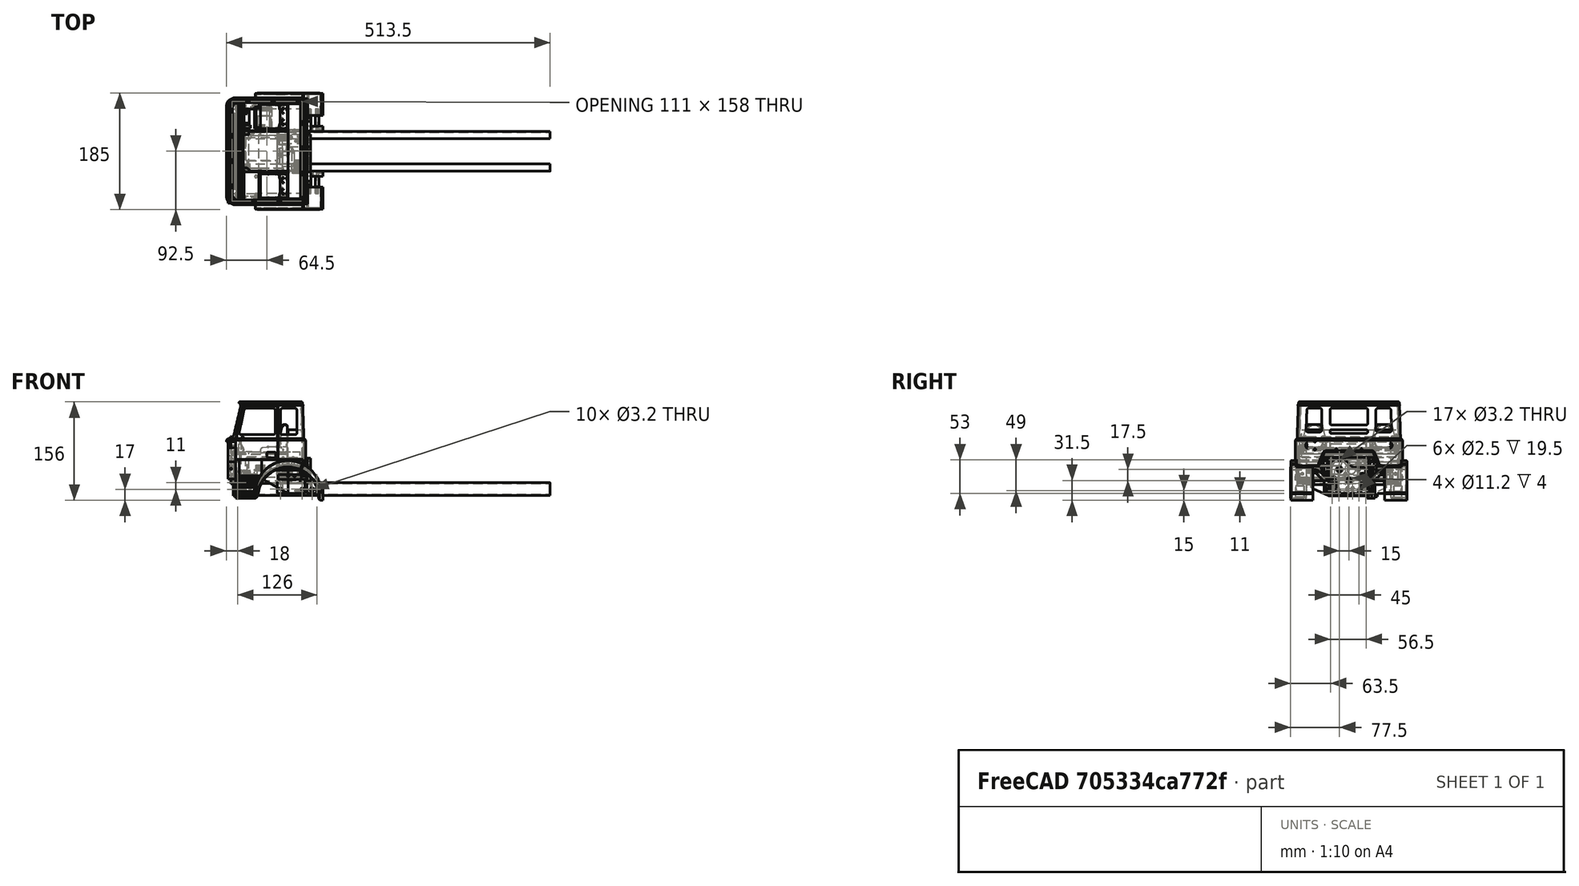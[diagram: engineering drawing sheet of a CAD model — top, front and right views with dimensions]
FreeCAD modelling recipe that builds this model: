
FCSTD DOCUMENT  (FreeCAD 0.16R6668 (Git))
Label: cab-internals
License: All rights reserved
LicenseURL: http://en.wikipedia.org/wiki/All_rights_reserved
objects: Part::Box×270, Part::Cut×252, Part::Cylinder×238, Part::MultiFuse×182, Part::Fillet×140, Part::Chamfer×61, Part::Mirroring×33, Part::Feature×16, Part::Loft×6, Part::Extrusion×2
note: 1200 computed .brp shape members not serialized (recipe doc carries the construction recipe); baked Part::Feature solids carry a one-line shape summary decoded from their .brp

FEATURE [Part::Feature] Cut179  label="cab_tilt_lower002"
  Placement = pos=(15.5,45,-15) rot=(0,0,1;0rad)
  shape: bbox 4 x 120 x 28 mm, 33 faces (baked)
FEATURE [Part::Feature] Cut180  label="cab_tilt_upper002"
  Placement = pos=(15.5,45,-15) rot=(0,0,1;0rad)
  shape: bbox 5.33 x 120 x 34.16 mm, 49 faces (baked)
FEATURE [Part::Cylinder] Cylinder188
  Angle = 360
  Height = 33
  Placement = pos=(98,175,-23) rot=(1,0,0;1.5708rad)
  Radius = 50
FEATURE [Part::Cylinder] Cylinder189
  Angle = 360
  Height = 35
  Placement = pos=(98,177,-23) rot=(1,0,0;1.5708rad)
  Radius = 52
FEATURE [Part::Cylinder] Cylinder190
  Angle = 360
  Height = 33
  Placement = pos=(98,177,-30) rot=(1,0,0;1.5708rad)
  Radius = 48
FEATURE [Part::MultiFuse] Fusion135
  Shapes = -> [Cylinder188,Cylinder190]
FEATURE [Part::Cut] Cut300
  Base = -> Cylinder189
  Tool = -> Fusion135
FEATURE [Part::Box] Box251  label="Cube477"
  Height = 10
  Length = 6.5
  Placement = pos=(145.5,142,-33) rot=(0,0,1;0rad)
  Width = 35
FEATURE [Part::Box] Box252  label="Cube478"
  Height = 10
  Length = 4.5
  Placement = pos=(143.5,140,-33) rot=(0,0,1;0rad)
  Width = 35
FEATURE [Part::Cut] Cut301
  Base = -> Box251
  Tool = -> Box252
FEATURE [Part::MultiFuse] Fusion136
  Shapes = -> [Cut300,Cut301]
FEATURE [Part::Chamfer] Chamfer044
  Base = -> Fusion136
  Edges = 1 edges r=1.99: [Edge8]
FEATURE [Part::Chamfer] Chamfer045
  Base = -> Chamfer044
  Edges = 1 edges r=2.49: [Edge30]
FEATURE [Part::Box] Box253  label="Cube479"
  Height = 11
  Length = 7.5
  Placement = pos=(117.3,133.5,15) rot=(0,1,0;0.471239rad)
  Width = 35
FEATURE [Part::Cylinder] Cylinder192
  Angle = 360
  Height = 23
  Placement = pos=(98,175,-23) rot=(0.829023,-0.395424,0.395424;1.75721rad)
  Radius = 50
FEATURE [Part::Cut] Cut302
  Base = -> Chamfer045
  Tool = -> Box253
FEATURE [Part::Cylinder] Cylinder193
  Angle = 360
  Height = 33
  Placement = pos=(98,175,-23) rot=(1,0,0;1.5708rad)
  Radius = 48
FEATURE [Part::Cut] Cut303
  Base = -> Cylinder192
  Tool = -> Cylinder193
FEATURE [Part::MultiFuse] Fusion137
  Shapes = -> [Cut302,Cut303]
FEATURE [Part::Chamfer] Chamfer046
  Base = -> Fusion137
  Edges = 1 edges r=1.99: [Edge50]
  Placement = pos=(1,0,-1) rot=(0,0,1;0rad)
FEATURE [Part::Fillet] Fillet132
  Base = -> Chamfer046
  Edges = 1 edges r=1: [Edge53]
FEATURE [Part::Cylinder] Cylinder194
  Angle = 360
  Height = 10
  Placement = pos=(144,152,0) rot=(1,0,0;1.5708rad)
  Radius = 3
FEATURE [Part::Cylinder] Cylinder195
  Angle = 360
  Height = 10
  Placement = pos=(144,152,0) rot=(1,0,0;1.5708rad)
  Radius = 1.5
FEATURE [Part::Cut] Cut304
  Base = -> Cylinder194
  Placement = pos=(-13,0,12) rot=(0,0,1;0rad)
  Tool = -> Cylinder195
FEATURE [Part::Cylinder] Cylinder196
  Angle = 360
  Height = 10
  Placement = pos=(144,152,0) rot=(1,0,0;1.5708rad)
  Radius = 3
FEATURE [Part::Cylinder] Cylinder197
  Angle = 360
  Height = 10
  Placement = pos=(144,152,0) rot=(1,0,0;1.5708rad)
  Radius = 1.5
FEATURE [Part::Cut] Cut305
  Base = -> Cylinder196
  Placement = pos=(0,0,-6) rot=(0,0,1;0rad)
  Tool = -> Cylinder197
FEATURE [Part::MultiFuse] Fusion138  label="wing-right-rear_"
  Shapes = -> [Fillet132,Cut305,Cut304]
FEATURE [Part::Cylinder] Cylinder198
  Angle = 360
  Height = 35
  Placement = pos=(98,177,-23) rot=(1,0,0;1.5708rad)
  Radius = 52
FEATURE [Part::Cylinder] Cylinder199
  Angle = 360
  Height = 33
  Placement = pos=(98,175,-23) rot=(1,0,0;1.5708rad)
  Radius = 50
FEATURE [Part::Cylinder] Cylinder200
  Angle = 360
  Height = 33
  Placement = pos=(98,177,-30) rot=(1,0,0;1.5708rad)
  Radius = 48
FEATURE [Part::MultiFuse] Fusion142
  Shapes = -> [Cylinder199,Cylinder200]
FEATURE [Part::Cut] Cut307
  Base = -> Cylinder198
  Tool = -> Fusion142
FEATURE [Part::Box] Box254  label="Cube480"
  Height = 10
  Length = 6.5
  Placement = pos=(145.5,142,-33) rot=(0,0,1;0rad)
  Width = 35
FEATURE [Part::Box] Box255  label="Cube481"
  Height = 10
  Length = 4.5
  Placement = pos=(143.5,140,-33) rot=(0,0,1;0rad)
  Width = 35
FEATURE [Part::Cut] Cut308
  Base = -> Box254
  Tool = -> Box255
FEATURE [Part::MultiFuse] Fusion141
  Shapes = -> [Cut307,Cut308]
FEATURE [Part::Chamfer] Chamfer049
  Base = -> Fusion141
  Edges = 1 edges r=1.99: [Edge8]
FEATURE [Part::Chamfer] Chamfer048
  Base = -> Chamfer049
  Edges = 1 edges r=2.49: [Edge30]
FEATURE [Part::Box] Box256  label="Cube482"
  Height = 11
  Length = 7.5
  Placement = pos=(117.3,133.5,15) rot=(0,1,0;0.471239rad)
  Width = 35
FEATURE [Part::Cut] Cut306
  Base = -> Chamfer048
  Tool = -> Box256
FEATURE [Part::Cylinder] Cylinder201
  Angle = 360
  Height = 23
  Placement = pos=(98,175,-23) rot=(0.829023,-0.395424,0.395424;1.75721rad)
  Radius = 50
FEATURE [Part::Cylinder] Cylinder202
  Angle = 360
  Height = 33
  Placement = pos=(98,175,-23) rot=(1,0,0;1.5708rad)
  Radius = 48
FEATURE [Part::Cut] Cut309
  Base = -> Cylinder201
  Tool = -> Cylinder202
FEATURE [Part::MultiFuse] Fusion140
  Shapes = -> [Cut306,Cut309]
FEATURE [Part::Chamfer] Chamfer047
  Base = -> Fusion140
  Edges = 1 edges r=1.99: [Edge50]
  Placement = pos=(1,0,-1) rot=(0,0,1;0rad)
FEATURE [Part::Fillet] Fillet133
  Base = -> Chamfer047
  Edges = 1 edges r=1: [Edge53]
FEATURE [Part::Cylinder] Cylinder203
  Angle = 360
  Height = 10
  Placement = pos=(144,152,0) rot=(1,0,0;1.5708rad)
  Radius = 3
FEATURE [Part::Cylinder] Cylinder204
  Angle = 360
  Height = 10
  Placement = pos=(144,152,0) rot=(1,0,0;1.5708rad)
  Radius = 1.5
FEATURE [Part::Cut] Cut310
  Base = -> Cylinder203
  Placement = pos=(0,0,-6) rot=(0,0,1;0rad)
  Tool = -> Cylinder204
FEATURE [Part::Cylinder] Cylinder205
  Angle = 360
  Height = 10
  Placement = pos=(144,152,0) rot=(1,0,0;1.5708rad)
  Radius = 3
FEATURE [Part::Cylinder] Cylinder206
  Angle = 360
  Height = 10
  Placement = pos=(144,152,0) rot=(1,0,0;1.5708rad)
  Radius = 1.5
FEATURE [Part::Cut] Cut311
  Base = -> Cylinder205
  Placement = pos=(-13,0,12) rot=(0,0,1;0rad)
  Tool = -> Cylinder206
FEATURE [Part::MultiFuse] Fusion139  label="right-rear-wing001"
  Shapes = -> [Fillet133,Cut310,Cut311]
FEATURE [Part::Mirroring] Part__Mirroring018  label="wing-left-rear_"
  Base = (0,0,0)
  Normal = (0,1,0)
  Placement = pos=(0,170,0) rot=(0,0,1;0rad)
  Source = -> Fusion139
FEATURE [Part::Box] Box536  label="Cube761"
  Height = 64
  Length = 126
  Width = 170
FEATURE [Part::Fillet] Fillet413
  Base = -> Box536
  Edges = 2 edges r=15: [Edge1,Edge3]
FEATURE [Part::Fillet] Fillet412
  Base = -> Fillet413
  Edges = 2 edges r=10: [Edge17,Edge18]
FEATURE [Part::Box] Box537  label="Cube762"
  Height = 64
  Length = 120
  Placement = pos=(4,4,0) rot=(0,0,1;0rad)
  Width = 164
FEATURE [Part::Fillet] Fillet415
  Base = -> Box537
  Edges = 2 edges r=12: [Edge1,Edge3]
FEATURE [Part::Fillet] Fillet414
  Base = -> Fillet415
  Edges = 2 edges r=6: [Edge17,Edge18]
  Placement = pos=(-1,-1,0) rot=(0,0,1;0rad)
FEATURE [Part::Cut] Cut468  label="Cut763"
  Base = -> Fillet412
  Tool = -> Fillet414
FEATURE [Part::Cylinder] Cylinder302
  Angle = 360
  Height = 174
  Placement = pos=(98,174,-23) rot=(1,0,0;1.5708rad)
  Radius = 52
FEATURE [Part::Cut] Cut467  label="Cut762"
  Base = -> Cut468
  Tool = -> Cylinder302
FEATURE [Part::Box] Box538  label="Cube763"
  Height = 25
  Length = 131
  Placement = pos=(11,0,6) rot=(0,0,1;0rad)
  Width = 170
FEATURE [Part::Box] Box539  label="Cube764"
  Height = 25
  Length = 148
  Placement = pos=(2,2,6) rot=(0,0,1;0rad)
  Width = 166
FEATURE [Part::Box] Box540  label="Cube765"
  Height = 31
  Length = 62
  Placement = pos=(83,1,2) rot=(0,0,1;0rad)
  Width = 1
FEATURE [Part::Box] Box541  label="Cube766"
  Height = 31
  Length = 63.5
  Placement = pos=(83,-1,2) rot=(0,0,1;0.017453rad)
  Width = 2
FEATURE [Part::Cut] Cut470  label="Cut765"
  Base = -> Box540
  Tool = -> Box541
FEATURE [Part::Cylinder] Cylinder303
  Angle = 360
  Height = 10
  Placement = pos=(98,10,-23) rot=(1,0,0;1.5708rad)
  Radius = 52
FEATURE [Part::Cut] Cut469  label="Cut764"
  Base = -> Cut470
  Tool = -> Cylinder303
FEATURE [Part::Cylinder] Cylinder304
  Angle = 360
  Height = 10
  Placement = pos=(98,10,-23) rot=(1,0,0;1.5708rad)
  Radius = 52
FEATURE [Part::Box] Box542  label="Cube767"
  Height = 25
  Length = 63.5
  Placement = pos=(20,1,8) rot=(0,0,-1;0.027925rad)
  Width = 1
FEATURE [Part::Box] Box543  label="Cube768"
  Height = 25
  Length = 62.5
  Placement = pos=(20.5,1,8) rot=(0,0,1;0rad)
  Width = 1
FEATURE [Part::Cut] Cut472  label="Cut767"
  Base = -> Box543
  Tool = -> Box542
FEATURE [Part::Cut] Cut471  label="Cut766"
  Base = -> Cut472
  Tool = -> Cylinder304
FEATURE [Part::MultiFuse] Fusion305
  Shapes = -> [Cut469,Cut471]
FEATURE [Part::Box] Box544  label="Cube769"
  Height = 25
  Length = 63.5
  Placement = pos=(20,1,8) rot=(0,0,-1;0.027925rad)
  Width = 1
FEATURE [Part::Box] Box545  label="Cube770"
  Height = 25
  Length = 62.5
  Placement = pos=(20.5,1,8) rot=(0,0,1;0rad)
  Width = 1
FEATURE [Part::Cut] Cut475  label="Cut770"
  Base = -> Box545
  Tool = -> Box544
FEATURE [Part::Box] Box546  label="Cube771"
  Height = 31
  Length = 63.5
  Placement = pos=(83,-1,2) rot=(0,0,1;0.017453rad)
  Width = 2
FEATURE [Part::Box] Box547  label="Cube772"
  Height = 31
  Length = 62
  Placement = pos=(83,1,2) rot=(0,0,1;0rad)
  Width = 1
FEATURE [Part::Cut] Cut473  label="Cut768"
  Base = -> Box547
  Tool = -> Box546
FEATURE [Part::Cylinder] Cylinder305
  Angle = 360
  Height = 10
  Placement = pos=(98,10,-23) rot=(1,0,0;1.5708rad)
  Radius = 52
FEATURE [Part::Cut] Cut476  label="Cut771"
  Base = -> Cut473
  Tool = -> Cylinder305
FEATURE [Part::Cylinder] Cylinder306
  Angle = 360
  Height = 10
  Placement = pos=(98,10,-23) rot=(1,0,0;1.5708rad)
  Radius = 52
FEATURE [Part::Cut] Cut474  label="Cut769"
  Base = -> Cut475
  Tool = -> Cylinder306
FEATURE [Part::MultiFuse] Fusion306
  Shapes = -> [Cut476,Cut474]
FEATURE [Part::Mirroring] Part__Mirroring056  label="Fusion008 (Mirror #2)001"
  Base = (0,0,0)
  Normal = (0,1,0)
  Placement = pos=(0,170,0) rot=(0,0,1;0rad)
  Source = -> Fusion306
FEATURE [Part::MultiFuse] Fusion307
  Shapes = -> [Part__Mirroring056,Fusion305]
FEATURE [Part::Cut] Cut477  label="Cut772"
  Base = -> Box538
  Placement = pos=(0,0,2) rot=(0,0,1;0rad)
  Tool = -> Box539
FEATURE [Part::Cut] Cut478  label="Cut773"
  Base = -> Cut477
  Placement = pos=(0,0,-3) rot=(0,0,1;0rad)
  Tool = -> Fusion307
FEATURE [Part::Cut] Cut479  label="Cut774"
  Base = -> Cut467
  Tool = -> Cut478
FEATURE [Part::Box] Box548  label="Cube773"
  Height = 64
  Length = 21
  Width = 164
FEATURE [Part::Fillet] Fillet416
  Base = -> Box548
  Edges = 2 edges r=12: [Edge1,Edge3]
  Placement = pos=(3,3,0) rot=(0,0,1;0rad)
FEATURE [Part::Box] Box549  label="Cube774"
  Height = 59
  Length = 16
  Placement = pos=(15,0,0) rot=(0,0,1;0rad)
  Width = 170
FEATURE [Part::Box] Box550  label="Cube775"
  Height = 59
  Length = 21
  Placement = pos=(-13,3,0) rot=(0,0,1;0rad)
  Width = 164
FEATURE [Part::Box] Box551  label="Cube776"
  Height = 59
  Length = 21
  Placement = pos=(-13,0,0) rot=(0,0,1;0rad)
  Width = 170
FEATURE [Part::Fillet] Fillet417
  Base = -> Box551
  Edges = 2 edges r=15: [Edge1,Edge3]
FEATURE [Part::Fillet] Fillet418
  Base = -> Box550
  Edges = 2 edges r=12: [Edge1,Edge3]
  Placement = pos=(3,0,0) rot=(0,0,1;0rad)
FEATURE [Part::Cut] Cut480  label="Cut775"
  Base = -> Fillet417
  Placement = pos=(13,0,0) rot=(0,0,1;0rad)
  Tool = -> Fillet418
FEATURE [Part::Cut] Cut481  label="Cut776"
  Base = -> Cut480
  Tool = -> Box549
FEATURE [Part::Feature] Face030
  Placement = pos=(0,0,-10) rot=(0,0,1;0rad)
  shape: bbox 128.7 x 180.4 x 2e-07 mm, 1 faces, 0 solids (baked)
FEATURE [Part::Feature] Face031
  Placement = pos=(0,0,50) rot=(0,0,1;0rad)
  shape: bbox 110 x 176 x 2e-07 mm, 1 faces, 0 solids (baked)
FEATURE [Part::Loft] Loft015
  Closed = false
  Ruled = false
  Sections = -> [Face031,Face030]
  Solid = true
FEATURE [Part::Feature] Face032
  Placement = pos=(0,0,50) rot=(0,0,1;0rad)
  shape: bbox 103.4 x 169.4 x 2e-07 mm, 1 faces, 0 solids (baked)
FEATURE [Part::Feature] Face033
  Placement = pos=(0,0,-10) rot=(0,0,1;0rad)
  shape: bbox 122.1 x 173.8 x 2e-07 mm, 1 faces, 0 solids (baked)
FEATURE [Part::Loft] Loft016
  Closed = false
  Ruled = false
  Sections = -> [Face032,Face033]
  Solid = true
FEATURE [Part::Cut] Cut482  label="Cut777"
  Base = -> Loft015
  Tool = -> Loft016
FEATURE [Part::Box] Box552  label="Cube777"
  Height = 55
  Length = 10
  Placement = pos=(0,7,68) rot=(0,1,0;0.226893rad)
  Width = 156
FEATURE [Part::Chamfer] Chamfer066
  Base = -> Cut479
  Edges = 4 edges r=2.5: [Edge1,Edge4,Edge5,Edge8]
FEATURE [Part::Chamfer] Chamfer067
  Base = -> Chamfer066
  Edges = 4 edges r=0.9: [Edge52,Edge80,Edge102,Edge110]
FEATURE [Part::Fillet] Fillet419
  Base = -> Box552
  Edges = 4 edges r=5: [Edge9,Edge10,Edge11,Edge12]
  Placement = pos=(6,0,-1) rot=(0,0,1;0rad)
FEATURE [Part::Box] Box553  label="Cube778"
  Height = 42
  Length = 26
  Placement = pos=(89,4.3,70) rot=(-1,0,0;0.038397rad)
  Width = 5
FEATURE [Part::Fillet] Fillet420
  Base = -> Box553
  Edges = 4 edges r=3: [Edge2,Edge4,Edge6,Edge8]
  Placement = pos=(-3,-2,0) rot=(0,0,1;0rad)
FEATURE [Part::Box] Box554  label="Cube779"
  Height = 42
  Length = 58
  Placement = pos=(19.5,2,70) rot=(-1,0,0;0.038397rad)
  Width = 5
FEATURE [Part::Box] Box555  label="Cube780"
  Height = 48
  Length = 11
  Placement = pos=(8.5,1,70) rot=(-0.179679,0.983544,0.018885;0.212918rad)
  Width = 7
FEATURE [Part::Cut] Cut483  label="Cut778"
  Base = -> Box554
  Tool = -> Box555
FEATURE [Part::Fillet] Fillet421
  Base = -> Cut483
  Edges = 4 edges r=3: [Edge2,Edge4,Edge8,Edge12]
FEATURE [Part::MultiFuse] Fusion308  label="left-windows-holes001"
  Shapes = -> [Fillet420,Fillet421]
FEATURE [Part::Box] Box556  label="Cube781"
  Height = 42
  Length = 26
  Placement = pos=(89,4.3,70) rot=(-1,0,0;0.038397rad)
  Width = 5
FEATURE [Part::Fillet] Fillet422
  Base = -> Box556
  Edges = 4 edges r=3: [Edge2,Edge4,Edge6,Edge8]
  Placement = pos=(-3,-2,0) rot=(0,0,1;0rad)
FEATURE [Part::Box] Box557  label="Cube782"
  Height = 42
  Length = 58
  Placement = pos=(19.5,2,70) rot=(-1,0,0;0.038397rad)
  Width = 5
FEATURE [Part::Box] Box558  label="Cube783"
  Height = 48
  Length = 11
  Placement = pos=(8.5,1,70) rot=(-0.179679,0.983544,0.018885;0.212918rad)
  Width = 7
FEATURE [Part::Cut] Cut484  label="Cut779"
  Base = -> Box557
  Tool = -> Box558
FEATURE [Part::Fillet] Fillet423
  Base = -> Cut484
  Edges = 4 edges r=3: [Edge2,Edge4,Edge8,Edge12]
FEATURE [Part::MultiFuse] Fusion309
  Shapes = -> [Fillet422,Fillet423]
FEATURE [Part::Mirroring] Part__Mirroring057  label="right-windows-holes001"
  Base = (0,0,0)
  Normal = (0,1,0)
  Placement = pos=(0,170,0) rot=(0,0,1;0rad)
  Source = -> Fusion309
FEATURE [Part::Box] Box559  label="Cube784"
  Height = 25
  Length = 10
  Placement = pos=(150,40,0) rot=(0,0,1;0rad)
  Width = 100
FEATURE [Part::Box] Box560  label="Cube785"
  Height = 40
  Length = 10
  Placement = pos=(150,19,0) rot=(-1,0,0;0.383972rad)
  Width = 20
FEATURE [Part::Box] Box561  label="Cube786"
  Height = 40
  Length = 10
  Placement = pos=(150,19,0) rot=(-1,0,0;0.383972rad)
  Width = 20
FEATURE [Part::Mirroring] Part__Mirroring058  label="Cube088 (Mirror #13)001"
  Base = (0,0,0)
  Normal = (0,1,0)
  Placement = pos=(0,180,0) rot=(0,0,1;0rad)
  Source = -> Box561
FEATURE [Part::MultiFuse] Fusion310
  Shapes = -> [Box560,Part__Mirroring058]
FEATURE [Part::Cut] Cut485  label="Cut780"
  Base = -> Box559
  Placement = pos=(-30,-5,20) rot=(0,0,1;0rad)
  Tool = -> Fusion310
FEATURE [Part::Fillet] Fillet424
  Base = -> Cut485
  Edges = 2 edges r=6: [Edge5,Edge6]
FEATURE [Part::Box] Box562  label="Cube787"
  Height = 27
  Length = 7
  Placement = pos=(116,55,85) rot=(0,-1,0;0.034907rad)
  Width = 60
FEATURE [Part::Box] Box563  label="Cube788"
  Height = 38
  Length = 5
  Placement = pos=(175,0,0) rot=(0,0,1;0rad)
  Width = 25
FEATURE [Part::Box] Box564  label="Cube789"
  Height = 40
  Length = 5
  Placement = pos=(175,-24,-1) rot=(-1,0,0;0.038397rad)
  Width = 24
FEATURE [Part::Cut] Cut486  label="Cut781"
  Base = -> Box563
  Placement = pos=(0,1,1) rot=(0,0,1;0rad)
  Tool = -> Box564
FEATURE [Part::Cylinder] Cylinder307
  Angle = 360
  Height = 134
  Radius = 3.7
FEATURE [Part::Fillet] Fillet425
  Base = -> Cylinder307
  Edges = 2 edges r=2: [Edge1,Edge3]
  Placement = pos=(128,152,53) rot=(1,0,0;1.5708rad)
FEATURE [Part::Box] Box565  label="Cube790"
  Height = 38
  Length = 5
  Placement = pos=(175,0,0) rot=(0,0,1;0rad)
  Width = 25
FEATURE [Part::Box] Box566  label="Cube791"
  Height = 40
  Length = 5
  Placement = pos=(175,-24,-1) rot=(-1,0,0;0.038397rad)
  Width = 24
FEATURE [Part::Cut] Cut487  label="Cut782"
  Base = -> Box565
  Placement = pos=(-57,17,74) rot=(0,0,1;0rad)
  Tool = -> Box566
FEATURE [Part::Mirroring] Part__Mirroring059  label="Cut783"
  Base = (0,0,0)
  Normal = (0,1,0)
  Placement = pos=(-57,154,73) rot=(0,0,1;0rad)
  Source = -> Cut486
FEATURE [Part::Fillet] Fillet426
  Base = -> Cut487
  Edges = 4 edges r=3: [Edge1,Edge3,Edge5,Edge10]
  Placement = pos=(3,0,-4) rot=(0,-1,0;0.034907rad)
FEATURE [Part::Fillet] Fillet427
  Base = -> Part__Mirroring059
  Edges = 4 edges r=3: [Edge1,Edge3,Edge5,Edge10]
  Placement = pos=(3,0,-4) rot=(0,-1,0;0.034907rad)
FEATURE [Part::Cylinder] Cylinder308
  Angle = 360
  Height = 60
  Radius = 3.7
FEATURE [Part::Fillet] Fillet428
  Base = -> Cylinder308
  Edges = 2 edges r=2: [Edge1,Edge3]
  Placement = pos=(125,115,75) rot=(1,0,0;1.5708rad)
FEATURE [Part::Box] Box567  label="Cube792"
  Height = 9
  Length = 14
  Width = 2
FEATURE [Part::Fillet] Fillet429
  Base = -> Box567
  Edges = 4 edges r=2: [Edge2,Edge4,Edge6,Edge8]
  Placement = pos=(68.5,0,46.5) rot=(0,0,1;0rad)
FEATURE [Part::Box] Box568  label="Cube793"
  Height = 9
  Length = 14
  Width = 2
FEATURE [Part::Fillet] Fillet430
  Base = -> Box568
  Edges = 4 edges r=2: [Edge2,Edge4,Edge6,Edge8]
  Placement = pos=(68.5,168,46.5) rot=(0,0,1;0rad)
FEATURE [Part::MultiFuse] Fusion311
  Placement = pos=(-4,0,-13) rot=(0,0,1;0rad)
  Shapes = -> [Fillet430,Fillet429]
FEATURE [Part::MultiFuse] Fusion312
  Shapes = -> [Fillet427,Box562,Part__Mirroring057,Fusion308,Fillet426]
FEATURE [Part::Box] Box569  label="Cube794"
  Height = 116
  Length = 66.5
  Placement = pos=(14.5,0,-0.5) rot=(0,0,1;0rad)
  Width = 5
FEATURE [Part::Box] Box570  label="Cube795"
  Height = 117
  Length = 67.5
  Placement = pos=(14,0,-1) rot=(0,0,1;0rad)
  Width = 5
FEATURE [Part::Box] Box571  label="Cube796"
  Height = 116
  Length = 67
  Placement = pos=(-53.2,0,65) rot=(0,1,0;0.218166rad)
  Width = 5
FEATURE [Part::Cut] Cut489  label="Cut785"
  Base = -> Box569
  Placement = pos=(0,-2,0) rot=(0,0,1;0rad)
  Tool = -> Box571
FEATURE [Part::Box] Box572  label="Cube797"
  Height = 116
  Length = 67
  Placement = pos=(-53.7,0,65) rot=(0,1,0;0.218166rad)
  Width = 5
FEATURE [Part::Cut] Cut488  label="Cut784"
  Base = -> Box570
  Placement = pos=(0,-2,0) rot=(0,0,1;0rad)
  Tool = -> Box572
FEATURE [Part::Cut] Cut490  label="Cut786"
  Base = -> Cut482
  Tool = -> Fusion312
FEATURE [Part::Cut] Cut491  label="doors-cut-002"
  Base = -> Cut488
  Placement = pos=(0.5,3,0.5) rot=(0,0,1;0rad)
  Tool = -> Cut489
FEATURE [Part::Cut] Cut492  label="Cut787"
  Base = -> Cut490
  Tool = -> Fillet419
FEATURE [Part::Box] Box573  label="Cube798"
  Height = 116
  Length = 67
  Placement = pos=(-53.2,0,65) rot=(0,1,0;0.218166rad)
  Width = 10
FEATURE [Part::Box] Box574  label="Cube799"
  Height = 116
  Length = 67
  Placement = pos=(-53.7,0,65) rot=(0,1,0;0.218166rad)
  Width = 10
FEATURE [Part::Box] Box575  label="Cube800"
  Height = 117
  Length = 67.5
  Placement = pos=(14,0,-1) rot=(0,0,1;0rad)
  Width = 10
FEATURE [Part::Cut] Cut494  label="Cut788"
  Base = -> Box575
  Placement = pos=(0,-2,0) rot=(0,0,1;0rad)
  Tool = -> Box574
FEATURE [Part::Box] Box576  label="Cube801"
  Height = 116
  Length = 66.5
  Placement = pos=(14.5,0,-0.5) rot=(0,0,1;0rad)
  Width = 10
FEATURE [Part::Cut] Cut495  label="Cut789"
  Base = -> Box576
  Placement = pos=(0,-2,0) rot=(0,0,1;0rad)
  Tool = -> Box573
FEATURE [Part::Cut] Cut493  label="doors-cut-003"
  Base = -> Cut494
  Placement = pos=(1.5,-3,0.5) rot=(0,0,1;0rad)
  Tool = -> Cut495
FEATURE [Part::Fillet] Fillet431
  Base = -> Cut492
  Edges = 4 edges r=3: [Edge209,Edge210,Edge211,Edge212]
FEATURE [Part::Cut] Cut496  label="Cut790"
  Base = -> Fillet431
  Tool = -> Fillet428
FEATURE [Part::Box] Box577  label="Cube802"
  Height = 64
  Length = 21
  Width = 164
FEATURE [Part::Fillet] Fillet432
  Base = -> Box577
  Edges = 2 edges r=18: [Edge1,Edge3]
  Placement = pos=(7,3,0) rot=(0,0,1;0rad)
FEATURE [Part::Cut] Cut497  label="Cut791"
  Base = -> Fillet416
  Tool = -> Fillet432
FEATURE [Part::MultiFuse] Fusion313
  Shapes = -> [Chamfer067,Cut497]
FEATURE [Part::Cut] Cut498  label="Cut792"
  Base = -> Fusion313
  Tool = -> Cut481
FEATURE [Part::Cut] Cut499  label="Cut793"
  Base = -> Cut498
  Tool = -> Fillet425
FEATURE [Part::Cut] Cut500  label="Cut794"
  Base = -> Cut499
  Tool = -> Fillet424
FEATURE [Part::Cut] Cut501  label="Cut795"
  Base = -> Cut500
  Tool = -> Fusion311
FEATURE [Part::Fillet] Fillet433
  Base = -> Cut501
  Edges = 2 edges r=3: [Edge74,Edge149]
FEATURE [Part::Box] Box578  label="Cube803"
  Height = 2
  Length = 117
  Placement = pos=(6,3,54) rot=(0,0,1;0rad)
  Width = 164
FEATURE [Part::Fillet] Fillet434
  Base = -> Box578
  Edges = 2 edges r=15: [Edge1,Edge3]
FEATURE [Part::Fillet] Fillet435
  Base = -> Fillet434
  Edges = 2 edges r=6: [Edge17,Edge18]
FEATURE [Part::Box] Box579  label="Cube804"
  Height = 2
  Length = 111
  Placement = pos=(6,3,54) rot=(0,0,1;0rad)
  Width = 158
FEATURE [Part::Fillet] Fillet437
  Base = -> Box579
  Edges = 2 edges r=12: [Edge1,Edge3]
FEATURE [Part::Fillet] Fillet436
  Base = -> Fillet437
  Edges = 2 edges r=3: [Edge17,Edge18]
  Placement = pos=(3,3,0) rot=(0,0,1;0rad)
FEATURE [Part::Cut] Cut502  label="Cut796"
  Base = -> Fillet435
  Placement = pos=(0,0,8) rot=(0,0,1;0rad)
  Tool = -> Fillet436
FEATURE [Part::Box] Box580  label="Cube805"
  Height = 1
  Length = 96
  Placement = pos=(26,4,116.5) rot=(0,0,1;0rad)
  Width = 162
FEATURE [Part::Box] Box581  label="Cube806"
  Height = 1
  Length = 94
  Placement = pos=(26,6,116.5) rot=(0,0,1;0rad)
  Width = 158
FEATURE [Part::Fillet] Fillet438
  Base = -> Box581
  Edges = 2 edges r=4: [Edge5,Edge7]
FEATURE [Part::Fillet] Fillet439
  Base = -> Box580
  Edges = 2 edges r=6: [Edge5,Edge7]
FEATURE [Part::Fillet] Fillet440
  Base = -> Fillet439
  Edges = 2 edges r=2: [Edge17,Edge18]
FEATURE [Part::Cut] Cut503  label="Cut797"
  Base = -> Fillet440
  Tool = -> Fillet438
FEATURE [Part::Box] Box582  label="Cube807"
  Height = 6.5
  Length = 110
  Placement = pos=(19,4,121.5) rot=(0,0,1;0rad)
  Width = 162
FEATURE [Part::Box] Box583  label="Cube808"
  Height = 5.1
  Length = 100
  Placement = pos=(19.5,5.5,122.5) rot=(0,0,1;0rad)
  Width = 159
FEATURE [Part::Fillet] Fillet441
  Base = -> Box583
  Edges = 2 edges r=10: [Edge1,Edge3]
FEATURE [Part::Fillet] Fillet442
  Base = -> Fillet441
  Edges = 2 edges r=4.5: [Edge17,Edge18]
FEATURE [Part::Fillet] Fillet443
  Base = -> Fillet442
  Edges = 4 edges r=5: [Edge1,Edge4,Edge5,Edge8]
  Placement = pos=(0.7,0,-2) rot=(0,0,1;0rad)
FEATURE [Part::Box] Box584  label="Cube809"
  Height = 5.1
  Length = 95
  Placement = pos=(23,7.5,122.5) rot=(0,0,1;0rad)
  Width = 155
FEATURE [Part::Fillet] Fillet444
  Base = -> Box584
  Edges = 2 edges r=3: [Edge5,Edge7]
FEATURE [Part::Fillet] Fillet445
  Base = -> Fillet444
  Edges = 2 edges r=8: [Edge17,Edge18]
FEATURE [Part::Fillet] Fillet446
  Base = -> Fillet445
  Edges = 1 edges r=4: [Edge4]
  Placement = pos=(0,0,-4) rot=(0,0,1;0rad)
FEATURE [Part::Cut] Cut504  label="Cut798"
  Base = -> Fillet443
  Tool = -> Fillet446
FEATURE [Part::Cylinder] Cylinder309
  Angle = 360
  Height = 7
  Placement = pos=(2,34,15) rot=(0,1,0;1.5708rad)
  Radius = 1.2
FEATURE [Part::Cylinder] Cylinder310
  Angle = 360
  Height = 4
  Placement = pos=(2,34,15) rot=(0,1,0;1.5708rad)
  Radius = 2.7
FEATURE [Part::MultiFuse] Fusion314
  Shapes = -> [Cylinder309,Cylinder310]
FEATURE [Part::Cylinder] Cylinder311
  Angle = 360
  Height = 4
  Placement = pos=(2,34,15) rot=(0,1,0;1.5708rad)
  Radius = 2.7
FEATURE [Part::Cylinder] Cylinder312
  Angle = 360
  Height = 7
  Placement = pos=(2,34,15) rot=(0,1,0;1.5708rad)
  Radius = 1.2
FEATURE [Part::MultiFuse] Fusion315
  Placement = pos=(0,102,0) rot=(0,0,1;0rad)
  Shapes = -> [Cylinder312,Cylinder311]
FEATURE [Part::MultiFuse] Fusion316
  Shapes = -> [Fusion314,Fusion315]
FEATURE [Part::Box] Box585  label="Cube810"
  Height = 34
  Length = 5
  Placement = pos=(7,38,2) rot=(0,0,1;0rad)
  Width = 94
FEATURE [Part::Chamfer] Chamfer068
  Base = -> Box585
  Edges = 1 edges r=4.99: [Edge6]
FEATURE [Part::Cylinder] Cylinder313
  Angle = 360
  Height = 10
  Placement = pos=(12,57.5,21) rot=(0,1,0;1.5708rad)
  Radius = 1.25
FEATURE [Part::Cylinder] Cylinder314
  Angle = 360
  Height = 10
  Placement = pos=(12,112.5,21) rot=(0,1,0;1.5708rad)
  Radius = 1.25
FEATURE [Part::Cylinder] Cylinder315
  Angle = 360
  Height = 10
  Placement = pos=(12,85,16) rot=(0,1,0;1.5708rad)
  Radius = 1.25
FEATURE [Part::MultiFuse] Fusion317
  Placement = pos=(-7,0,0) rot=(0,0,1;0rad)
  Shapes = -> [Cylinder313,Cylinder315,Cylinder314]
FEATURE [Part::Cylinder] Cylinder316
  Angle = 360
  Height = 10
  Placement = pos=(118,31,59.5) rot=(0,1,0;1.5708rad)
  Radius = 1.3
FEATURE [Part::Cylinder] Cylinder317
  Angle = 360
  Height = 10
  Placement = pos=(118,31,46.5) rot=(0,1,0;1.5708rad)
  Radius = 1.3
FEATURE [Part::MultiFuse] Fusion318
  Shapes = -> [Cylinder316,Cylinder317]
FEATURE [Part::Box] Box586  label="Cube811"
  Height = 6
  Length = 2
  Placement = pos=(89,3,29) rot=(0,0,1;0rad)
  Width = 2
FEATURE [Part::Box] Box587  label="Cube812"
  Height = 6
  Length = 2
  Placement = pos=(105,3,29) rot=(0,0,1;0rad)
  Width = 2
FEATURE [Part::MultiFuse] Fusion319
  Shapes = -> [Box586,Box587]
FEATURE [Part::Chamfer] Chamfer069
  Base = -> Fusion319
  Edges = 2 edges r=1.99: [Edge8,Edge20]
FEATURE [Part::Box] Box588  label="Cube813"
  Height = 6
  Length = 2
  Placement = pos=(89,3,29) rot=(0,0,1;0rad)
  Width = 2
FEATURE [Part::Box] Box589  label="Cube814"
  Height = 6
  Length = 2
  Placement = pos=(105,3,29) rot=(0,0,1;0rad)
  Width = 2
FEATURE [Part::MultiFuse] Fusion320
  Shapes = -> [Box588,Box589]
FEATURE [Part::Chamfer] Chamfer070
  Base = -> Fusion320
  Edges = 2 edges r=1.99: [Edge8,Edge20]
FEATURE [Part::Mirroring] Part__Mirroring060  label="Chamfer052 (Mirror #23)001"
  Base = (0,0,0)
  Normal = (0,1,0)
  Placement = pos=(0,170,0) rot=(0,0,1;0rad)
  Source = -> Chamfer070
FEATURE [Part::Cylinder] Cylinder318
  Angle = 360
  Height = 10
  Placement = pos=(30,11,114) rot=(1,0,0;1.5708rad)
  Radius = 1
FEATURE [Part::Cylinder] Cylinder319
  Angle = 360
  Height = 10
  Placement = pos=(26,11,66) rot=(1,0,0;1.5708rad)
  Radius = 1
FEATURE [Part::MultiFuse] Fusion321
  Shapes = -> [Cylinder318,Cylinder319]
FEATURE [Part::Cylinder] Cylinder320
  Angle = 360
  Height = 10
  Placement = pos=(26,11,66) rot=(1,0,0;1.5708rad)
  Radius = 1
FEATURE [Part::Cylinder] Cylinder321
  Angle = 360
  Height = 10
  Placement = pos=(30,11,114) rot=(1,0,0;1.5708rad)
  Radius = 1
FEATURE [Part::MultiFuse] Fusion322
  Shapes = -> [Cylinder321,Cylinder320]
FEATURE [Part::Mirroring] Part__Mirroring061  label="Fusion203 (Mirror #26)001"
  Base = (0,0,0)
  Normal = (0,1,0)
  Placement = pos=(0,170,0) rot=(0,0,1;0rad)
  Source = -> Fusion322
FEATURE [Part::MultiFuse] Fusion323
  Shapes = -> [Fusion321,Part__Mirroring061]
FEATURE [Part::Cylinder] Cylinder322
  Angle = 360
  Height = 10
  Placement = pos=(119,65,45) rot=(0,1,0;1.5708rad)
  Radius = 1
FEATURE [Part::Cylinder] Cylinder323
  Angle = 360
  Height = 10
  Placement = pos=(119,105,45) rot=(0,1,0;1.5708rad)
  Radius = 1
FEATURE [Part::MultiFuse] Fusion324
  Placement = pos=(0,0,2) rot=(0,0,1;0rad)
  Shapes = -> [Cylinder322,Cylinder323]
FEATURE [Part::Box] Box590  label="Cube815"
  Height = 5.1
  Length = 105
  Placement = pos=(19.5,5.5,122) rot=(0,0,1;0rad)
  Width = 159
FEATURE [Part::Box] Box591  label="Cube816"
  Height = 5.1
  Length = 95
  Placement = pos=(23,7.5,122.5) rot=(0,0,1;0rad)
  Width = 155
FEATURE [Part::Fillet] Fillet448
  Base = -> Box591
  Edges = 2 edges r=3: [Edge5,Edge7]
FEATURE [Part::Fillet] Fillet447
  Base = -> Fillet448
  Edges = 2 edges r=8: [Edge17,Edge18]
  Placement = pos=(0,0,-5) rot=(0,0,1;0rad)
FEATURE [Part::Cylinder] Cylinder324
  Angle = 360
  Height = 170
  Placement = pos=(26,170,120) rot=(1,0,0;1.5708rad)
  Radius = 1
FEATURE [Part::Feature] Face034
  Placement = pos=(0,0,-10) rot=(0,0,1;0rad)
  shape: bbox 128.7 x 180.4 x 2e-07 mm, 1 faces, 0 solids (baked)
FEATURE [Part::Feature] Face035
  Placement = pos=(0,0,50) rot=(0,0,1;0rad)
  shape: bbox 110 x 176 x 2e-07 mm, 1 faces, 0 solids (baked)
FEATURE [Part::Loft] Loft017
  Closed = false
  Ruled = false
  Sections = -> [Face035,Face034]
  Solid = true
FEATURE [Part::Box] Box592  label="Cube817"
  Height = 65
  Length = 67.5
  Placement = pos=(14.5,1,-1) rot=(0,0,1;0rad)
  Width = 5
FEATURE [Part::Cut] Cut505  label="Cut799"
  Base = -> Cut491
  Tool = -> Box592
FEATURE [Part::Cut] Cut506  label="Cut800"
  Base = -> Cut505
  Placement = pos=(0,0.75,0) rot=(0,0,1;0rad)
  Tool = -> Loft017
FEATURE [Part::Box] Box593  label="Cube818"
  Height = 116
  Length = 66.5
  Placement = pos=(14.5,0,-0.5) rot=(0,0,1;0rad)
  Width = 5
FEATURE [Part::Box] Box594  label="Cube819"
  Height = 117
  Length = 67.5
  Placement = pos=(14,0,-1) rot=(0,0,1;0rad)
  Width = 5
FEATURE [Part::Box] Box595  label="Cube820"
  Height = 116
  Length = 67
  Placement = pos=(-53.2,0,65) rot=(0,1,0;0.218166rad)
  Width = 5
FEATURE [Part::Cut] Cut508  label="Cut802"
  Base = -> Box593
  Placement = pos=(0,-2,0) rot=(0,0,1;0rad)
  Tool = -> Box595
FEATURE [Part::Box] Box596  label="Cube821"
  Height = 116
  Length = 67
  Placement = pos=(-53.7,0,65) rot=(0,1,0;0.218166rad)
  Width = 5
FEATURE [Part::Cut] Cut507  label="Cut801"
  Base = -> Box594
  Placement = pos=(0,-2,0) rot=(0,0,1;0rad)
  Tool = -> Box596
FEATURE [Part::Cut] Cut509  label="doors-cut-004"
  Base = -> Cut507
  Placement = pos=(0.5,3,0.5) rot=(0,0,1;0rad)
  Tool = -> Cut508
FEATURE [Part::Feature] Face036
  Placement = pos=(0,0,-10) rot=(0,0,1;0rad)
  shape: bbox 128.7 x 180.4 x 2e-07 mm, 1 faces, 0 solids (baked)
FEATURE [Part::Feature] Face037
  Placement = pos=(0,0,50) rot=(0,0,1;0rad)
  shape: bbox 110 x 176 x 2e-07 mm, 1 faces, 0 solids (baked)
FEATURE [Part::Loft] Loft018
  Closed = false
  Ruled = false
  Sections = -> [Face037,Face036]
  Solid = true
FEATURE [Part::Box] Box597  label="Cube822"
  Height = 65
  Length = 67.5
  Placement = pos=(14.5,1,-1) rot=(0,0,1;0rad)
  Width = 5
FEATURE [Part::Cut] Cut510  label="Cut803"
  Base = -> Cut509
  Tool = -> Box597
FEATURE [Part::Cut] Cut511  label="Cut804"
  Base = -> Cut510
  Placement = pos=(0,0.75,0) rot=(0,0,1;0rad)
  Tool = -> Loft018
FEATURE [Part::Mirroring] Part__Mirroring062  label="Cut472 (Mirror #14)"
  Base = (0,0,0)
  Normal = (0,1,0)
  Placement = pos=(0,170,0) rot=(0,0,1;0rad)
  Source = -> Cut511
FEATURE [Part::MultiFuse] Fusion325
  Shapes = -> [Cut506,Part__Mirroring062]
FEATURE [Part::Fillet] Fillet449
  Base = -> Fusion325
  Edges = 4 edges r=1: [Edge19,Edge23,Edge46,Edge50]
FEATURE [Part::Fillet] Fillet450
  Base = -> Fillet449
  Edges = 4 edges r=1.5: [Edge21,Edge27,Edge54,Edge60]
FEATURE [Part::Cut] Cut512  label="Cut805"
  Base = -> Cut496
  Tool = -> Fillet450
FEATURE [Part::MultiFuse] Fusion256
  Shapes = -> [Cut503,Cut512]
FEATURE [Part::Cut] Cut513  label="Cut806"
  Base = -> Fusion256
  Tool = -> Box582
FEATURE [Part::Cut] Cut514  label="Cut807"
  Base = -> Cut513
  Tool = -> Fusion323
FEATURE [Part::Fillet] Fillet341
  Base = -> Cut514
  Edges = 4 edges r=1.49: [Edge134,Edge138,Edge141,Edge142]
FEATURE [Part::MultiFuse] Fusion326
  Shapes = -> [Cut504,Fillet341]
FEATURE [Part::Cut] Cut515  label="Cut808"
  Base = -> Fusion326
  Tool = -> Box590
FEATURE [Part::Cut] Cut516  label="Cut809"
  Base = -> Cut515
  Tool = -> Fillet447
FEATURE [Part::Cut] Cut517  label="Cut810"
  Base = -> Cut516
  Tool = -> Cylinder324
FEATURE [Part::Fillet] Fillet342  label="cab-upper-part-02"
  Base = -> Cut517
  Edges = 6 edges r=0.5: [Edge347,Edge361,Edge367,Edge386,Edge396,Edge398]
  Placement = pos=(0,0,8) rot=(0,0,1;0rad)
FEATURE [Part::MultiFuse] Fusion327
  Shapes = -> [Cut502,Fillet433]
FEATURE [Part::MultiFuse] Fusion328
  Shapes = -> [Cut502,Fillet433]
FEATURE [Part::Cut] Cut518  label="Cut811"
  Base = -> Cut493
  Placement = pos=(-1,0,0) rot=(0,0,1;0rad)
  Tool = -> Fusion327
FEATURE [Part::Box] Box598  label="Cube823"
  Height = 53
  Length = 67.5
  Placement = pos=(14.5,-5,64) rot=(0,0,1;0rad)
  Width = 10
FEATURE [Part::Cut] Cut519  label="Cut812"
  Base = -> Cut518
  Placement = pos=(0,0.75,0) rot=(0,0,1;0rad)
  Tool = -> Box598
FEATURE [Part::Box] Box599  label="Cube824"
  Height = 64
  Length = 126
  Width = 170
FEATURE [Part::Fillet] Fillet344
  Base = -> Box599
  Edges = 2 edges r=15: [Edge1,Edge3]
FEATURE [Part::Fillet] Fillet343
  Base = -> Fillet344
  Edges = 2 edges r=10: [Edge17,Edge18]
FEATURE [Part::Box] Box600  label="Cube825"
  Height = 64
  Length = 120
  Placement = pos=(4,4,0) rot=(0,0,1;0rad)
  Width = 164
FEATURE [Part::Fillet] Fillet346
  Base = -> Box600
  Edges = 2 edges r=12: [Edge1,Edge3]
FEATURE [Part::Fillet] Fillet345
  Base = -> Fillet346
  Edges = 2 edges r=6: [Edge17,Edge18]
  Placement = pos=(-1,-1,0) rot=(0,0,1;0rad)
FEATURE [Part::Cut] Cut521  label="Cut814"
  Base = -> Fillet343
  Tool = -> Fillet345
FEATURE [Part::Cylinder] Cylinder325
  Angle = 360
  Height = 174
  Placement = pos=(98,174,-23) rot=(1,0,0;1.5708rad)
  Radius = 52
FEATURE [Part::Cut] Cut520  label="Cut813"
  Base = -> Cut521
  Tool = -> Cylinder325
FEATURE [Part::Box] Box601  label="Cube826"
  Height = 25
  Length = 131
  Placement = pos=(11,0,6) rot=(0,0,1;0rad)
  Width = 170
FEATURE [Part::Box] Box602  label="Cube827"
  Height = 25
  Length = 148
  Placement = pos=(2,2,6) rot=(0,0,1;0rad)
  Width = 166
FEATURE [Part::Box] Box603  label="Cube828"
  Height = 31
  Length = 62
  Placement = pos=(83,1,2) rot=(0,0,1;0rad)
  Width = 1
FEATURE [Part::Box] Box604  label="Cube829"
  Height = 31
  Length = 63.5
  Placement = pos=(83,-1,2) rot=(0,0,1;0.017453rad)
  Width = 2
FEATURE [Part::Cut] Cut523  label="Cut816"
  Base = -> Box603
  Tool = -> Box604
FEATURE [Part::Cylinder] Cylinder326
  Angle = 360
  Height = 10
  Placement = pos=(98,10,-23) rot=(1,0,0;1.5708rad)
  Radius = 52
FEATURE [Part::Cut] Cut522  label="Cut815"
  Base = -> Cut523
  Tool = -> Cylinder326
FEATURE [Part::Cylinder] Cylinder327
  Angle = 360
  Height = 10
  Placement = pos=(98,10,-23) rot=(1,0,0;1.5708rad)
  Radius = 52
FEATURE [Part::Box] Box605  label="Cube830"
  Height = 25
  Length = 63.5
  Placement = pos=(20,1,8) rot=(0,0,-1;0.027925rad)
  Width = 1
FEATURE [Part::Box] Box606  label="Cube831"
  Height = 25
  Length = 62.5
  Placement = pos=(20.5,1,8) rot=(0,0,1;0rad)
  Width = 1
FEATURE [Part::Cut] Cut525  label="Cut818"
  Base = -> Box606
  Tool = -> Box605
FEATURE [Part::Cut] Cut524  label="Cut817"
  Base = -> Cut525
  Tool = -> Cylinder327
FEATURE [Part::MultiFuse] Fusion260
  Shapes = -> [Cut522,Cut524]
FEATURE [Part::Box] Box607  label="Cube832"
  Height = 25
  Length = 63.5
  Placement = pos=(20,1,8) rot=(0,0,-1;0.027925rad)
  Width = 1
FEATURE [Part::Box] Box608  label="Cube833"
  Height = 25
  Length = 62.5
  Placement = pos=(20.5,1,8) rot=(0,0,1;0rad)
  Width = 1
FEATURE [Part::Cut] Cut528  label="Cut821"
  Base = -> Box608
  Tool = -> Box607
FEATURE [Part::Box] Box609  label="Cube834"
  Height = 31
  Length = 63.5
  Placement = pos=(83,-1,2) rot=(0,0,1;0.017453rad)
  Width = 2
FEATURE [Part::Box] Box610  label="Cube835"
  Height = 31
  Length = 62
  Placement = pos=(83,1,2) rot=(0,0,1;0rad)
  Width = 1
FEATURE [Part::Cut] Cut526  label="Cut819"
  Base = -> Box610
  Tool = -> Box609
FEATURE [Part::Cylinder] Cylinder328
  Angle = 360
  Height = 10
  Placement = pos=(98,10,-23) rot=(1,0,0;1.5708rad)
  Radius = 52
FEATURE [Part::Cut] Cut529  label="Cut822"
  Base = -> Cut526
  Tool = -> Cylinder328
FEATURE [Part::Cylinder] Cylinder329
  Angle = 360
  Height = 10
  Placement = pos=(98,10,-23) rot=(1,0,0;1.5708rad)
  Radius = 52
FEATURE [Part::Cut] Cut527  label="Cut820"
  Base = -> Cut528
  Tool = -> Cylinder329
FEATURE [Part::MultiFuse] Fusion329
  Shapes = -> [Cut529,Cut527]
FEATURE [Part::Mirroring] Part__Mirroring063  label="Fusion008 (Mirror #2)002"
  Base = (0,0,0)
  Normal = (0,1,0)
  Placement = pos=(0,170,0) rot=(0,0,1;0rad)
  Source = -> Fusion329
FEATURE [Part::MultiFuse] Fusion262
  Shapes = -> [Part__Mirroring063,Fusion260]
FEATURE [Part::Cut] Cut530  label="Cut823"
  Base = -> Box601
  Placement = pos=(0,0,2) rot=(0,0,1;0rad)
  Tool = -> Box602
FEATURE [Part::Cut] Cut531  label="Cut824"
  Base = -> Cut530
  Placement = pos=(0,0,-3) rot=(0,0,1;0rad)
  Tool = -> Fusion262
FEATURE [Part::Cut] Cut532  label="Cut825"
  Base = -> Cut520
  Tool = -> Cut531
FEATURE [Part::Box] Box611  label="Cube836"
  Height = 64
  Length = 21
  Width = 164
FEATURE [Part::Fillet] Fillet347
  Base = -> Box611
  Edges = 2 edges r=12: [Edge1,Edge3]
  Placement = pos=(3,3,0) rot=(0,0,1;0rad)
FEATURE [Part::Box] Box612  label="Cube837"
  Height = 59
  Length = 16
  Placement = pos=(15,0,0) rot=(0,0,1;0rad)
  Width = 170
FEATURE [Part::Box] Box613  label="Cube838"
  Height = 59
  Length = 21
  Placement = pos=(-13,3,0) rot=(0,0,1;0rad)
  Width = 164
FEATURE [Part::Box] Box614  label="Cube839"
  Height = 59
  Length = 21
  Placement = pos=(-13,0,0) rot=(0,0,1;0rad)
  Width = 170
FEATURE [Part::Fillet] Fillet348
  Base = -> Box614
  Edges = 2 edges r=15: [Edge1,Edge3]
FEATURE [Part::Fillet] Fillet349
  Base = -> Box613
  Edges = 2 edges r=12: [Edge1,Edge3]
  Placement = pos=(3,0,0) rot=(0,0,1;0rad)
FEATURE [Part::Cut] Cut533  label="Cut826"
  Base = -> Fillet348
  Placement = pos=(13,0,0) rot=(0,0,1;0rad)
  Tool = -> Fillet349
FEATURE [Part::Cut] Cut534  label="Cut827"
  Base = -> Cut533
  Tool = -> Box612
FEATURE [Part::Chamfer] Chamfer071
  Base = -> Cut532
  Edges = 4 edges r=2.5: [Edge1,Edge4,Edge5,Edge8]
FEATURE [Part::Chamfer] Chamfer072
  Base = -> Chamfer071
  Edges = 4 edges r=0.9: [Edge52,Edge80,Edge102,Edge110]
FEATURE [Part::Box] Box615  label="Cube840"
  Height = 25
  Length = 10
  Placement = pos=(150,40,0) rot=(0,0,1;0rad)
  Width = 100
FEATURE [Part::Box] Box616  label="Cube841"
  Height = 40
  Length = 10
  Placement = pos=(150,19,0) rot=(-1,0,0;0.383972rad)
  Width = 20
FEATURE [Part::Box] Box617  label="Cube842"
  Height = 40
  Length = 10
  Placement = pos=(150,19,0) rot=(-1,0,0;0.383972rad)
  Width = 20
FEATURE [Part::Mirroring] Part__Mirroring064  label="Cube088 (Mirror #13)002"
  Base = (0,0,0)
  Normal = (0,1,0)
  Placement = pos=(0,180,0) rot=(0,0,1;0rad)
  Source = -> Box617
FEATURE [Part::MultiFuse] Fusion330
  Shapes = -> [Box616,Part__Mirroring064]
FEATURE [Part::Cut] Cut535  label="Cut828"
  Base = -> Box615
  Placement = pos=(-30,-5,20) rot=(0,0,1;0rad)
  Tool = -> Fusion330
FEATURE [Part::Fillet] Fillet350
  Base = -> Cut535
  Edges = 2 edges r=6: [Edge5,Edge6]
FEATURE [Part::Cylinder] Cylinder330
  Angle = 360
  Height = 134
  Radius = 3.7
FEATURE [Part::Fillet] Fillet351
  Base = -> Cylinder330
  Edges = 2 edges r=2: [Edge1,Edge3]
  Placement = pos=(128,152,53) rot=(1,0,0;1.5708rad)
FEATURE [Part::Box] Box618  label="Cube843"
  Height = 9
  Length = 14
  Width = 2
FEATURE [Part::Fillet] Fillet352
  Base = -> Box618
  Edges = 4 edges r=2: [Edge2,Edge4,Edge6,Edge8]
  Placement = pos=(68.5,0,46.5) rot=(0,0,1;0rad)
FEATURE [Part::Box] Box619  label="Cube844"
  Height = 9
  Length = 14
  Width = 2
FEATURE [Part::Fillet] Fillet353
  Base = -> Box619
  Edges = 4 edges r=2: [Edge2,Edge4,Edge6,Edge8]
  Placement = pos=(68.5,168,46.5) rot=(0,0,1;0rad)
FEATURE [Part::MultiFuse] Fusion331
  Placement = pos=(-4,0,-13) rot=(0,0,1;0rad)
  Shapes = -> [Fillet353,Fillet352]
FEATURE [Part::Box] Box620  label="Cube845"
  Height = 116
  Length = 67
  Placement = pos=(-53.2,0,65) rot=(0,1,0;0.218166rad)
  Width = 10
FEATURE [Part::Box] Box621  label="Cube846"
  Height = 116
  Length = 67
  Placement = pos=(-53.7,0,65) rot=(0,1,0;0.218166rad)
  Width = 10
FEATURE [Part::Box] Box622  label="Cube847"
  Height = 117
  Length = 67.5
  Placement = pos=(14,0,-1) rot=(0,0,1;0rad)
  Width = 10
FEATURE [Part::Cut] Cut537  label="Cut829"
  Base = -> Box622
  Placement = pos=(0,-2,0) rot=(0,0,1;0rad)
  Tool = -> Box621
FEATURE [Part::Box] Box623  label="Cube848"
  Height = 116
  Length = 66.5
  Placement = pos=(14.5,0,-0.5) rot=(0,0,1;0rad)
  Width = 10
FEATURE [Part::Cut] Cut538  label="Cut830"
  Base = -> Box623
  Placement = pos=(0,-2,0) rot=(0,0,1;0rad)
  Tool = -> Box620
FEATURE [Part::Cut] Cut536  label="doors-cut-005"
  Base = -> Cut537
  Placement = pos=(1.5,-3,0.5) rot=(0,0,1;0rad)
  Tool = -> Cut538
FEATURE [Part::Box] Box624  label="Cube849"
  Height = 64
  Length = 21
  Width = 164
FEATURE [Part::Fillet] Fillet354
  Base = -> Box624
  Edges = 2 edges r=18: [Edge1,Edge3]
  Placement = pos=(7,3,0) rot=(0,0,1;0rad)
FEATURE [Part::Cut] Cut539  label="Cut831"
  Base = -> Fillet347
  Tool = -> Fillet354
FEATURE [Part::MultiFuse] Fusion265
  Shapes = -> [Chamfer072,Cut539]
FEATURE [Part::Cut] Cut540  label="Cut832"
  Base = -> Fusion265
  Tool = -> Cut534
FEATURE [Part::Cut] Cut541  label="Cut833"
  Base = -> Cut540
  Tool = -> Fillet351
FEATURE [Part::Cut] Cut542  label="Cut834"
  Base = -> Cut541
  Tool = -> Fillet350
FEATURE [Part::Cut] Cut543  label="Cut835"
  Base = -> Cut542
  Tool = -> Fusion331
FEATURE [Part::Fillet] Fillet355
  Base = -> Cut543
  Edges = 2 edges r=3: [Edge74,Edge149]
FEATURE [Part::Box] Box456  label="Cube681"
  Height = 2
  Length = 117
  Placement = pos=(6,3,54) rot=(0,0,1;0rad)
  Width = 164
FEATURE [Part::Fillet] Fillet451
  Base = -> Box456
  Edges = 2 edges r=15: [Edge1,Edge3]
FEATURE [Part::Fillet] Fillet452
  Base = -> Fillet451
  Edges = 2 edges r=6: [Edge17,Edge18]
FEATURE [Part::Box] Box457  label="Cube682"
  Height = 2
  Length = 111
  Placement = pos=(6,3,54) rot=(0,0,1;0rad)
  Width = 158
FEATURE [Part::Fillet] Fillet359
  Base = -> Box457
  Edges = 2 edges r=12: [Edge1,Edge3]
FEATURE [Part::Fillet] Fillet358
  Base = -> Fillet359
  Edges = 2 edges r=3: [Edge17,Edge18]
  Placement = pos=(3,3,0) rot=(0,0,1;0rad)
FEATURE [Part::Cut] Cut544  label="Cut836"
  Base = -> Fillet452
  Placement = pos=(0,0,8) rot=(0,0,1;0rad)
  Tool = -> Fillet358
FEATURE [Part::MultiFuse] Fusion332
  Shapes = -> [Cut544,Fillet355]
FEATURE [Part::Cut] Cut545  label="Cut837"
  Base = -> Cut536
  Placement = pos=(-1,0,0) rot=(0,0,1;0rad)
  Tool = -> Fusion332
FEATURE [Part::Box] Box625  label="Cube850"
  Height = 53
  Length = 67.5
  Placement = pos=(14.5,-5,64) rot=(0,0,1;0rad)
  Width = 10
FEATURE [Part::Cut] Cut546  label="Cut838"
  Base = -> Cut545
  Placement = pos=(0,0.75,0) rot=(0,0,1;0rad)
  Tool = -> Box625
FEATURE [Part::Mirroring] Part__Mirroring065  label="Cut674 (Mirror #17)"
  Base = (0,0,0)
  Normal = (0,1,0)
  Placement = pos=(0,170,0) rot=(0,0,1;0rad)
  Source = -> Cut546
FEATURE [Part::MultiFuse] Fusion333
  Shapes = -> [Part__Mirroring065,Cut519]
FEATURE [Part::Cut] Cut547  label="Cut839"
  Base = -> Fusion328
  Tool = -> Fusion316
FEATURE [Part::MultiFuse] Fusion268
  Shapes = -> [Cut547,Chamfer068]
FEATURE [Part::Cut] Cut548  label="Cut840"
  Base = -> Fusion268
  Tool = -> Fusion317
FEATURE [Part::Cut] Cut549  label="Cut841"
  Base = -> Cut548
  Tool = -> Fusion318
FEATURE [Part::MultiFuse] Fusion269
  Shapes = -> [Cut549,Part__Mirroring060,Chamfer069]
FEATURE [Part::Cut] Cut550  label="Cut842"
  Base = -> Fusion269
  Tool = -> Fusion324
FEATURE [Part::Cut] Cut551  label="Cut843"
  Base = -> Cut550
  Tool = -> Fusion333
FEATURE [Part::Chamfer] Chamfer073
  Base = -> Cut551
  Edges = 1 edges r=0.9: [Edge349]
FEATURE [Part::Fillet] Fillet360
  Base = -> Chamfer073
  Edges = 2 edges r=4: [Edge145,Edge282]
FEATURE [Part::Fillet] Fillet361
  Base = -> Fillet360
  Edges = 10 edges r=0.5: [Edge150,Edge164,Edge165,Edge279,Edge281,Edge289,Edge291,Edge301,Edge361,Edge362]
FEATURE [Part::Fillet] Fillet362
  Base = -> Fillet361
  Edges = 2 edges r=0.49: [Edge141,Edge160]
FEATURE [Part::Cylinder] Cylinder331
  Angle = 360
  Height = 11.5
  Placement = pos=(12,10.7,16) rot=(0.881271,-0.370227,-0.293757;1.67552rad)
  Radius = 1.2
FEATURE [Part::Cylinder] Cylinder332
  Angle = 360
  Height = 11.5
  Placement = pos=(12,10.7,51) rot=(0.881271,-0.370227,-0.293757;1.67552rad)
  Radius = 1.2
FEATURE [Part::MultiFuse] Fusion334
  Shapes = -> [Cylinder331,Cylinder332]
FEATURE [Part::Cylinder] Cylinder333
  Angle = 360
  Height = 11.5
  Placement = pos=(12,10.7,16) rot=(0.881271,-0.370227,-0.293757;1.67552rad)
  Radius = 1.2
FEATURE [Part::Cylinder] Cylinder334
  Angle = 360
  Height = 11.5
  Placement = pos=(12,10.7,51) rot=(0.881271,-0.370227,-0.293757;1.67552rad)
  Radius = 1.2
FEATURE [Part::MultiFuse] Fusion274
  Shapes = -> [Cylinder333,Cylinder334]
FEATURE [Part::Mirroring] Part__Mirroring066  label="Fusion274 (Mirror #18)"
  Base = (0,0,0)
  Normal = (0,1,0)
  Placement = pos=(0,170,0) rot=(0,0,1;0rad)
  Source = -> Fusion274
FEATURE [Part::MultiFuse] Fusion275
  Shapes = -> [Fusion334,Part__Mirroring066]
FEATURE [Part::Cut] Cut552  label="cab-lower-part-06"
  Base = -> Fillet362
  Placement = pos=(0,0,8) rot=(0,0,1;0rad)
  Tool = -> Fusion275
FEATURE [Part::Box] Box628  label="Cube853"
  Height = 5.8
  Length = 13.6
  Placement = pos=(91.2,163,27) rot=(0,0,1;0rad)
  Width = 4
FEATURE [Part::Box] Box634  label="Cube859"
  Height = 7
  Length = 10
  Placement = pos=(46,152,-30) rot=(0,0,1;0rad)
  Width = 25
FEATURE [Part::Cylinder] Cylinder367
  Angle = 360
  Height = 25
  Placement = pos=(98,177,-23) rot=(0.799251,-0.424969,0.424969;1.79303rad)
  Radius = 52
FEATURE [Part::Cylinder] Cylinder368
  Angle = 360
  Height = 28
  Placement = pos=(98,175,-23) rot=(0.799251,-0.424969,0.424969;1.79303rad)
  Radius = 50
FEATURE [Part::Cylinder] Cylinder369
  Angle = 360
  Height = 30
  Placement = pos=(98,177,-30) rot=(0.799251,-0.424969,0.424969;1.79303rad)
  Radius = 48
FEATURE [Part::MultiFuse] Fusion349
  Shapes = -> [Box634,Cylinder367]
FEATURE [Part::Box] Box635  label="Cube860"
  Height = 7
  Length = 10
  Placement = pos=(48,147,-30) rot=(0,0,1;0rad)
  Width = 28
FEATURE [Part::Cut] Cut569  label="Cut861"
  Base = -> Fusion349
  Tool = -> Cylinder368
FEATURE [Part::Cut] Cut570  label="Cut862"
  Base = -> Cut569
  Tool = -> Cylinder369
FEATURE [Part::Cut] Cut571  label="Cut863"
  Base = -> Cut570
  Tool = -> Box635
FEATURE [Part::Box] Box636  label="Cube861"
  Height = 7
  Length = 45
  Placement = pos=(76,175,14) rot=(0,0,1;0rad)
  Width = 2
FEATURE [Part::MultiFuse] Fusion350
  Shapes = -> [Cut571,Box636]
FEATURE [Part::Box] Box637  label="Cube862"
  Height = 14
  Length = 10
  Placement = pos=(116,168,12) rot=(0,1,0;0.401426rad)
  Width = 9
FEATURE [Part::Cut] Cut572  label="Cut864"
  Base = -> Fusion350
  Tool = -> Box637
FEATURE [Part::Box] Box638  label="Cube863"
  Height = 10
  Length = 10
  Placement = pos=(46,152,-31) rot=(0,1,0;0.785398rad)
  Width = 25
FEATURE [Part::Box] Box259  label="Cube485"
  Height = 5.8
  Length = 13.6
  Placement = pos=(91.2,163,27) rot=(0,0,1;0rad)
  Width = 4
FEATURE [Part::Box] Box265  label="Cube491"
  Height = 7
  Length = 10
  Placement = pos=(46,152,-30) rot=(0,0,1;0rad)
  Width = 25
FEATURE [Part::Cylinder] Cylinder257
  Angle = 360
  Height = 25
  Placement = pos=(98,177,-23) rot=(0.799251,-0.424969,0.424969;1.79303rad)
  Radius = 52
FEATURE [Part::Cylinder] Cylinder258
  Angle = 360
  Height = 28
  Placement = pos=(98,175,-23) rot=(0.799251,-0.424969,0.424969;1.79303rad)
  Radius = 50
FEATURE [Part::Cylinder] Cylinder259
  Angle = 360
  Height = 30
  Placement = pos=(98,177,-30) rot=(0.799251,-0.424969,0.424969;1.79303rad)
  Radius = 48
FEATURE [Part::MultiFuse] Fusion215
  Shapes = -> [Box265,Cylinder257]
FEATURE [Part::Box] Box266  label="Cube492"
  Height = 7
  Length = 10
  Placement = pos=(48,147,-30) rot=(0,0,1;0rad)
  Width = 28
FEATURE [Part::Cut] Cut595  label="Cut886"
  Base = -> Fusion215
  Tool = -> Cylinder258
FEATURE [Part::Cut] Cut596  label="Cut887"
  Base = -> Cut595
  Tool = -> Cylinder259
FEATURE [Part::Cut] Cut597  label="Cut888"
  Base = -> Cut596
  Tool = -> Box266
FEATURE [Part::Box] Box267  label="Cube493"
  Height = 7
  Length = 45
  Placement = pos=(76,175,14) rot=(0,0,1;0rad)
  Width = 2
FEATURE [Part::MultiFuse] Fusion216
  Shapes = -> [Cut597,Box267]
FEATURE [Part::Box] Box268  label="Cube494"
  Height = 14
  Length = 10
  Placement = pos=(116,168,12) rot=(0,1,0;0.401426rad)
  Width = 9
FEATURE [Part::Cut] Cut313
  Base = -> Fusion216
  Tool = -> Box268
FEATURE [Part::Box] Box269  label="Cube495"
  Height = 10
  Length = 10
  Placement = pos=(46,152,-31) rot=(0,1,0;0.785398rad)
  Width = 25
FEATURE [Part::MultiFuse] Fusion357
  Shapes = -> [Box628,Cut572]
FEATURE [Part::Cut] Cut601  label="Cut909"
  Base = -> Fusion357
  Tool = -> Box638
FEATURE [Part::Fillet] Fillet468  label="wing-right_"
  Base = -> Cut601
  Edges = 1 edges r=1: [Edge14]
FEATURE [Part::MultiFuse] Fusion358
  Shapes = -> [Box259,Cut313]
FEATURE [Part::Cut] Cut602  label="Cut910"
  Base = -> Fusion358
  Tool = -> Box269
FEATURE [Part::Fillet] Fillet469
  Base = -> Cut602
  Edges = 1 edges r=1: [Edge14]
FEATURE [Part::Mirroring] Part__Mirroring082  label="wing-left_"
  Base = (0,0,0)
  Normal = (0,1,0)
  Placement = pos=(0,170,0) rot=(0,0,1;0rad)
  Source = -> Fillet469
FEATURE [Part::Box] Box663  label="Cube888"
  Height = 14
  Length = 10
  Placement = pos=(116,169,12) rot=(0,1,0;0.401426rad)
  Width = 9
FEATURE [Part::Box] Box664  label="Cube889"
  Height = 12
  Length = 11
  Placement = pos=(46,153,-31) rot=(0,1,0;0.785398rad)
  Width = 25
FEATURE [Part::Cylinder] Cylinder377
  Angle = 124
  Height = 1
  Placement = pos=(98,177,-30) rot=(0,0.707107,0.707107;3.14159rad)
  Radius = 49
FEATURE [Part::Cylinder] Cylinder378
  Angle = 360
  Height = 1
  Placement = pos=(98,177,-30) rot=(-1,0,0;1.5708rad)
  Radius = 48
FEATURE [Part::MultiFuse] Fusion359
  Shapes = -> [Box664,Box663]
FEATURE [Part::Cut] Cut603  label="Cut911"
  Base = -> Cylinder377
  Tool = -> Cylinder378
FEATURE [Part::Cut] Cut604  label="Cut912"
  Base = -> Cut603
  Tool = -> Fusion359
FEATURE [Part::Fillet] Fillet470
  Base = -> Cut604
  Edges = 2 edges r=0.499: [Edge1,Edge6]
  Placement = pos=(0,-0.5,0) rot=(0,0,1;0rad)
FEATURE [Part::Box] Box665  label="Cube890"
  Height = 14
  Length = 10
  Placement = pos=(116,169,12) rot=(0,1,0;0.401426rad)
  Width = 9
FEATURE [Part::Box] Box666  label="Cube891"
  Height = 12
  Length = 11
  Placement = pos=(46,153,-31) rot=(0,1,0;0.785398rad)
  Width = 25
FEATURE [Part::Cylinder] Cylinder379
  Angle = 124
  Height = 1
  Placement = pos=(98,177,-30) rot=(0,0.707107,0.707107;3.14159rad)
  Radius = 49
FEATURE [Part::Cylinder] Cylinder380
  Angle = 360
  Height = 1
  Placement = pos=(98,177,-30) rot=(-1,0,0;1.5708rad)
  Radius = 48
FEATURE [Part::MultiFuse] Fusion360
  Shapes = -> [Box666,Box665]
FEATURE [Part::Cut] Cut605  label="Cut915"
  Base = -> Cylinder379
  Tool = -> Cylinder380
FEATURE [Part::Cut] Cut606  label="Cut916"
  Base = -> Cut605
  Tool = -> Fusion360
FEATURE [Part::Fillet] Fillet471
  Base = -> Cut606
  Edges = 2 edges r=0.499: [Edge1,Edge6]
  Placement = pos=(0,-0.5,0) rot=(0,0,1;0rad)
FEATURE [Part::Mirroring] Part__Mirroring083  label="Fillet471 (Mirror #65)"
  Base = (0,0,0)
  Normal = (0,1,0)
  Placement = pos=(0,170,0) rot=(0,0,1;0rad)
  Source = -> Fillet471
FEATURE [Part::MultiFuse] Fusion361  label="wing-right"
  Placement = pos=(0,0,8) rot=(0,0,1;0rad)
  Shapes = -> [Fillet468,Fillet470]
FEATURE [Part::MultiFuse] Fusion362  label="wing-left"
  Placement = pos=(0,0,8) rot=(0,0,1;0rad)
  Shapes = -> [Part__Mirroring082,Part__Mirroring083]
FEATURE [Part::Cylinder] Cylinder381
  Angle = 66.75
  Height = 1
  Placement = pos=(99,178,-31) rot=(1,0,0;1.5708rad)
  Radius = 48
FEATURE [Part::Cylinder] Cylinder382
  Angle = 66.75
  Height = 1
  Placement = pos=(99,178,-31) rot=(1,0,0;1.5708rad)
  Radius = 49
FEATURE [Part::Cut] Cut607  label="Cut917"
  Base = -> Cylinder382
  Tool = -> Cylinder381
FEATURE [Part::Fillet] Fillet472
  Base = -> Cut607
  Edges = 2 edges r=0.499: [Edge3,Edge11]
  Placement = pos=(0,-0.5,0) rot=(0,0,1;0rad)
FEATURE [Part::Cylinder] Cylinder383
  Angle = 66.75
  Height = 1
  Placement = pos=(99,178,-31) rot=(1,0,0;1.5708rad)
  Radius = 48
FEATURE [Part::Cylinder] Cylinder384
  Angle = 66.75
  Height = 1
  Placement = pos=(99,178,-31) rot=(1,0,0;1.5708rad)
  Radius = 49
FEATURE [Part::Cut] Cut608  label="Cut918"
  Base = -> Cylinder384
  Tool = -> Cylinder383
FEATURE [Part::Fillet] Fillet473
  Base = -> Cut608
  Edges = 2 edges r=0.499: [Edge3,Edge11]
  Placement = pos=(0,-0.5,0) rot=(0,0,1;0rad)
FEATURE [Part::Mirroring] Part__Mirroring084  label="Fillet473 (Mirror #66)"
  Base = (0,0,0)
  Normal = (0,1,0)
  Placement = pos=(0,170,0) rot=(0,0,1;0rad)
  Source = -> Fillet473
FEATURE [Part::MultiFuse] Fusion363  label="wing-right-rear"
  Placement = pos=(0,0,8) rot=(0,0,1;0rad)
  Shapes = -> [Fusion138,Fillet472]
FEATURE [Part::MultiFuse] Fusion364  label="wing-left-rear"
  Placement = pos=(0,0,8) rot=(0,0,1;0rad)
  Shapes = -> [Part__Mirroring018,Part__Mirroring084]
FEATURE [Part::Box] Box416  label="Cube641"
  Height = 20
  Length = 490
  Placement = pos=(0,0,-92) rot=(0,0,1;0rad)
  Width = 11.5
FEATURE [Part::Box] Box417  label="Cube642"
  Height = 17
  Length = 490
  Placement = pos=(0,1.5,-90.5) rot=(0,0,1;0rad)
  Width = 10
FEATURE [Part::Cut] Cut429  label="Cut919"
  Base = -> Box416
  Tool = -> Box417
FEATURE [Part::Fillet] Fillet268
  Base = -> Cut429
  Edges = 2 edges r=3: [Edge11,Edge23]
  Placement = pos=(0,-1.5,0) rot=(0,0,1;0rad)
FEATURE [Part::Box] Box418  label="Cube643"
  Height = 20
  Length = 490
  Placement = pos=(0,0,-92) rot=(0,0,1;0rad)
  Width = 11.5
FEATURE [Part::Box] Box419  label="Cube644"
  Height = 17
  Length = 490
  Placement = pos=(0,1.5,-90.5) rot=(0,0,1;0rad)
  Width = 10
FEATURE [Part::Cut] Cut430  label="Cut920"
  Base = -> Box418
  Tool = -> Box419
FEATURE [Part::Fillet] Fillet269
  Base = -> Cut430
  Edges = 2 edges r=3: [Edge11,Edge23]
FEATURE [Part::Mirroring] Part__Mirroring036  label="Fillet269 (Mirror #29)"
  Base = (0,0,0)
  Normal = (0,1,0)
  Placement = pos=(0,61.5,0) rot=(0,0,1;0rad)
  Source = -> Fillet269
FEATURE [Part::MultiFuse] Fusion231  label="frame-00"
  Placement = pos=(23.5,55,74) rot=(0,0,1;0rad)
  Shapes = -> [Part__Mirroring036,Fillet268]
FEATURE [Part::Cylinder] Cylinder1033  label="Cylinder1484"
  Angle = 360
  Height = 39.5
  Placement = pos=(0,0,23) rot=(0,1,0;1.5708rad)
  Radius = 13
FEATURE [Part::Cylinder] Cylinder1034  label="Cylinder1485"
  Angle = 360
  Height = 39.5
  Placement = pos=(0,0,0) rot=(0,1,0;1.5708rad)
  Radius = 19.5
FEATURE [Part::Cylinder] Cylinder798  label="main-motor"
  Angle = 360
  Height = 50
  Placement = pos=(31,89,23) rot=(0,1,0;1.5708rad)
  Radius = 18
FEATURE [Part::MultiFuse] Fusion248002002  label="gearbox002"
  Placement = pos=(89,84.9373,3.51066) rot=(1,0,0;0.706858rad)
  Shapes = -> [Cylinder1033,Cylinder1034]
FEATURE [Part::Box] Box659  label="Cube892"
  Height = 41
  Length = 47.5
  Placement = pos=(81,65,-17) rot=(0,0,1;0rad)
  Width = 40
FEATURE [Part::Cylinder] Cylinder801  label="main-motor001"
  Angle = 360
  Height = 18
  Placement = pos=(81,89,21) rot=(0,1,0;1.5708rad)
  Radius = 18
FEATURE [Part::Cylinder] Cylinder802  label="Cylinder1486"
  Angle = 360
  Height = 47.5
  Placement = pos=(81,70,21) rot=(0,1,0;1.5708rad)
  Radius = 17.5
FEATURE [Part::Box] Box660  label="Cube851"
  Height = 22
  Length = 47.5
  Placement = pos=(81,105,2) rot=(0,0,1;0rad)
  Width = 7
FEATURE [Part::MultiFuse] Fusion591
  Shapes = -> [Box660,Cylinder802,Box659,Cylinder801]
FEATURE [Part::Cylinder] Cylinder805  label="Cylinder1487"
  Angle = 360
  Height = 10
  Placement = pos=(89,70,21) rot=(0,1,0;1.5708rad)
  Radius = 16.5
FEATURE [Part::MultiFuse] Fusion592
  Shapes = -> [Fusion248002002,Cylinder805]
FEATURE [Part::Cut] Cut014193  label="Cut014390"
  Base = -> Fusion591
  Tool = -> Fusion592
FEATURE [Part::Chamfer] Chamfer125
  Base = -> Cut014193
  Edges = 1 edges r=3.49: [Edge39]
FEATURE [Part::Fillet] Fillet007002
  Base = -> Chamfer125
  Edges = 1 edges r=3: [Edge25]
FEATURE [Part::Fillet] Fillet007003
  Base = -> Fillet007002
  Edges = 2 edges r=6: [Edge13,Edge18]
FEATURE [Part::Box] Box500  label="Cube702"
  Height = 20
  Length = 60
  Placement = pos=(81,53.25,-18) rot=(0,0,1;0rad)
  Width = 63.5
FEATURE [Part::Feature] Face052
  shape: bbox 2.621e-05 x 37.61 x 40.07 mm, 1 faces, 0 solids (baked)
FEATURE [Part::Extrusion] Extrude013
  Base = -> Face052
  Dir = (60,0,0)
  Placement = pos=(-30.4,1.43133,-5.60163) rot=(1,0,0;0.069813rad)
  Solid = false
FEATURE [Part::Cylinder] Cylinder806  label="Cylinder1488"
  Angle = 360
  Height = 60
  Placement = pos=(81,106.419,11.8645) rot=(0.034878,0.998783,0.034878;1.57201rad)
  Radius = 3.1
FEATURE [Part::Cut] Cut014049
  Base = -> Fillet007003
  Tool = -> Extrude013
FEATURE [Part::Cut] Cut014050
  Base = -> Cut014049
  Tool = -> Cylinder806
FEATURE [Part::Cylinder] Cylinder807  label="Cylinder000"
  Angle = 360
  Height = 50
  Placement = pos=(45,89,21) rot=(0,1,0;1.5708rad)
  Radius = 7
FEATURE [Part::Cut] Cut014051
  Base = -> Cut014050
  Tool = -> Cylinder807
FEATURE [Part::Chamfer] Chamfer126
  Base = -> Cut014051
  Edges = 1 edges r=5.2: [Edge52]
FEATURE [Part::Cylinder] Cylinder808  label="Cylinder1489"
  Angle = 360
  Height = 50
  Placement = pos=(56,89,33.5) rot=(0,1,0;1.5708rad)
  Radius = 1.6
FEATURE [Part::Cylinder] Cylinder809  label="Cylinder958"
  Angle = 360
  Height = 50
  Placement = pos=(56,89,8.5) rot=(0,1,0;1.5708rad)
  Radius = 1.6
FEATURE [Part::MultiFuse] Fusion593
  Placement = pos=(0,14.7618,74.3919) rot=(-1,0,0;0.855211rad)
  Shapes = -> [Cylinder808,Cylinder809]
FEATURE [Part::Cylinder] Cylinder810  label="Cylinder959"
  Angle = 360
  Height = 15
  Placement = pos=(56,89,33.5) rot=(0,1,0;1.5708rad)
  Radius = 3.1
FEATURE [Part::Cylinder] Cylinder811  label="Cylinder960"
  Angle = 360
  Height = 15
  Placement = pos=(56,89,8.5) rot=(0,1,0;1.5708rad)
  Radius = 3.1
FEATURE [Part::MultiFuse] Fusion594
  Placement = pos=(28,14.7618,74.3919) rot=(-1,0,0;0.855211rad)
  Shapes = -> [Cylinder810,Cylinder811]
FEATURE [Part::MultiFuse] Fusion595
  Shapes = -> [Fusion593,Fusion594]
FEATURE [Part::Cut] Cut014052
  Base = -> Chamfer126
  Tool = -> Fusion595
FEATURE [Part::Cylinder] Cylinder812  label="Cylinder1490"
  Angle = 360
  Height = 60
  Placement = pos=(81,85,3.5) rot=(0,1,0;1.5708rad)
  Radius = 5.6
FEATURE [Part::Cylinder] Cylinder813  label="Cylinder1491"
  Angle = 360
  Height = 60
  Placement = pos=(81,70,21) rot=(0,1,0;1.5708rad)
  Radius = 5.6
FEATURE [Part::MultiFuse] Fusion248002003  label="Fusion248002197"
  Placement = pos=(4,0,0) rot=(0,0,1;0rad)
  Shapes = -> [Cylinder812,Cylinder813]
FEATURE [Part::Cylinder] Cylinder814  label="Cylinder1492"
  Angle = 360
  Height = 60
  Placement = pos=(81,85,3.5) rot=(0,1,0;1.5708rad)
  Radius = 4
FEATURE [Part::Cylinder] Cylinder815  label="Cylinder1493"
  Angle = 360
  Height = 60
  Placement = pos=(81,70,21) rot=(0,1,0;1.5708rad)
  Radius = 4
FEATURE [Part::MultiFuse] Fusion248002004
  Shapes = -> [Cylinder814,Cylinder815]
FEATURE [Part::MultiFuse] Fusion248002005
  Shapes = -> [Fusion248002003,Fusion248002004]
FEATURE [Part::Cut] Cut014053
  Base = -> Cut014052
  Tool = -> Fusion248002005
FEATURE [Part::Cylinder] Cylinder816  label="Cylinder1494"
  Angle = 360
  Height = 20
  Placement = pos=(81,69,-13) rot=(0,1,0;1.5708rad)
  Radius = 1.25
FEATURE [Part::Cylinder] Cylinder817  label="Cylinder1495"
  Angle = 360
  Height = 20
  Placement = pos=(81,101,-13) rot=(0,1,0;1.5708rad)
  Radius = 1.25
FEATURE [Part::Cylinder] Cylinder818  label="Cylinder1496"
  Angle = 360
  Height = 20
  Placement = pos=(81,101,21) rot=(0,1,0;1.5708rad)
  Radius = 1.25
FEATURE [Part::Cylinder] Cylinder819  label="Cylinder1497"
  Angle = 360
  Height = 20
  Placement = pos=(81,70,36) rot=(0,1,0;1.5708rad)
  Radius = 1.25
FEATURE [Part::Cylinder] Cylinder820  label="Cylinder1498"
  Angle = 360
  Height = 20
  Placement = pos=(81,56,26) rot=(0,1,0;1.5708rad)
  Radius = 1.25
FEATURE [Part::Cylinder] Cylinder821  label="Cylinder1499"
  Angle = 360
  Height = 20
  Placement = pos=(81,62,8) rot=(0,1,0;1.5708rad)
  Radius = 1.25
FEATURE [Part::MultiFuse] Fusion248002006
  Placement = pos=(28,0,0) rot=(0,0,1;0rad)
  Shapes = -> [Cylinder816,Cylinder820,Cylinder821,Cylinder817,Cylinder818,Cylinder819]
FEATURE [Part::Cut] Cut014054
  Base = -> Cut014053
  Placement = pos=(0,0,2) rot=(0,0,1;0rad)
  Tool = -> Fusion248002006
FEATURE [Part::Box] Box501  label="Cube703"
  Height = 22
  Length = 44
  Placement = pos=(81,51,-15) rot=(0,0,1;0rad)
  Width = 14
FEATURE [Part::Fillet] Fillet007004
  Base = -> Box500
  Edges = 2 edges r=3: [Edge10,Edge12]
FEATURE [Part::Box] Box502  label="Cube704"
  Height = 22
  Length = 44
  Placement = pos=(81,105,-15) rot=(0,0,1;0rad)
  Width = 14
FEATURE [Part::Cylinder] Cylinder822  label="Cylinder961"
  Angle = 360
  Height = 5
  Placement = pos=(120,125,-8) rot=(1,0,0;1.5708rad)
  Radius = 1.6
FEATURE [Part::Cylinder] Cylinder823  label="Cylinder962"
  Angle = 360
  Height = 5
  Placement = pos=(86,125,-8) rot=(1,0,0;1.5708rad)
  Radius = 1.6
FEATURE [Part::MultiFuse] Fusion248002007
  Placement = pos=(0,-5,0) rot=(0,0,1;0rad)
  Shapes = -> [Cylinder823,Cylinder822]
FEATURE [Part::Cylinder] Cylinder824  label="Cylinder963"
  Angle = 360
  Height = 5
  Placement = pos=(120,125,-8) rot=(1,0,0;1.5708rad)
  Radius = 1.6
FEATURE [Part::Cylinder] Cylinder825  label="Cylinder964"
  Angle = 360
  Height = 5
  Placement = pos=(86,125,-8) rot=(1,0,0;1.5708rad)
  Radius = 1.6
FEATURE [Part::MultiFuse] Fusion248002008
  Placement = pos=(0,-70,0) rot=(0,0,1;0rad)
  Shapes = -> [Cylinder825,Cylinder824]
FEATURE [Part::MultiFuse] Fusion248002009
  Shapes = -> [Fusion248002007,Fusion248002008]
FEATURE [Part::Feature] Face044
  shape: bbox 2e-07 x 80.32 x 83.91 mm, 1 faces, 0 solids (baked)
FEATURE [Part::Extrusion] Extrude014
  Base = -> Face044
  Dir = (5,0,0)
  Solid = false
FEATURE [Part::Cylinder] Cylinder826
  Angle = 360
  Height = 60
  Placement = pos=(81,85,3.5) rot=(0,1,0;1.5708rad)
  Radius = 4
FEATURE [Part::Cylinder] Cylinder827
  Angle = 360
  Height = 60
  Placement = pos=(81,70,21) rot=(0,1,0;1.5708rad)
  Radius = 4
FEATURE [Part::MultiFuse] Fusion248002010
  Shapes = -> [Cylinder826,Cylinder827]
FEATURE [Part::Cylinder] Cylinder828
  Angle = 360
  Height = 60
  Placement = pos=(81,85,3.5) rot=(0,1,0;1.5708rad)
  Radius = 5.6
FEATURE [Part::Cylinder] Cylinder829
  Angle = 360
  Height = 60
  Placement = pos=(81,70,21) rot=(0,1,0;1.5708rad)
  Radius = 5.6
FEATURE [Part::MultiFuse] Fusion248002011
  Placement = pos=(-8.5,0,0) rot=(0,0,1;0rad)
  Shapes = -> [Cylinder828,Cylinder829]
FEATURE [Part::MultiFuse] Fusion608
  Shapes = -> [Fusion248002011,Fusion248002010]
FEATURE [Part::Cut] Cut014057
  Base = -> Extrude014
  Tool = -> Fusion608
FEATURE [Part::Cylinder] Cylinder830
  Angle = 360
  Height = 60
  Placement = pos=(81,106.419,11.8645) rot=(0.034878,0.998783,0.034878;1.57201rad)
  Radius = 3.1
FEATURE [Part::Cut] Cut014058
  Base = -> Cut014057
  Tool = -> Cylinder830
FEATURE [Part::Cylinder] Cylinder831
  Angle = 360
  Height = 20
  Placement = pos=(81,69,-13) rot=(0,1,0;1.5708rad)
  Radius = 1.6
FEATURE [Part::Cylinder] Cylinder832  label="Cylinder1500"
  Angle = 360
  Height = 20
  Placement = pos=(81,101,-13) rot=(0,1,0;1.5708rad)
  Radius = 1.6
FEATURE [Part::Cylinder] Cylinder833  label="Cylinder1501"
  Angle = 360
  Height = 20
  Placement = pos=(81,101,21) rot=(0,1,0;1.5708rad)
  Radius = 1.6
FEATURE [Part::Cylinder] Cylinder834  label="Cylinder1502"
  Angle = 360
  Height = 20
  Placement = pos=(81,70,36) rot=(0,1,0;1.5708rad)
  Radius = 1.6
FEATURE [Part::Cylinder] Cylinder835  label="Cylinder1503"
  Angle = 360
  Height = 20
  Placement = pos=(81,56,26) rot=(0,1,0;1.5708rad)
  Radius = 1.6
FEATURE [Part::Cylinder] Cylinder836  label="Cylinder1504"
  Angle = 360
  Height = 20
  Placement = pos=(81,62,8) rot=(0,1,0;1.5708rad)
  Radius = 1.6
FEATURE [Part::MultiFuse] Fusion609
  Placement = pos=(40,0,2) rot=(0,0,1;0rad)
  Shapes = -> [Cylinder831,Cylinder835,Cylinder836,Cylinder832,Cylinder833,Cylinder834]
FEATURE [Part::Box] Box504  label="Cube706"
  Height = 10
  Length = 30
  Placement = pos=(81,111,5) rot=(0,0,1;0rad)
  Width = 5.5
FEATURE [Part::Chamfer] Chamfer127
  Base = -> Box502
  Edges = 1 edges r=2: [Edge10]
FEATURE [Part::MultiFuse] Fusion611
  Shapes = -> [Box501,Chamfer127]
FEATURE [Part::Cut] Cut014194  label="Cut014391"
  Base = -> Fusion611
  Tool = -> Fillet007004
FEATURE [Part::MultiFuse] Fusion612
  Shapes = -> [Cut014054,Cut014194]
FEATURE [Part::Fillet] Fillet007005
  Base = -> Fusion612
  Edges = 1 edges r=4: [Edge94]
FEATURE [Part::Fillet] Fillet007006
  Base = -> Fillet007005
  Edges = 2 edges r=4: [Edge124,Edge131]
FEATURE [Part::Chamfer] Chamfer111
  Base = -> Fillet007006
  Edges = 1 edges r=3: [Edge58]
FEATURE [Part::Fillet] Fillet007007
  Base = -> Chamfer111
  Edges = 1 edges r=2: [Edge92]
FEATURE [Part::Fillet] Fillet007008
  Base = -> Cut014058
  Edges = 1 edges r=2: [Edge1]
FEATURE [Part::Fillet] Fillet007009
  Base = -> Fillet007008
  Edges = 1 edges r=3: [Edge41]
  Placement = pos=(0,0,2) rot=(0,0,1;0rad)
FEATURE [Part::Fillet] Fillet007010
  Base = -> Fillet007007
  Edges = 1 edges r=2.99: [Edge67]
FEATURE [Part::Cylinder] Cylinder837  label="Cylinder965"
  Angle = 360
  Height = 10
  Placement = pos=(96,125,-8) rot=(1,0,0;1.5708rad)
  Radius = 1.25
FEATURE [Part::Cylinder] Cylinder838  label="Cylinder966"
  Angle = 360
  Height = 10
  Placement = pos=(86,125,-8) rot=(1,0,0;1.5708rad)
  Radius = 1.25
FEATURE [Part::MultiFuse] Fusion613
  Placement = pos=(12,-3.5,20) rot=(0,0,1;0rad)
  Shapes = -> [Cylinder838,Cylinder837]
FEATURE [Part::Cylinder] Cylinder839  label="Cylinder967"
  Angle = 360
  Height = 8
  Placement = pos=(96,124,-8) rot=(1,0,0;1.5708rad)
  Radius = 1.25
FEATURE [Part::Cylinder] Cylinder840  label="Cylinder968"
  Angle = 360
  Height = 8
  Placement = pos=(86,120.5,-8) rot=(1,0,0;1.5708rad)
  Radius = 1.25
FEATURE [Part::Box] Box505  label="Cube707"
  Height = 10
  Length = 30
  Placement = pos=(95,53.5,5) rot=(0,0,1;0rad)
  Width = 7
FEATURE [Part::Chamfer] Chamfer112
  Base = -> Box505
  Edges = 1 edges r=6: [Edge12]
  Placement = pos=(-14,0,0) rot=(0,0,1;0rad)
FEATURE [Part::Fillet] Fillet007011
  Base = -> Box504
  Edges = 1 edges r=1: [Edge12]
FEATURE [Part::Fillet] Fillet007012
  Base = -> Chamfer112
  Edges = 1 edges r=0.99: [Edge7]
FEATURE [Part::MultiFuse] Fusion616
  Shapes = -> [Fillet007010,Fillet007012,Fillet007011]
FEATURE [Part::MultiFuse] Fusion614
  Placement = pos=(12,-64,20) rot=(0,0,1;0rad)
  Shapes = -> [Cylinder840,Cylinder839]
FEATURE [Part::MultiFuse] Fusion617
  Shapes = -> [Fusion613,Fusion614]
FEATURE [Part::MultiFuse] Fusion618
  Shapes = -> [Fusion248002009,Fusion617]
FEATURE [Part::Fillet] Fillet007013
  Base = -> Fusion616
  Edges = 2 edges r=6: [Edge81,Edge92]
FEATURE [Part::Box] Box506  label="Cube708"
  Height = 2
  Length = 39.5
  Placement = pos=(89,104,2) rot=(1,0,0;1.0821rad)
  Width = 10
FEATURE [Part::Box] Box507  label="Cube709"
  Height = 2
  Length = 39.5
  Placement = pos=(89,96,19) rot=(-1,0,0;0.314159rad)
  Width = 10
FEATURE [Part::MultiFuse] Fusion619
  Shapes = -> [Box507,Box506]
FEATURE [Part::Cut] Cut014062
  Base = -> Fillet007013
  Tool = -> Fusion619
FEATURE [Part::Cylinder] Cylinder841  label="Cylinder1505"
  Angle = 360
  Height = 19
  Placement = pos=(89,70,23) rot=(0,1,0;1.5708rad)
  Radius = 16.5
FEATURE [Part::Chamfer] Chamfer113
  Base = -> Cylinder841
  Edges = 1 edges r=4: [Edge1]
FEATURE [Part::Box] Box508  label="Cube710"
  Height = 32
  Length = 19
  Placement = pos=(89,70,7) rot=(0,0,1;0rad)
  Width = 32
FEATURE [Part::Chamfer] Chamfer114
  Base = -> Box508
  Edges = 2 edges r=4: [Edge6,Edge8]
  Placement = pos=(0,5.43898,58.5088) rot=(-1,0,0;0.820305rad)
FEATURE [Part::Chamfer] Chamfer115
  Base = -> Cut014062
  Edges = 1 edges r=5: [Edge65]
FEATURE [Part::MultiFuse] Fusion620
  Shapes = -> [Chamfer113,Chamfer114]
FEATURE [Part::Cut] Cut014063
  Base = -> Chamfer115
  Tool = -> Fusion620
FEATURE [Part::Cut] Cut014064  label="gearbox-front"
  Base = -> Cut014063
  Tool = -> Fusion618
FEATURE [Part::Chamfer] Chamfer116
  Base = -> Fillet007009
  Edges = 1 edges r=5: [Edge35]
FEATURE [Part::Cut] Cut014065  label="gearbox-rear"
  Base = -> Chamfer116
  Tool = -> Fusion609
FEATURE [Part::Cylinder] Cylinder1156  label="Cylinder1115"
  Angle = 360
  Height = 10
  Placement = pos=(3,60,10) rot=(1,0,0;1.5708rad)
  Radius = 1.2
FEATURE [Part::Cylinder] Cylinder1157  label="Cylinder1116"
  Angle = 360
  Height = 10
  Placement = pos=(3,10,10) rot=(1,0,0;1.5708rad)
  Radius = 1.2
FEATURE [Part::Box] Box736  label="Cube751"
  Height = 17
  Length = 16
  Placement = pos=(-2,0,1.5) rot=(0,0,1;0rad)
  Width = 60
FEATURE [Part::Box] Box737  label="Cube752"
  Height = 25.5
  Length = 10
  Placement = pos=(-12,0,-5) rot=(0,0,1;0rad)
  Width = 63
FEATURE [Part::Cylinder] Cylinder1158  label="Cylinder1117"
  Angle = 360
  Height = 11
  Placement = pos=(-2,66.5,4) rot=(0,1,0;1.5708rad)
  Radius = 1.25
FEATURE [Part::Cylinder] Cylinder955  label="Cylinder1118"
  Angle = 360
  Height = 11
  Placement = pos=(-2,13.5,4) rot=(0,1,0;1.5708rad)
  Radius = 1.25
FEATURE [Part::Cylinder] Cylinder956  label="Cylinder1119"
  Angle = 360
  Height = 15
  Placement = pos=(-2,57,20) rot=(0,1,0;1.5708rad)
  Radius = 1.25
FEATURE [Part::Cylinder] Cylinder957  label="Cylinder1120"
  Angle = 360
  Height = 15
  Placement = pos=(-2,23,20) rot=(0,1,0;1.5708rad)
  Radius = 1.25
FEATURE [Part::MultiFuse] Fusion248002101  label="Fusion248002271"
  Placement = pos=(-10,-10,1) rot=(0,0,1;0rad)
  Shapes = -> [Cylinder1158,Cylinder957,Cylinder955,Cylinder956]
FEATURE [Part::Fillet] Fillet007014
  Base = -> Box737
  Edges = 4 edges r=3: [Edge9,Edge10,Edge11,Edge12]
  Placement = pos=(25.5,53.5,-16.5) rot=(0,0,1;0rad)
FEATURE [Part::Fillet] Fillet007015
  Base = -> Box736
  Edges = 4 edges r=3: [Edge9,Edge10,Edge11,Edge12]
  Placement = pos=(25.5,55,-21) rot=(0,0,1;0rad)
FEATURE [Part::MultiFuse] Fusion600
  Placement = pos=(0,0,2) rot=(0,0,1;0rad)
  Shapes = -> [Cylinder1156,Cylinder1157]
FEATURE [Part::MultiFuse] Fusion248002102  label="Fusion248002272"
  Placement = pos=(25.5,55,-23) rot=(0,0,1;0rad)
  Shapes = -> [Fusion248002101,Fusion600]
FEATURE [Part::Box] Box738  label="Cube753"
  Height = 26
  Length = 41
  Placement = pos=(19.5,64.5,-21.5) rot=(0,0,1;0rad)
  Width = 41
FEATURE [Part::Cylinder] Cylinder1159  label="Cylinder1121"
  Angle = 360
  Height = 11
  Placement = pos=(37,64.5,-11) rot=(1,0,0;1.5708rad)
  Radius = 6
FEATURE [Part::Cylinder] Cylinder1160  label="Cylinder1122"
  Angle = 360
  Height = 10
  Placement = pos=(13.5,83,-11) rot=(0,1,0;1.5708rad)
  Radius = 1.6
FEATURE [Part::Cylinder] Cylinder1161  label="Cylinder1123"
  Angle = 360
  Height = 10
  Placement = pos=(13.5,91,-11) rot=(0,1,0;1.5708rad)
  Radius = 1.6
FEATURE [Part::Cylinder] Cylinder1162  label="Cylinder1124"
  Angle = 360
  Height = 2.5
  Placement = pos=(13.5,91,-11) rot=(0,1,0;1.5708rad)
  Radius = 3.1
FEATURE [Part::Cylinder] Cylinder1163  label="Cylinder1125"
  Angle = 360
  Height = 2.5
  Placement = pos=(13.5,83,-11) rot=(0,1,0;1.5708rad)
  Radius = 3.1
FEATURE [Part::Cylinder] Cylinder1164  label="Cylinder1126"
  Angle = 360
  Height = 5
  Placement = pos=(37,64.5,-11) rot=(1,0,0;1.5708rad)
  Radius = 7
FEATURE [Part::MultiFuse] Fusion248002103  label="Fusion248002273"
  Shapes = -> [Cylinder1162,Cylinder1160,Cylinder1161,Cylinder1163]
FEATURE [Part::Box] Box739  label="Cube754"
  Height = 17
  Length = 10
  Placement = pos=(37,55,-19.5) rot=(0,0,1;0rad)
  Width = 10
FEATURE [Part::MultiFuse] Fusion248002104  label="Fusion248002274"
  Shapes = -> [Box739,Box738,Cylinder1159,Cylinder1164]
FEATURE [Part::MultiFuse] Fusion248002105  label="Fusion248002275"
  Shapes = -> [Fillet007015,Fillet007014]
FEATURE [Part::Cut] Cut698  label="Cut014444"
  Base = -> Fusion248002105
  Tool = -> Fusion248002102
FEATURE [Part::Cut] Cut699  label="Cut014445"
  Base = -> Cut698
  Tool = -> Fusion248002104
FEATURE [Part::Cut] Cut700  label="cross-member-front"
  Base = -> Cut699
  Placement = pos=(0,0,3) rot=(0,0,1;0rad)
  Tool = -> Fusion248002103
FEATURE [Part::Box] Box740  label="Cube902"
  Height = 20
  Length = 25
  Placement = pos=(128,45.5,-18) rot=(0,0,1;0rad)
  Width = 8
FEATURE [Part::Cylinder] Cylinder1165  label="Cylinder1600"
  Angle = 360
  Height = 24.5
  Placement = pos=(144,53.5,2) rot=(1,0,0;1.5708rad)
  Radius = 3
FEATURE [Part::Cylinder] Cylinder1166  label="Cylinder1601"
  Angle = 360
  Height = 18
  Placement = pos=(131,51,-5) rot=(1,0,0;0.785398rad)
  Radius = 3
FEATURE [Part::Feature] Face059
  shape: bbox 7.785 x 2e-07 x 7.712 mm, 1 faces, 0 solids (baked)
FEATURE [Part::Feature] Face060
  shape: bbox 7.318 x 4.987 x 4.987 mm, 1 faces, 0 solids (baked)
FEATURE [Part::Loft] Loft023
  Closed = false
  Ruled = true
  Sections = -> [Face059,Face060]
  Solid = true
FEATURE [Part::Cylinder] Cylinder1167  label="Cylinder1602"
  Angle = 360
  Height = 3
  Placement = pos=(131,31,12) rot=(1,0,0;1.5708rad)
  Radius = 3
FEATURE [Part::MultiFuse] Fusion248002106  label="Fusion248002276"
  Placement = pos=(0,1,8) rot=(0,0,1;0rad)
  Shapes = -> [Loft023,Cylinder1167]
FEATURE [Part::Cylinder] Cylinder1168  label="Cylinder1603"
  Angle = 360
  Height = 5
  Placement = pos=(131,33,12) rot=(1,0,0;1.5708rad)
  Radius = 1.6
FEATURE [Part::Cylinder] Cylinder1169  label="Cylinder1604"
  Angle = 360
  Height = 25
  Placement = pos=(144,53,-6) rot=(1,0,0;1.5708rad)
  Radius = 1.6
FEATURE [Part::MultiFuse] Fusion248002107  label="Fusion248002277"
  Placement = pos=(0,1,8) rot=(0,0,1;0rad)
  Shapes = -> [Cylinder1168,Cylinder1169]
FEATURE [Part::Cylinder] Cylinder1170  label="Cylinder1605"
  Angle = 360
  Height = 15
  Placement = pos=(132,61.5,-16) rot=(1,0,0;1.5708rad)
  Radius = 1.6
FEATURE [Part::Cylinder] Cylinder1171  label="Cylinder1606"
  Angle = 360
  Height = 2.5
  Placement = pos=(132,49,-16) rot=(1,0,0;1.5708rad)
  Radius = 3
FEATURE [Part::MultiFuse] Fusion248002108  label="Fusion248002278"
  Placement = pos=(4,-1.5,7) rot=(0,0,1;0rad)
  Shapes = -> [Cylinder1170,Cylinder1171]
FEATURE [Part::Box] Box741  label="Cube903"
  Height = 9.5
  Length = 10
  Placement = pos=(143,45.5,-18) rot=(0,0,1;0rad)
  Width = 5
FEATURE [Part::Fillet] Fillet007050
  Base = -> Box741
  Edges = 1 edges r=4: [Edge2]
FEATURE [Part::Cylinder] Cylinder1172  label="Cylinder1607"
  Angle = 360
  Height = 3.5
  Placement = pos=(148.5,53.5,-13.5) rot=(1,0,0;1.5708rad)
  Radius = 3
FEATURE [Part::Cylinder] Cylinder1173  label="Cylinder1608"
  Angle = 360
  Height = 1.75
  Placement = pos=(498.5,51.75,-13.5) rot=(1,0,0;1.5708rad)
  Radius = 2.1
FEATURE [Part::Cylinder] Cylinder1174  label="Cylinder1609"
  Angle = 360
  Height = 3.5
  Placement = pos=(498.5,53.5,-13.5) rot=(1,0,0;1.5708rad)
  Radius = 1.5
FEATURE [Part::MultiFuse] Fusion248002109  label="Fusion248002279"
  Placement = pos=(-350,0,0) rot=(0,0,1;0rad)
  Shapes = -> [Cylinder1173,Cylinder1174]
FEATURE [Part::Cut] Cut014269  label="Cut014446"
  Base = -> Box740
  Tool = -> Fillet007050
FEATURE [Part::MultiFuse] Fusion248002110  label="Fusion248002280"
  Shapes = -> [Cut014269,Cylinder1172]
FEATURE [Part::Cut] Cut014270  label="Cut014447"
  Base = -> Fusion248002110
  Placement = pos=(0,0,3) rot=(0,0,1;0rad)
  Tool = -> Fusion248002109
FEATURE [Part::Cylinder] Cylinder1175  label="Cylinder1610"
  Angle = 360
  Height = 23
  Placement = pos=(131,52,-6) rot=(1,0,0;0.785398rad)
  Radius = 3
FEATURE [Part::Cylinder] Cylinder1176  label="Cylinder1611"
  Angle = 360
  Height = 18
  Placement = pos=(131,52,-6) rot=(1,0,0;0.785398rad)
  Radius = 3
FEATURE [Part::Cut] Cut014271  label="Cut014448"
  Base = -> Cylinder1175
  Tool = -> Cylinder1176
FEATURE [Part::MultiFuse] Fusion248002111  label="Fusion248002281"
  Placement = pos=(0,0,8) rot=(0,0,1;0rad)
  Shapes = -> [Cylinder1166,Cut014271]
FEATURE [Part::MultiFuse] Fusion248002112  label="Fusion248002282"
  Shapes = -> [Fusion248002111,Fusion248002106]
FEATURE [Part::MultiFuse] Fusion248002113  label="Fusion248002283"
  Shapes = -> [Cut014270,Fusion248002112,Cylinder1165]
FEATURE [Part::Cut] Cut014272  label="Cut014449"
  Base = -> Fusion248002113
  Tool = -> Fusion248002107
FEATURE [Part::Cut] Cut014273  label="Cut014450"
  Base = -> Cut014272
  Tool = -> Fusion248002108
FEATURE [Part::Chamfer] Chamfer165
  Base = -> Cut014273
  Edges = 1 edges r=7: [Edge12]
FEATURE [Part::Fillet] Fillet007067  label="wing-support-left"
  Base = -> Chamfer165
  Edges = 1 edges r=3: [Edge15]
FEATURE [Part::Box] Box764  label="Cube926"
  Height = 20
  Length = 25
  Placement = pos=(128,45.5,-18) rot=(0,0,1;0rad)
  Width = 8
FEATURE [Part::Cylinder] Cylinder1224  label="Cylinder1636"
  Angle = 360
  Height = 24.5
  Placement = pos=(144,53.5,2) rot=(1,0,0;1.5708rad)
  Radius = 3
FEATURE [Part::Cylinder] Cylinder1225  label="Cylinder1637"
  Angle = 360
  Height = 18
  Placement = pos=(131,51,-5) rot=(1,0,0;0.785398rad)
  Radius = 3
FEATURE [Part::Feature] Face069
  shape: bbox 7.785 x 2e-07 x 7.712 mm, 1 faces, 0 solids (baked)
FEATURE [Part::Feature] Face070
  shape: bbox 7.318 x 4.987 x 4.987 mm, 1 faces, 0 solids (baked)
FEATURE [Part::Loft] Loft028
  Closed = false
  Ruled = true
  Sections = -> [Face069,Face070]
  Solid = true
FEATURE [Part::Cylinder] Cylinder1226  label="Cylinder1638"
  Angle = 360
  Height = 3
  Placement = pos=(131,31,12) rot=(1,0,0;1.5708rad)
  Radius = 3
FEATURE [Part::MultiFuse] Fusion248002151  label="Fusion248002300"
  Placement = pos=(0,1,8) rot=(0,0,1;0rad)
  Shapes = -> [Loft028,Cylinder1226]
FEATURE [Part::Cylinder] Cylinder1227  label="Cylinder1639"
  Angle = 360
  Height = 5
  Placement = pos=(131,33,12) rot=(1,0,0;1.5708rad)
  Radius = 1.6
FEATURE [Part::Cylinder] Cylinder1228  label="Cylinder1640"
  Angle = 360
  Height = 25
  Placement = pos=(144,53,-6) rot=(1,0,0;1.5708rad)
  Radius = 1.6
FEATURE [Part::MultiFuse] Fusion248002152  label="Fusion248002301"
  Placement = pos=(0,1,8) rot=(0,0,1;0rad)
  Shapes = -> [Cylinder1227,Cylinder1228]
FEATURE [Part::Cylinder] Cylinder1229  label="Cylinder1641"
  Angle = 360
  Height = 15
  Placement = pos=(132,61.5,-16) rot=(1,0,0;1.5708rad)
  Radius = 1.6
FEATURE [Part::Cylinder] Cylinder1230  label="Cylinder1642"
  Angle = 360
  Height = 2.5
  Placement = pos=(132,49,-16) rot=(1,0,0;1.5708rad)
  Radius = 3
FEATURE [Part::MultiFuse] Fusion248002153  label="Fusion248002302"
  Placement = pos=(4,-1.5,7) rot=(0,0,1;0rad)
  Shapes = -> [Cylinder1229,Cylinder1230]
FEATURE [Part::Box] Box765  label="Cube927"
  Height = 9.5
  Length = 10
  Placement = pos=(143,45.5,-18) rot=(0,0,1;0rad)
  Width = 5
FEATURE [Part::Fillet] Fillet007068
  Base = -> Box765
  Edges = 1 edges r=4: [Edge2]
FEATURE [Part::Cylinder] Cylinder1231  label="Cylinder1643"
  Angle = 360
  Height = 3.5
  Placement = pos=(148.5,53.5,-13.5) rot=(1,0,0;1.5708rad)
  Radius = 3
FEATURE [Part::Cylinder] Cylinder1232  label="Cylinder1644"
  Angle = 360
  Height = 1.75
  Placement = pos=(498.5,51.75,-13.5) rot=(1,0,0;1.5708rad)
  Radius = 2.1
FEATURE [Part::Cylinder] Cylinder1233  label="Cylinder1645"
  Angle = 360
  Height = 3.5
  Placement = pos=(498.5,53.5,-13.5) rot=(1,0,0;1.5708rad)
  Radius = 1.5
FEATURE [Part::MultiFuse] Fusion248002154  label="Fusion248002303"
  Placement = pos=(-350,0,0) rot=(0,0,1;0rad)
  Shapes = -> [Cylinder1232,Cylinder1233]
FEATURE [Part::Cut] Cut014302  label="Cut014465"
  Base = -> Box764
  Tool = -> Fillet007068
FEATURE [Part::MultiFuse] Fusion248002155  label="Fusion248002304"
  Shapes = -> [Cut014302,Cylinder1231]
FEATURE [Part::Cut] Cut014303  label="Cut014466"
  Base = -> Fusion248002155
  Placement = pos=(0,0,3) rot=(0,0,1;0rad)
  Tool = -> Fusion248002154
FEATURE [Part::Cylinder] Cylinder1234  label="Cylinder1646"
  Angle = 360
  Height = 23
  Placement = pos=(131,52,-6) rot=(1,0,0;0.785398rad)
  Radius = 3
FEATURE [Part::Cylinder] Cylinder1235  label="Cylinder1647"
  Angle = 360
  Height = 18
  Placement = pos=(131,52,-6) rot=(1,0,0;0.785398rad)
  Radius = 3
FEATURE [Part::Cut] Cut014304  label="Cut014467"
  Base = -> Cylinder1234
  Tool = -> Cylinder1235
FEATURE [Part::MultiFuse] Fusion248002156  label="Fusion248002305"
  Placement = pos=(0,0,8) rot=(0,0,1;0rad)
  Shapes = -> [Cylinder1225,Cut014304]
FEATURE [Part::MultiFuse] Fusion248002157  label="Fusion248002306"
  Shapes = -> [Fusion248002156,Fusion248002151]
FEATURE [Part::MultiFuse] Fusion248002158  label="Fusion248002307"
  Shapes = -> [Cut014303,Fusion248002157,Cylinder1224]
FEATURE [Part::Cut] Cut014305  label="Cut014468"
  Base = -> Fusion248002158
  Tool = -> Fusion248002152
FEATURE [Part::Cut] Cut014306  label="Cut014469"
  Base = -> Cut014305
  Tool = -> Fusion248002153
FEATURE [Part::Chamfer] Chamfer166
  Base = -> Cut014306
  Edges = 1 edges r=7: [Edge12]
FEATURE [Part::Fillet] Fillet007069  label="wing-support-left-lifted001"
  Base = -> Chamfer166
  Edges = 1 edges r=3: [Edge15]
FEATURE [Part::Mirroring] Part__Mirroring114  label="wing-support-right"
  Base = (0,0,0)
  Normal = (0,1,0)
  Placement = pos=(0,170,0) rot=(0,0,1;0rad)
  Source = -> Fillet007069
FEATURE [Part::Box] Box629  label="Cube854"
  Height = 23
  Length = 37
  Placement = pos=(15,152,-23) rot=(0,0,1;0rad)
  Width = 18
FEATURE [Part::Cylinder] Cylinder364
  Angle = 360
  Height = 22
  Placement = pos=(98,174,-23) rot=(1,0,0;1.5708rad)
  Radius = 52
FEATURE [Part::Box] Box630  label="Cube855"
  Height = 9
  Length = 31
  Placement = pos=(17,156,-29) rot=(0,0,1;0rad)
  Width = 14
FEATURE [Part::Cylinder] Cylinder365
  Angle = 360
  Height = 22
  Placement = pos=(98,174,-23) rot=(1,0,0;1.5708rad)
  Radius = 54
FEATURE [Part::Box] Box631  label="Cube856"
  Height = 7.5
  Length = 4
  Placement = pos=(44,152,-31) rot=(0,0,1;0rad)
  Width = 22
FEATURE [Part::Box] Box632  label="Cube857"
  Height = 18
  Length = 31
  Placement = pos=(17,158,-20) rot=(0,0,1;0rad)
  Width = 12
FEATURE [Part::Cylinder] Cylinder366
  Angle = 360
  Height = 22
  Placement = pos=(98,174,-23) rot=(1,0,0;1.5708rad)
  Radius = 54
FEATURE [Part::Cut] Cut568  label="Cut860"
  Base = -> Box632
  Tool = -> Cylinder366
FEATURE [Part::Box] Box633  label="Cube858"
  Height = 21
  Length = 38
  Placement = pos=(15,167,-23) rot=(0,0,1;0rad)
  Width = 3
FEATURE [Part::Cut] Cut575  label="Cut867"
  Base = -> Box629
  Tool = -> Cylinder364
FEATURE [Part::Cut] Cut576  label="Cut868"
  Base = -> Cut575
  Tool = -> Cut568
FEATURE [Part::Box] Box642  label="Cube867"
  Height = 20
  Length = 33
  Placement = pos=(15,156,-31) rot=(0,0,1;0rad)
  Width = 14
FEATURE [Part::Cylinder] Cylinder370
  Angle = 360
  Height = 22
  Placement = pos=(98,174,-23) rot=(1,0,0;1.5708rad)
  Radius = 52
FEATURE [Part::Box] Box643  label="Cube868"
  Height = 9
  Length = 5
  Placement = pos=(46,152,-32) rot=(0,0,1;0rad)
  Width = 22
FEATURE [Part::MultiFuse] Fusion353
  Shapes = -> [Cylinder370,Box643]
FEATURE [Part::Cut] Cut577  label="Cut869"
  Base = -> Box642
  Tool = -> Fusion353
FEATURE [Part::MultiFuse] Fusion354
  Shapes = -> [Cylinder365,Box631]
FEATURE [Part::Cut] Cut578  label="Cut870"
  Base = -> Box630
  Tool = -> Fusion354
FEATURE [Part::Cut] Cut579  label="Cut871"
  Base = -> Cut577
  Tool = -> Cut578
FEATURE [Part::Box] Box644  label="Cube869"
  Height = 2
  Length = 33
  Placement = pos=(15,156,-31) rot=(0,0,1;0rad)
  Width = 14
FEATURE [Part::Box] Box645  label="Cube870"
  Height = 20
  Length = 33
  Placement = pos=(15,169,-29) rot=(0,0,1;0rad)
  Width = 3
FEATURE [Part::Cut] Cut580  label="Cut872"
  Base = -> Box645
  Tool = -> Box644
FEATURE [Part::Cut] Cut581  label="Cut873"
  Base = -> Cut579
  Tool = -> Cut580
FEATURE [Part::Box] Box646  label="Cube871"
  Height = 12
  Length = 28
  Placement = pos=(17,165,-24) rot=(-1,0,0;0.279253rad)
  Width = 3
FEATURE [Part::Cylinder] Cylinder371
  Angle = 360
  Height = 22
  Placement = pos=(98,174,-23) rot=(1,0,0;1.5708rad)
  Radius = 54
FEATURE [Part::Box] Box647  label="Cube872"
  Height = 9
  Length = 5
  Placement = pos=(44,152,-32) rot=(0,0,1;0rad)
  Width = 22
FEATURE [Part::MultiFuse] Fusion355
  Shapes = -> [Cylinder371,Box647]
FEATURE [Part::Cut] Cut582  label="Cut874"
  Base = -> Box646
  Placement = pos=(0,1,0) rot=(0,0,1;0rad)
  Tool = -> Fusion355
FEATURE [Part::Cut] Cut583  label="Cut875"
  Base = -> Cut581
  Tool = -> Cut582
FEATURE [Part::Fillet] Fillet467  label="wing-right-step"
  Base = -> Cut583
  Edges = 2 edges r=1: [Edge4,Edge32]
  Placement = pos=(0,0,8) rot=(0,0,1;0rad)
FEATURE [Part::Cylinder] Cylinder372
  Angle = 360
  Height = 10
  Placement = pos=(18,15,-5) rot=(0,0,1;0rad)
  Radius = 0.9
FEATURE [Part::Cylinder] Cylinder373
  Angle = 360
  Height = 10
  Placement = pos=(49,15,-5) rot=(0,0,1;0rad)
  Radius = 0.9
FEATURE [Part::MultiFuse] Fusion356
  Shapes = -> [Cylinder372,Cylinder373]
FEATURE [Part::Mirroring] Part__Mirroring076  label="Fusion211 (Mirror #27)001"
  Base = (0,0,0)
  Normal = (0,1,0)
  Placement = pos=(0,170,0) rot=(0,0,1;0rad)
  Source = -> Fusion356
FEATURE [Part::Cut] Cut584  label="Cut876"
  Base = -> Cut576
  Tool = -> Box633
FEATURE [Part::Box] Box648  label="Cube873"
  Height = 9
  Length = 31
  Placement = pos=(17,156,-29) rot=(0,0,1;0rad)
  Width = 14
FEATURE [Part::Cylinder] Cylinder251
  Angle = 360
  Height = 22
  Placement = pos=(98,174,-23) rot=(1,0,0;1.5708rad)
  Radius = 54
FEATURE [Part::Box] Box649  label="Cube874"
  Height = 7.5
  Length = 4
  Placement = pos=(44,152,-31) rot=(0,0,1;0rad)
  Width = 22
FEATURE [Part::Box] Box650  label="Cube875"
  Height = 20
  Length = 33
  Placement = pos=(15,156,-31) rot=(0,0,1;0rad)
  Width = 14
FEATURE [Part::Cylinder] Cylinder252
  Angle = 360
  Height = 22
  Placement = pos=(98,174,-23) rot=(1,0,0;1.5708rad)
  Radius = 52
FEATURE [Part::Box] Box651  label="Cube876"
  Height = 9
  Length = 5
  Placement = pos=(46,152,-32) rot=(0,0,1;0rad)
  Width = 22
FEATURE [Part::MultiFuse] Fusion212
  Shapes = -> [Cylinder252,Box651]
FEATURE [Part::Cut] Cut585  label="Cut877"
  Base = -> Box650
  Tool = -> Fusion212
FEATURE [Part::MultiFuse] Fusion213
  Shapes = -> [Cylinder251,Box649]
FEATURE [Part::Cut] Cut586  label="Cut878"
  Base = -> Box648
  Tool = -> Fusion213
FEATURE [Part::Cut] Cut587  label="Cut879"
  Base = -> Cut585
  Tool = -> Cut586
FEATURE [Part::Box] Box652  label="Cube877"
  Height = 2
  Length = 33
  Placement = pos=(15,156,-31) rot=(0,0,1;0rad)
  Width = 14
FEATURE [Part::Box] Box653  label="Cube878"
  Height = 20
  Length = 33
  Placement = pos=(15,169,-29) rot=(0,0,1;0rad)
  Width = 3
FEATURE [Part::Cut] Cut588  label="Cut880"
  Base = -> Box653
  Tool = -> Box652
FEATURE [Part::Cut] Cut589  label="Cut881"
  Base = -> Cut587
  Tool = -> Cut588
FEATURE [Part::Box] Box654  label="Cube879"
  Height = 12
  Length = 28
  Placement = pos=(17,165,-24) rot=(-1,0,0;0.279253rad)
  Width = 3
FEATURE [Part::Cylinder] Cylinder253
  Angle = 360
  Height = 22
  Placement = pos=(98,174,-23) rot=(1,0,0;1.5708rad)
  Radius = 54
FEATURE [Part::Box] Box258  label="Cube484"
  Height = 9
  Length = 5
  Placement = pos=(44,152,-32) rot=(0,0,1;0rad)
  Width = 22
FEATURE [Part::MultiFuse] Fusion214
  Shapes = -> [Cylinder253,Box258]
FEATURE [Part::Cut] Cut590  label="Cut882"
  Base = -> Box654
  Placement = pos=(0,1,0) rot=(0,0,1;0rad)
  Tool = -> Fusion214
FEATURE [Part::Cut] Cut591  label="Cut883"
  Base = -> Cut589
  Tool = -> Cut590
FEATURE [Part::Fillet] Fillet136
  Base = -> Cut591
  Edges = 2 edges r=1: [Edge4,Edge32]
FEATURE [Part::Cut] Cut592  label="Cut884"
  Base = -> Cut584
  Tool = -> Fillet136
FEATURE [Part::Cut] Cut593  label="wing-right-chassis"
  Base = -> Cut592
  Placement = pos=(0,0,8) rot=(0,0,1;0rad)
  Tool = -> Part__Mirroring076
FEATURE [Part::Box] Box260  label="Cube486"
  Height = 23
  Length = 37
  Placement = pos=(15,152,-23) rot=(0,0,1;0rad)
  Width = 18
FEATURE [Part::Cylinder] Cylinder254
  Angle = 360
  Height = 22
  Placement = pos=(98,174,-23) rot=(1,0,0;1.5708rad)
  Radius = 52
FEATURE [Part::Box] Box261  label="Cube487"
  Height = 9
  Length = 31
  Placement = pos=(17,156,-29) rot=(0,0,1;0rad)
  Width = 14
FEATURE [Part::Cylinder] Cylinder255
  Angle = 360
  Height = 22
  Placement = pos=(98,174,-23) rot=(1,0,0;1.5708rad)
  Radius = 54
FEATURE [Part::Box] Box262  label="Cube488"
  Height = 7.5
  Length = 4
  Placement = pos=(44,152,-31) rot=(0,0,1;0rad)
  Width = 22
FEATURE [Part::Box] Box263  label="Cube489"
  Height = 18
  Length = 31
  Placement = pos=(17,158,-20) rot=(0,0,1;0rad)
  Width = 12
FEATURE [Part::Cylinder] Cylinder256
  Angle = 360
  Height = 22
  Placement = pos=(98,174,-23) rot=(1,0,0;1.5708rad)
  Radius = 54
FEATURE [Part::Cut] Cut594  label="Cut885"
  Base = -> Box263
  Tool = -> Cylinder256
FEATURE [Part::Box] Box264  label="Cube490"
  Height = 21
  Length = 38
  Placement = pos=(15,167,-23) rot=(0,0,1;0rad)
  Width = 3
FEATURE [Part::Cut] Cut316  label="Cut891"
  Base = -> Box260
  Tool = -> Cylinder254
FEATURE [Part::Cut] Cut317  label="Cut892"
  Base = -> Cut316
  Tool = -> Cut594
FEATURE [Part::Box] Box273  label="Cube499"
  Height = 20
  Length = 33
  Placement = pos=(15,156,-31) rot=(0,0,1;0rad)
  Width = 14
FEATURE [Part::Cylinder] Cylinder260
  Angle = 360
  Height = 22
  Placement = pos=(98,174,-23) rot=(1,0,0;1.5708rad)
  Radius = 52
FEATURE [Part::Box] Box274  label="Cube500"
  Height = 9
  Length = 5
  Placement = pos=(46,152,-32) rot=(0,0,1;0rad)
  Width = 22
FEATURE [Part::MultiFuse] Fusion219
  Shapes = -> [Cylinder260,Box274]
FEATURE [Part::Cut] Cut318  label="Cut893"
  Base = -> Box273
  Tool = -> Fusion219
FEATURE [Part::MultiFuse] Fusion220
  Shapes = -> [Cylinder255,Box262]
FEATURE [Part::Cut] Cut319  label="Cut894"
  Base = -> Box261
  Tool = -> Fusion220
FEATURE [Part::Cut] Cut320  label="Cut895"
  Base = -> Cut318
  Tool = -> Cut319
FEATURE [Part::Box] Box275  label="Cube501"
  Height = 2
  Length = 33
  Placement = pos=(15,156,-31) rot=(0,0,1;0rad)
  Width = 14
FEATURE [Part::Box] Box276  label="Cube502"
  Height = 20
  Length = 33
  Placement = pos=(15,169,-29) rot=(0,0,1;0rad)
  Width = 3
FEATURE [Part::Cut] Cut321  label="Cut896"
  Base = -> Box276
  Tool = -> Box275
FEATURE [Part::Cut] Cut322  label="Cut897"
  Base = -> Cut320
  Tool = -> Cut321
FEATURE [Part::Box] Box277  label="Cube503"
  Height = 12
  Length = 28
  Placement = pos=(17,165,-24) rot=(-1,0,0;0.279253rad)
  Width = 3
FEATURE [Part::Cylinder] Cylinder261
  Angle = 360
  Height = 22
  Placement = pos=(98,174,-23) rot=(1,0,0;1.5708rad)
  Radius = 54
FEATURE [Part::Box] Box655  label="Cube880"
  Height = 9
  Length = 5
  Placement = pos=(44,152,-32) rot=(0,0,1;0rad)
  Width = 22
FEATURE [Part::MultiFuse] Fusion221
  Shapes = -> [Cylinder261,Box655]
FEATURE [Part::Cut] Cut598  label="Cut898"
  Base = -> Box277
  Placement = pos=(0,1,0) rot=(0,0,1;0rad)
  Tool = -> Fusion221
FEATURE [Part::Cut] Cut599  label="Cut899"
  Base = -> Cut322
  Tool = -> Cut598
FEATURE [Part::Fillet] Fillet140
  Base = -> Cut599
  Edges = 2 edges r=1: [Edge4,Edge32]
FEATURE [Part::Cylinder] Cylinder262
  Angle = 360
  Height = 10
  Placement = pos=(18,15,-5) rot=(0,0,1;0rad)
  Radius = 0.9
FEATURE [Part::Cylinder] Cylinder263
  Angle = 360
  Height = 10
  Placement = pos=(49,15,-5) rot=(0,0,1;0rad)
  Radius = 0.9
FEATURE [Part::MultiFuse] Fusion222
  Shapes = -> [Cylinder262,Cylinder263]
FEATURE [Part::Mirroring] Part__Mirroring078  label="Fusion211 (Mirror #27)002"
  Base = (0,0,0)
  Normal = (0,1,0)
  Placement = pos=(0,170,0) rot=(0,0,1;0rad)
  Source = -> Fusion222
FEATURE [Part::Cut] Cut325  label="Cut900"
  Base = -> Cut317
  Tool = -> Box264
FEATURE [Part::Box] Box656  label="Cube881"
  Height = 9
  Length = 31
  Placement = pos=(17,156,-29) rot=(0,0,1;0rad)
  Width = 14
FEATURE [Part::Cylinder] Cylinder264
  Angle = 360
  Height = 22
  Placement = pos=(98,174,-23) rot=(1,0,0;1.5708rad)
  Radius = 54
FEATURE [Part::Box] Box657  label="Cube882"
  Height = 7.5
  Length = 4
  Placement = pos=(44,152,-31) rot=(0,0,1;0rad)
  Width = 22
FEATURE [Part::Box] Box658  label="Cube883"
  Height = 20
  Length = 33
  Placement = pos=(15,156,-31) rot=(0,0,1;0rad)
  Width = 14
FEATURE [Part::Cylinder] Cylinder265
  Angle = 360
  Height = 22
  Placement = pos=(98,174,-23) rot=(1,0,0;1.5708rad)
  Radius = 52
FEATURE [Part::Box] Box766  label="Cube884"
  Height = 9
  Length = 5
  Placement = pos=(46,152,-32) rot=(0,0,1;0rad)
  Width = 22
FEATURE [Part::MultiFuse] Fusion223
  Shapes = -> [Cylinder265,Box766]
FEATURE [Part::Cut] Cut326  label="Cut901"
  Base = -> Box658
  Tool = -> Fusion223
FEATURE [Part::MultiFuse] Fusion224
  Shapes = -> [Cylinder264,Box657]
FEATURE [Part::Cut] Cut327  label="Cut902"
  Base = -> Box656
  Tool = -> Fusion224
FEATURE [Part::Cut] Cut328  label="Cut903"
  Base = -> Cut326
  Tool = -> Cut327
FEATURE [Part::Box] Box767  label="Cube885"
  Height = 2
  Length = 33
  Placement = pos=(15,156,-31) rot=(0,0,1;0rad)
  Width = 14
FEATURE [Part::Box] Box661  label="Cube886"
  Height = 20
  Length = 33
  Placement = pos=(15,169,-29) rot=(0,0,1;0rad)
  Width = 3
FEATURE [Part::Cut] Cut329  label="Cut904"
  Base = -> Box661
  Tool = -> Box767
FEATURE [Part::Cut] Cut330  label="Cut905"
  Base = -> Cut328
  Tool = -> Cut329
FEATURE [Part::Box] Box662  label="Cube887"
  Height = 12
  Length = 28
  Placement = pos=(17,165,-24) rot=(-1,0,0;0.279253rad)
  Width = 3
FEATURE [Part::Cylinder] Cylinder266
  Angle = 360
  Height = 22
  Placement = pos=(98,174,-23) rot=(1,0,0;1.5708rad)
  Radius = 54
FEATURE [Part::Box] Box286  label="Cube512"
  Height = 9
  Length = 5
  Placement = pos=(44,152,-32) rot=(0,0,1;0rad)
  Width = 22
FEATURE [Part::MultiFuse] Fusion225
  Shapes = -> [Cylinder266,Box286]
FEATURE [Part::Cut] Cut331  label="Cut906"
  Base = -> Box662
  Placement = pos=(0,1,0) rot=(0,0,1;0rad)
  Tool = -> Fusion225
FEATURE [Part::Cut] Cut332  label="Cut907"
  Base = -> Cut330
  Tool = -> Cut331
FEATURE [Part::Fillet] Fillet141
  Base = -> Cut332
  Edges = 2 edges r=1: [Edge4,Edge32]
FEATURE [Part::Cut] Cut333
  Base = -> Cut325
  Tool = -> Fillet141
FEATURE [Part::Cut] Cut600  label="Cut908"
  Base = -> Cut333
  Tool = -> Part__Mirroring078
FEATURE [Part::Mirroring] Part__Mirroring080  label="wing-left-step"
  Base = (0,0,0)
  Normal = (0,1,0)
  Placement = pos=(0,170,8) rot=(0,0,1;0rad)
  Source = -> Fillet140
FEATURE [Part::Mirroring] Part__Mirroring081  label="wing-left-chassis"
  Base = (0,0,0)
  Normal = (0,1,0)
  Placement = pos=(0,170,8) rot=(0,0,1;0rad)
  Source = -> Cut600
FEATURE [Part::Box] Box214  label="Cube209"
  Height = 22
  Length = 10
  Placement = pos=(4,7,35) rot=(0,0,1;0rad)
  Width = 154
FEATURE [Part::Box] Box215  label="Cube210"
  Height = 22
  Length = 10
  Placement = pos=(14,7,35) rot=(0,0,1;0rad)
  Width = 154
FEATURE [Part::Chamfer] Chamfer005
  Base = -> Box215
  Edges = 1 edges: [Edge6 r1=15 r2=8]
FEATURE [Part::Chamfer] Chamfer006
  Base = -> Chamfer005
  Edges = 1 edges r=5: [Edge3]
FEATURE [Part::MultiFuse] Fusion115
  Shapes = -> [Box214,Chamfer006]
FEATURE [Part::Box] Box216  label="Cube211"
  Height = 22
  Length = 17
  Placement = pos=(4,4,35) rot=(0,0,1;0rad)
  Width = 160
FEATURE [Part::Box] Box217  label="Cube212"
  Height = 22
  Length = 18
  Placement = pos=(3,3,35) rot=(0,0,1;0rad)
  Width = 162
FEATURE [Part::Fillet] Fillet109
  Base = -> Box216
  Edges = 2 edges r=15: [Edge1,Edge3]
FEATURE [Part::Cut] Cut128
  Base = -> Box217
  Tool = -> Fillet109
FEATURE [Part::Fillet] Fillet110
  Base = -> Fusion115
  Edges = 4 edges r=2: [Edge2,Edge3,Edge6,Edge9]
FEATURE [Part::Box] Box218  label="Cube213"
  Height = 31
  Length = 9
  Placement = pos=(4,46,14) rot=(0,0,1;0rad)
  Width = 77
FEATURE [Part::Cut] Cut129
  Base = -> Fillet110
  Tool = -> Cut128
FEATURE [Part::Cut] Cut130
  Base = -> Cut129
  Tool = -> Box218
FEATURE [Part::Box] Box219  label="Cube214"
  Height = 37
  Length = 80
  Placement = pos=(17,52.5,11) rot=(0,0,1;0rad)
  Width = 65
FEATURE [Part::Box] Box220  label="Cube215"
  Height = 31
  Length = 1
  Placement = pos=(15,5,4) rot=(0,0,1;0rad)
  Width = 53
FEATURE [Part::Box] Box221  label="Cube216"
  Height = 1
  Length = 40
  Placement = pos=(15,5,4) rot=(0,0,1;0rad)
  Width = 53
FEATURE [Part::Box] Box222  label="Cube217"
  Height = 46
  Length = 81
  Placement = pos=(16,53.5,1) rot=(0,0,1;0rad)
  Width = 63
FEATURE [Part::Cylinder] Cylinder087
  Angle = 360
  Height = 184
  Placement = pos=(98,176,-23) rot=(1,0,0;1.5708rad)
  Radius = 51
FEATURE [Part::Cylinder] Cylinder088
  Angle = 59.4
  Height = 53
  Placement = pos=(98,5,-23) rot=(0.192433,0.693891,0.693891;3.52181rad)
  Radius = 53
FEATURE [Part::Box] Box230  label="Cube225"
  Height = 46
  Length = 20
  Placement = pos=(16,55.5,4.5) rot=(0,0,1;0rad)
  Width = 57
FEATURE [Part::Fillet] Fillet116
  Base = -> Box230
  Edges = 2 edges r=3: [Edge10,Edge12]
FEATURE [Part::Box] Box236  label="Cube231"
  Height = 3
  Length = 35
  Placement = pos=(20,5,1) rot=(0,0,1;0rad)
  Width = 9
FEATURE [Part::MultiFuse] Fusion116
  Shapes = -> [Box236,Box220,Box221,Cylinder088]
FEATURE [Part::Box] Box237  label="Cube232"
  Height = 4
  Length = 14
  Placement = pos=(91,4,26) rot=(0,0,1;0rad)
  Width = 10.5
FEATURE [Part::Box] Box238  label="Cube233"
  Height = 1
  Length = 40
  Placement = pos=(15,14,3) rot=(0,0,1;0rad)
  Width = 44
FEATURE [Part::Cut] Cut139
  Base = -> Fusion116
  Tool = -> Box238
FEATURE [Part::Cut] Cut140
  Base = -> Cut139
  Tool = -> Cylinder087
FEATURE [Part::Box] Box239  label="Cube234"
  Height = 31
  Length = 1
  Placement = pos=(15,5,4) rot=(0,0,1;0rad)
  Width = 53
FEATURE [Part::Box] Box240  label="Cube235"
  Height = 1
  Length = 40
  Placement = pos=(15,5,4) rot=(0,0,1;0rad)
  Width = 53
FEATURE [Part::Cylinder] Cylinder089
  Angle = 360
  Height = 184
  Placement = pos=(98,176,-23) rot=(1,0,0;1.5708rad)
  Radius = 51
FEATURE [Part::Cylinder] Cylinder090
  Angle = 59.4
  Height = 53
  Placement = pos=(98,5,-23) rot=(0.192433,0.693891,0.693891;3.52181rad)
  Radius = 53
FEATURE [Part::Box] Box241  label="Cube236"
  Height = 3
  Length = 35
  Placement = pos=(20,5,1) rot=(0,0,1;0rad)
  Width = 9
FEATURE [Part::MultiFuse] Fusion117
  Shapes = -> [Box241,Box239,Box240,Cylinder090]
FEATURE [Part::Box] Box242  label="Cube237"
  Height = 4
  Length = 14
  Placement = pos=(91,4,26) rot=(0,0,1;0rad)
  Width = 10.5
FEATURE [Part::Box] Box243  label="Cube238"
  Height = 1
  Length = 40
  Placement = pos=(15,14,3) rot=(0,0,1;0rad)
  Width = 44
FEATURE [Part::Cut] Cut142
  Base = -> Fusion117
  Tool = -> Box243
FEATURE [Part::Cut] Cut143
  Base = -> Cut142
  Tool = -> Cylinder089
FEATURE [Part::Cut] Cut144
  Base = -> Cut143
  Tool = -> Box242
FEATURE [Part::Mirroring] Part__Mirroring009  label="Cut144 (Mirror #6)"
  Base = (0,0,0)
  Normal = (0,1,0)
  Placement = pos=(0,168,0) rot=(0,0,1;0rad)
  Source = -> Cut144
FEATURE [Part::Box] Box768  label="Cube257"
  Height = 10
  Length = 38
  Placement = pos=(45,11,30) rot=(0,0,1;0rad)
  Width = 38
FEATURE [Part::Box] Box769  label="Cube258"
  Height = 45
  Length = 13
  Placement = pos=(75,11,30) rot=(0,0,1;0rad)
  Width = 38
FEATURE [Part::Chamfer] Chamfer035
  Base = -> Box768
  Edges = 2 edges: [Edge2 r1=2 r2=12,Edge6 r1=2 r2=12]
FEATURE [Part::Fillet] Fillet149
  Base = -> Chamfer035
  Edges = 3 edges r=3: [Edge3,Edge13,Edge17]
FEATURE [Part::Fillet] Fillet150
  Base = -> Fillet149
  Edges = 1 edges r=5: [Edge3]
FEATURE [Part::Fillet] Fillet151
  Base = -> Fillet150
  Edges = 6 edges r=2: [Edge7,Edge9,Edge11,Edge18,Edge20,Edge22]
FEATURE [Part::Fillet] Fillet152
  Base = -> Fillet151
  Edges = 2 edges r=20: [Edge23,Edge49]
FEATURE [Part::Chamfer] Chamfer036
  Base = -> Box769
  Edges = 1 edges: [Edge2 r1=20 r2=5]
FEATURE [Part::Chamfer] Chamfer037
  Base = -> Chamfer036
  Edges = 1 edges: [Edge3 r1=15 r2=3]
FEATURE [Part::Fillet] Fillet153
  Base = -> Chamfer037
  Edges = 4 edges r=3: [Edge10,Edge12,Edge17,Edge18]
FEATURE [Part::Fillet] Fillet154
  Base = -> Fillet153
  Edges = 2 edges r=20: [Edge12,Edge16]
FEATURE [Part::Fillet] Fillet155
  Base = -> Fillet154
  Edges = 10 edges r=2: [Edge1,Edge2,Edge4,Edge6,Edge8,Edge15,Edge17,Edge21,Edge25,Edge29]
FEATURE [Part::Box] Box770  label="Cube259"
  Height = 48
  Length = 7
  Placement = pos=(69,12,30) rot=(0,1,0;0.10472rad)
  Width = 36
FEATURE [Part::Box] Box771  label="Cube260"
  Height = 50
  Length = 16
  Placement = pos=(75,0,30) rot=(-0.683576,-0.016559,0.729691;0.239394rad)
  Width = 8
FEATURE [Part::Box] Box772  label="Cube261"
  Height = 50
  Length = 16
  Placement = pos=(75,0,30) rot=(-0.683576,-0.016559,0.729691;0.239394rad)
  Width = 8
FEATURE [Part::Mirroring] Part__Mirroring014  label="Cube241 (Mirror #7)001"
  Base = (0,0,0)
  Normal = (0,1,0)
  Placement = pos=(0,60,0) rot=(0,0,1;0rad)
  Source = -> Box772
FEATURE [Part::MultiFuse] Fusion130
  Shapes = -> [Part__Mirroring014,Box771]
FEATURE [Part::Cut] Cut149
  Base = -> Fillet155
  Tool = -> Fusion130
FEATURE [Part::Fillet] Fillet156
  Base = -> Cut149
  Edges = 4 edges r=1.6: [Edge19,Edge23,Edge40,Edge49]
FEATURE [Part::Chamfer] Chamfer038
  Base = -> Box770
  Edges = 2 edges: [Edge10 r1=40 r2=4,Edge12 r1=40 r2=4]
FEATURE [Part::Chamfer] Chamfer039
  Base = -> Chamfer038
  Edges = 2 edges: [Edge11 r1=4 r2=7,Edge18 r1=4 r2=7]
FEATURE [Part::Fillet] Fillet157
  Base = -> Chamfer039
  Edges = 2 edges r=10: [Edge18,Edge24]
  Placement = pos=(-0.75,0,0) rot=(0,0,1;0rad)
FEATURE [Part::Cut] Cut150
  Base = -> Fillet156
  Tool = -> Fillet157
FEATURE [Part::Fillet] Fillet158
  Base = -> Cut150
  Edges = 2 edges r=2.5: [Edge93,Edge106]
FEATURE [Part::Box] Box773  label="Cube262"
  Height = 8
  Length = 10
  Placement = pos=(78,11,32) rot=(0,0,1;0rad)
  Width = 2
FEATURE [Part::Fillet] Fillet159
  Base = -> Box773
  Edges = 2 edges r=2: [Edge6,Edge8]
FEATURE [Part::Box] Box774  label="Cube263"
  Height = 7
  Length = 10
  Placement = pos=(75,10,30) rot=(0,0,1;0rad)
  Width = 3
FEATURE [Part::Chamfer] Chamfer040
  Base = -> Box774
  Edges = 1 edges r=3: [Edge6]
FEATURE [Part::Chamfer] Chamfer041
  Base = -> Chamfer040
  Edges = 1 edges: [Edge3 r1=2 r2=4]
FEATURE [Part::Chamfer] Chamfer042
  Base = -> Chamfer041
  Edges = 1 edges: [Edge18 r1=6 r2=2]
FEATURE [Part::Chamfer] Chamfer043
  Base = -> Chamfer042
  Edges = 1 edges r=3: [Edge15]
  Placement = pos=(0,1,0) rot=(0,0,1;0rad)
FEATURE [Part::Box] Box775  label="Cube264"
  Height = 8
  Length = 10
  Placement = pos=(78,11,32) rot=(0,0,1;0rad)
  Width = 2
FEATURE [Part::Fillet] Fillet160
  Base = -> Box775
  Edges = 2 edges r=2: [Edge6,Edge8]
FEATURE [Part::Box] Box270  label="Cube265"
  Height = 7
  Length = 10
  Placement = pos=(75,10,30) rot=(0,0,1;0rad)
  Width = 3
FEATURE [Part::Chamfer] Chamfer167
  Base = -> Box270
  Edges = 1 edges r=3: [Edge6]
FEATURE [Part::Chamfer] Chamfer168
  Base = -> Chamfer167
  Edges = 1 edges: [Edge3 r1=2 r2=4]
FEATURE [Part::Chamfer] Chamfer169
  Base = -> Chamfer168
  Edges = 1 edges: [Edge18 r1=6 r2=2]
FEATURE [Part::Chamfer] Chamfer170
  Base = -> Chamfer169
  Edges = 1 edges r=3: [Edge15]
  Placement = pos=(0,1,0) rot=(0,0,1;0rad)
FEATURE [Part::MultiFuse] Fusion131
  Shapes = -> [Fillet160,Chamfer170]
FEATURE [Part::Mirroring] Part__Mirroring015  label="Fusion121 (Mirror #9)001"
  Base = (0,0,0)
  Normal = (0,1,0)
  Placement = pos=(0,60,0) rot=(0,0,1;0rad)
  Source = -> Fusion131
FEATURE [Part::Cylinder] Cylinder092
  Angle = 360
  Height = 39
  Placement = pos=(81,10.5,35) rot=(-1,0,0;1.5708rad)
  Radius = 1
FEATURE [Part::MultiFuse] Fusion132
  Shapes = -> [Fillet159,Chamfer043]
FEATURE [Part::MultiFuse] Fusion133
  Shapes = -> [Part__Mirroring015,Fusion132]
FEATURE [Part::MultiFuse] Fusion134
  Shapes = -> [Fusion133,Cylinder092]
FEATURE [Part::MultiFuse] Fusion248002159  label="seat-right"
  Placement = pos=(9,110,19) rot=(0,0,1;0rad)
  Shapes = -> [Fillet158,Fusion134,Fillet152]
FEATURE [Part::Cut] Cut159
  Base = -> Cut130
  Tool = -> Fillet116
FEATURE [Part::Box] Box776  label="Cube272"
  Height = 17
  Length = 100
  Placement = pos=(50,121,4) rot=(0,0,1;0rad)
  Width = 20
FEATURE [Part::Box] Box278  label="Cube273"
  Height = 36
  Length = 42
  Placement = pos=(91,115,4) rot=(0,0,1;0rad)
  Width = 14
FEATURE [Part::Box] Box279  label="Cube274"
  Height = 36
  Length = 57
  Placement = pos=(83,110,4) rot=(0,0,1;0rad)
  Width = 16
FEATURE [Part::Cylinder] Cylinder105
  Angle = 360
  Height = 17
  Placement = pos=(47,153,5) rot=(0,0,1;0rad)
  Radius = 2
FEATURE [Part::Cylinder] Cylinder106
  Angle = 360
  Height = 17
  Placement = pos=(47,123,5) rot=(0,0,1;0rad)
  Radius = 2
FEATURE [Part::MultiFuse] Fusion143
  Placement = pos=(0,0,-2) rot=(0,0,1;0rad)
  Shapes = -> [Cylinder105,Cylinder106]
FEATURE [Part::Cylinder] Cylinder107
  Angle = 360
  Height = 17
  Placement = pos=(47,153,5) rot=(0,0,1;0rad)
  Radius = 2
FEATURE [Part::Cylinder] Cylinder108
  Angle = 360
  Height = 17
  Placement = pos=(47,123,5) rot=(0,0,1;0rad)
  Radius = 2
FEATURE [Part::MultiFuse] Fusion144
  Placement = pos=(0,-108,-2) rot=(0,0,1;0rad)
  Shapes = -> [Cylinder107,Cylinder108]
FEATURE [Part::Cylinder] Cylinder113  label="cylinder"
  Angle = 360
  Height = 2
  Placement = pos=(42.5,115,5) rot=(0,0,1;0rad)
  Radius = 2.5
FEATURE [Part::Cylinder] Cylinder114  label="cylinder001"
  Angle = 360
  Height = 3
  Placement = pos=(42.5,115,4) rot=(0,0,1;0rad)
  Radius = 1
FEATURE [Part::Fillet] Fillet167
  Base = -> Cylinder113
  Edges = 1 edges r=1: [Edge1]
FEATURE [Part::Cylinder] Cylinder120  label="cylinder007"
  Angle = 360
  Height = 59
  Placement = pos=(18.5,138,3) rot=(0,1,0;0.261799rad)
  Radius = 1.6
FEATURE [Part::Box] Box289  label="Cube284"
  Height = 13.5
  Length = 1
  Placement = pos=(22.75,7,43) rot=(0,-1,0;0.488692rad)
  Width = 154
FEATURE [Part::Cut] Cut171
  Base = -> Cut159
  Tool = -> Box289
FEATURE [Part::Chamfer] Chamfer057
  Base = -> Cut171
  Edges = 3 edges r=0.6: [Edge43,Edge53,Edge94]
FEATURE [Part::Box] Box290  label="Cube285"
  Height = 13.5
  Length = 1
  Placement = pos=(22.75,49,43) rot=(0,-1,0;0.488692rad)
  Width = 6
FEATURE [Part::Box] Box291  label="Cube286"
  Height = 13.5
  Length = 1
  Placement = pos=(22.75,113,43) rot=(0,-1,0;0.488692rad)
  Width = 6
FEATURE [Part::Fillet] Fillet173
  Base = -> Box291
  Edges = 2 edges r=0.99: [Edge6,Edge8]
FEATURE [Part::Fillet] Fillet174
  Base = -> Box290
  Edges = 2 edges r=0.99: [Edge6,Edge8]
FEATURE [Part::MultiFuse] Fusion157  label="dashboard"
  Placement = pos=(4,0,13) rot=(0,0,1;0rad)
  Shapes = -> [Chamfer057,Fillet173,Fillet174]
FEATURE [Part::MultiFuse] Fusion160
  Shapes = -> [Box279,Box278]
FEATURE [Part::Cut] Cut176
  Base = -> Part__Mirroring009
  Tool = -> Box776
FEATURE [Part::Cut] Cut177
  Base = -> Cut176
  Tool = -> Fusion160
FEATURE [Part::Cut] Cut178
  Base = -> Cut177
  Tool = -> Fusion143
FEATURE [Part::MultiFuse] Fusion161
  Shapes = -> [Cut178,Fillet167]
FEATURE [Part::Cut] Cut014307
  Base = -> Fusion161
  Tool = -> Cylinder114
FEATURE [Part::Cut] Cut014308  label="right-panel"
  Base = -> Cut014307
  Tool = -> Cylinder120
FEATURE [Part::Box] Box302  label="Cube297"
  Height = 4
  Length = 14
  Placement = pos=(91,52,26) rot=(0,0,1;0rad)
  Width = 10.5
FEATURE [Part::MultiFuse] Fusion162
  Shapes = -> [Box237,Box302]
FEATURE [Part::Cut] Cut181
  Base = -> Cut140
  Tool = -> Fusion162
FEATURE [Part::Cut] Cut182  label="left-panel"
  Base = -> Cut181
  Tool = -> Fusion144
FEATURE [Part::Box] Box281  label="Cube276"
  Height = 2
  Length = 28
  Placement = pos=(45,121,21) rot=(0,0,1;0rad)
  Width = 34
FEATURE [Part::Cylinder] Cylinder109
  Angle = 360
  Height = 184
  Placement = pos=(98,176,-23) rot=(1,0,0;1.5708rad)
  Radius = 53
FEATURE [Part::Cylinder] Cylinder110
  Angle = 360
  Height = 18
  Placement = pos=(47,153,4) rot=(0,0,1;0rad)
  Radius = 2
FEATURE [Part::Cylinder] Cylinder111
  Angle = 360
  Height = 18
  Placement = pos=(47,123,4) rot=(0,0,1;0rad)
  Radius = 2
FEATURE [Part::MultiFuse] Fusion146
  Shapes = -> [Cylinder110,Cylinder111,Box281]
FEATURE [Part::Cut] Cut163  label="seat-support-right"
  Base = -> Fusion146
  Tool = -> Cylinder109
FEATURE [Part::Box] Box303  label="Cube298"
  Height = 6
  Length = 24
  Placement = pos=(47,123,24) rot=(0,0,1;0rad)
  Width = 30
FEATURE [Part::Box] Box304  label="Cube299"
  Height = 6
  Length = 24
  Placement = pos=(47,125,23) rot=(0,0,1;0rad)
  Width = 26
FEATURE [Part::Box] Box305  label="Cube300"
  Height = 6
  Length = 24
  Placement = pos=(47,124.5,23.2) rot=(0,0,1;0rad)
  Width = 27
FEATURE [Part::Box] Box306  label="Cube301"
  Height = 6
  Length = 24
  Placement = pos=(47,127,24) rot=(0,0,1;0rad)
  Width = 22
FEATURE [Part::Cut] Cut183
  Base = -> Box304
  Tool = -> Box306
FEATURE [Part::Cylinder] Cylinder135  label="Cylinder152"
  Angle = 180
  Height = 24
  Placement = pos=(47,124,25.5) rot=(0,1,0;1.5708rad)
  Radius = 1.5
FEATURE [Part::Cut] Cut184
  Base = -> Box303
  Tool = -> Box305
FEATURE [Part::Cylinder] Cylinder136  label="Cylinder153"
  Angle = 360
  Height = 24
  Placement = pos=(47,152,25.5) rot=(0,1,0;1.5708rad)
  Radius = 1.5
FEATURE [Part::Cylinder] Cylinder137  label="Cylinder154"
  Angle = 360
  Height = 24
  Placement = pos=(47,124,25.5) rot=(0,1,0;1.5708rad)
  Radius = 1.5
FEATURE [Part::Cylinder] Cylinder138  label="Cylinder155"
  Angle = 180
  Height = 24
  Placement = pos=(47,152,25.5) rot=(0.707107,0,0.707107;3.14159rad)
  Radius = 1.5
FEATURE [Part::MultiFuse] Fusion163
  Shapes = -> [Cylinder135,Cylinder138]
FEATURE [Part::MultiFuse] Fusion164  label="seat-support-slider-upper-left"
  Shapes = -> [Cut184,Fusion163]
FEATURE [Part::MultiFuse] Fusion165
  Shapes = -> [Cylinder137,Cylinder136]
FEATURE [Part::Cut] Cut185
  Base = -> Cut183
  Tool = -> Fusion165
FEATURE [Part::Fillet] Fillet179  label="seat-support-slider-lower-left"
  Base = -> Cut185
  Edges = 4 edges r=1: [Edge25,Edge27,Edge33,Edge35]
FEATURE [Part::Box] Box777  label="Cube928"
  Height = 25
  Length = 5
  Placement = pos=(150,40,0) rot=(0,0,1;0rad)
  Width = 100
FEATURE [Part::Box] Box778  label="Cube929"
  Height = 40
  Length = 10
  Placement = pos=(150,19,0) rot=(-1,0,0;0.383972rad)
  Width = 20
FEATURE [Part::Box] Box779  label="Cube930"
  Height = 40
  Length = 10
  Placement = pos=(150,19,0) rot=(-1,0,0;0.383972rad)
  Width = 20
FEATURE [Part::Mirroring] Part__Mirroring115  label="Cube088 (Mirror #13)003"
  Base = (0,0,0)
  Normal = (0,1,0)
  Placement = pos=(0,180,0) rot=(0,0,1;0rad)
  Source = -> Box779
FEATURE [Part::MultiFuse] Fusion248002160
  Shapes = -> [Box778,Part__Mirroring115]
FEATURE [Part::Cut] Cut014309  label="Cut014470"
  Base = -> Box777
  Placement = pos=(-29,-5,35) rot=(0,0,1;0rad)
  Tool = -> Fusion248002160
FEATURE [Part::Box] Box780  label="Cube931"
  Height = 8
  Length = 45
  Placement = pos=(81,50.5,7) rot=(0,0,1;0rad)
  Width = 3
FEATURE [Part::Cylinder] Cylinder1236  label="Cylinder1648"
  Angle = 360
  Height = 8
  Placement = pos=(96,120,-8) rot=(1,0,0;1.5708rad)
  Radius = 1.25
FEATURE [Part::Cylinder] Cylinder1237  label="Cylinder1649"
  Angle = 360
  Height = 8
  Placement = pos=(86,120,-8) rot=(1,0,0;1.5708rad)
  Radius = 1.25
FEATURE [Part::MultiFuse] Fusion248002161
  Placement = pos=(12,-64,20) rot=(0,0,1;0rad)
  Shapes = -> [Cylinder1237,Cylinder1236]
FEATURE [Part::Box] Box782  label="Cube933"
  Height = 5
  Length = 8
  Placement = pos=(118,41.5,7) rot=(0,0,1;0rad)
  Width = 9
FEATURE [Part::MultiFuse] Fusion
  Shapes = -> [Box780,Box782]
FEATURE [Part::Box] Box783  label="battery"
  Height = 44
  Length = 22
  Placement = pos=(98,10,42) rot=(0,0,1;0rad)
  Width = 150
FEATURE [Part::Fillet] Fillet007070
  Base = -> Cut014309
  Edges = 2 edges r=6: [Edge5,Edge7]
  Placement = pos=(0,0,-7) rot=(0,0,1;0rad)
FEATURE [Part::Box] Box784  label="Cube934"
  Height = 25
  Length = 6
  Placement = pos=(150,40,0) rot=(0,0,1;0rad)
  Width = 100
FEATURE [Part::Box] Box785  label="Cube935"
  Height = 40
  Length = 10
  Placement = pos=(150,20,0) rot=(-1,0,0;0.383972rad)
  Width = 20
FEATURE [Part::Box] Box786  label="Cube936"
  Height = 40
  Length = 10
  Placement = pos=(150,19,0) rot=(-1,0,0;0.383972rad)
  Width = 20
FEATURE [Part::Mirroring] Part__Mirroring116  label="Cube088 (Mirror #13)004"
  Base = (0,0,0)
  Normal = (0,1,0)
  Placement = pos=(0,179,0) rot=(0,0,1;0rad)
  Source = -> Box786
FEATURE [Part::MultiFuse] Fusion248002162
  Shapes = -> [Box785,Part__Mirroring116]
FEATURE [Part::Cut] Cut014311  label="Cut014471"
  Base = -> Box784
  Placement = pos=(-29,-5,35) rot=(0,0,1;0rad)
  Tool = -> Fusion248002162
FEATURE [Part::Fillet] Fillet007071
  Base = -> Cut014311
  Edges = 2 edges r=5: [Edge5,Edge7]
  Placement = pos=(-1,0,-9) rot=(0,0,1;0rad)
FEATURE [Part::Box] Box787  label="Cube937"
  Height = 25
  Length = 2.75
  Placement = pos=(150,40,0) rot=(0,0,1;0rad)
  Width = 100
FEATURE [Part::Box] Box788  label="Cube938"
  Height = 40
  Length = 10
  Placement = pos=(150,19,0) rot=(-1,0,0;0.383972rad)
  Width = 20
FEATURE [Part::Box] Box789  label="Cube939"
  Height = 40
  Length = 10
  Placement = pos=(150,19,0) rot=(-1,0,0;0.383972rad)
  Width = 20
FEATURE [Part::Mirroring] Part__Mirroring117  label="Cube088 (Mirror #13)005"
  Base = (0,0,0)
  Normal = (0,1,0)
  Placement = pos=(0,180,0) rot=(0,0,1;0rad)
  Source = -> Box789
FEATURE [Part::MultiFuse] Fusion248002163
  Shapes = -> [Box788,Part__Mirroring117]
FEATURE [Part::Cut] Cut014312  label="Cut014472"
  Base = -> Box787
  Placement = pos=(-29,-5,35) rot=(0,0,1;0rad)
  Tool = -> Fusion248002163
FEATURE [Part::Fillet] Fillet007072
  Base = -> Cut014312
  Edges = 2 edges r=6: [Edge5,Edge7]
  Placement = pos=(-1,0,-3) rot=(0,0,1;0rad)
FEATURE [Part::Box] Box790  label="Cube940"
  Height = 25
  Length = 10
  Placement = pos=(116,31,10) rot=(0,0,1;0rad)
  Width = 110
FEATURE [Part::MultiFuse] Fusion248002164
  Shapes = -> [Fillet007072,Fillet007070]
FEATURE [Part::Box] Box791  label="Cube941"
  Height = 40
  Length = 10
  Placement = pos=(150,19,0) rot=(-1,0,0;0.383972rad)
  Width = 20
FEATURE [Part::Box] Box792  label="Cube942"
  Height = 40
  Length = 10
  Placement = pos=(150,19,0) rot=(-1,0,0;0.383972rad)
  Width = 20
FEATURE [Part::Mirroring] Part__Mirroring118  label="Cube088 (Mirror #13)006"
  Base = (0,0,0)
  Normal = (0,1,0)
  Placement = pos=(0,180,0) rot=(0,0,1;0rad)
  Source = -> Box792
FEATURE [Part::MultiFuse] Fusion248002165
  Placement = pos=(-27.25,-5,28) rot=(0,0,1;0rad)
  Shapes = -> [Box791,Part__Mirroring118]
FEATURE [Part::Fillet] Fillet
  Base = -> Fusion
  Edges = 2 edges r=3.99: [Edge14,Edge20]
FEATURE [Part::Chamfer] Chamfer
  Base = -> Fillet
  Edges = 1 edges r=3: [Edge24]
  Placement = pos=(1,0,0) rot=(0,0,1;0rad)
FEATURE [Part::Cut] Cut
  Base = -> Chamfer
  Tool = -> Fusion248002161
FEATURE [Part::Box] Box793  label="Cube943"
  Height = 40
  Length = 10
  Placement = pos=(150,19,0) rot=(-1,0,0;0.383972rad)
  Width = 20
FEATURE [Part::Box] Box794  label="Cube944"
  Height = 40
  Length = 10
  Placement = pos=(150,19,0) rot=(-1,0,0;0.383972rad)
  Width = 20
FEATURE [Part::Mirroring] Part__Mirroring119  label="Cube088 (Mirror #13)007"
  Base = (0,0,0)
  Normal = (0,1,0)
  Placement = pos=(0,180,0) rot=(0,0,1;0rad)
  Source = -> Box794
FEATURE [Part::MultiFuse] Fusion248002166
  Placement = pos=(-33,-5,32) rot=(0,0,1;0rad)
  Shapes = -> [Box793,Part__Mirroring119]
FEATURE [Part::Cylinder] Cylinder1239
  Angle = 360
  Height = 39
  Placement = pos=(123,46,6) rot=(1,0,0;0.122173rad)
  Radius = 3
FEATURE [Part::Cylinder] Cylinder1240
  Angle = 360
  Height = 29
  Placement = pos=(123,46,6) rot=(1,0,0;0.122173rad)
  Radius = 3
FEATURE [Part::Cut] Cut014315
  Base = -> Cylinder1239
  Tool = -> Cylinder1240
FEATURE [Part::Cylinder] Cylinder1241
  Angle = 360
  Height = 4
  Placement = pos=(123,46,6) rot=(1,0,0;0.122173rad)
  Radius = 3.1
FEATURE [Part::Cylinder] Cylinder1242
  Angle = 360
  Height = 34
  Placement = pos=(123,46,6) rot=(1,0,0;0.122173rad)
  Radius = 1.25
FEATURE [Part::MultiFuse] Fusion248002167
  Shapes = -> [Cylinder1241,Cylinder1242]
FEATURE [Part::Cylinder] Cylinder1243
  Angle = 360
  Height = 5
  Placement = pos=(123,46,6) rot=(1,0,0;0.122173rad)
  Radius = 3
FEATURE [Part::Cylinder] Cylinder1244
  Angle = 360
  Height = 7
  Placement = pos=(123,46,6) rot=(1,0,0;0.122173rad)
  Radius = 3
FEATURE [Part::Cut] Cut014317
  Base = -> Cylinder1244
  Tool = -> Cylinder1243
FEATURE [Part::MultiFuse] Fusion248002168
  Shapes = -> [Cut,Cut014317]
FEATURE [Part::Cut] Cut014318
  Base = -> Fusion248002168
  Tool = -> Fusion248002167
FEATURE [Part::Cylinder] Cylinder1245
  Angle = 360
  Height = 29
  Placement = pos=(123,46,6) rot=(1,0,0;0.122173rad)
  Radius = 2.2
FEATURE [Part::Cylinder] Cylinder1246
  Angle = 360
  Height = 7
  Placement = pos=(123,46,6) rot=(1,0,0;0.122173rad)
  Radius = 3
FEATURE [Part::Cut] Cut014319
  Base = -> Cylinder1245
  Tool = -> Cylinder1246
FEATURE [Part::Cylinder] Cylinder1247
  Angle = 360
  Height = 39
  Placement = pos=(123,46,6) rot=(-1,0,0;0.122173rad)
  Radius = 3
FEATURE [Part::Cylinder] Cylinder1248
  Angle = 360
  Height = 29
  Placement = pos=(123,46,6) rot=(-1,0,0;0.122173rad)
  Radius = 3
FEATURE [Part::Cut] Cut014320
  Base = -> Cylinder1247
  Placement = pos=(0,78,0) rot=(0,0,1;0rad)
  Tool = -> Cylinder1248
FEATURE [Part::Cylinder] Cylinder1249
  Angle = 360
  Height = 34
  Placement = pos=(123,46,6) rot=(1,0,0;0.122173rad)
  Radius = 1.6
FEATURE [Part::Cut] Cut014321  label="cab-dampers-tube-left"
  Base = -> Cut014319
  Tool = -> Cylinder1249
FEATURE [Part::Cylinder] Cylinder1250
  Angle = 360
  Height = 29
  Placement = pos=(123,46,6) rot=(-1,0,0;0.122173rad)
  Radius = 2.2
FEATURE [Part::Cylinder] Cylinder1251
  Angle = 360
  Height = 7
  Placement = pos=(123,46,6) rot=(-1,0,0;0.122173rad)
  Radius = 3
FEATURE [Part::Cut] Cut014322
  Base = -> Cylinder1250
  Tool = -> Cylinder1251
FEATURE [Part::Cylinder] Cylinder1252
  Angle = 360
  Height = 34
  Placement = pos=(123,46,6) rot=(-1,0,0;0.122173rad)
  Radius = 1.6
FEATURE [Part::Cut] Cut014323  label="cab-dampers-tube-right"
  Base = -> Cut014322
  Placement = pos=(0,78,0) rot=(0,0,1;0rad)
  Tool = -> Cylinder1252
FEATURE [Part::Box] Box795  label="Cube945"
  Height = 8
  Length = 45
  Placement = pos=(81,50.5,7) rot=(0,0,1;0rad)
  Width = 3
FEATURE [Part::Cylinder] Cylinder1253  label="Cylinder1650"
  Angle = 360
  Height = 8
  Placement = pos=(96,120,-8) rot=(1,0,0;1.5708rad)
  Radius = 1.25
FEATURE [Part::Cylinder] Cylinder1254  label="Cylinder1651"
  Angle = 360
  Height = 8
  Placement = pos=(86,120,-8) rot=(1,0,0;1.5708rad)
  Radius = 1.25
FEATURE [Part::MultiFuse] Fusion248002169
  Placement = pos=(12,-64,20) rot=(0,0,1;0rad)
  Shapes = -> [Cylinder1254,Cylinder1253]
FEATURE [Part::Box] Box796  label="Cube946"
  Height = 5
  Length = 8
  Placement = pos=(118,41.5,7) rot=(0,0,1;0rad)
  Width = 9
FEATURE [Part::MultiFuse] Fusion248002170
  Shapes = -> [Box795,Box796]
FEATURE [Part::Fillet] Fillet007073
  Base = -> Fusion248002170
  Edges = 2 edges r=3.99: [Edge14,Edge20]
FEATURE [Part::Chamfer] Chamfer171
  Base = -> Fillet007073
  Edges = 1 edges r=3: [Edge24]
  Placement = pos=(1,0,0) rot=(0,0,1;0rad)
FEATURE [Part::Cut] Cut014324
  Base = -> Chamfer171
  Tool = -> Fusion248002169
FEATURE [Part::Cylinder] Cylinder1255
  Angle = 360
  Height = 4
  Placement = pos=(123,46,6) rot=(1,0,0;0.122173rad)
  Radius = 3.1
FEATURE [Part::Cylinder] Cylinder1256
  Angle = 360
  Height = 34
  Placement = pos=(123,46,6) rot=(1,0,0;0.122173rad)
  Radius = 1.25
FEATURE [Part::MultiFuse] Fusion248002171
  Shapes = -> [Cylinder1255,Cylinder1256]
FEATURE [Part::Cylinder] Cylinder1257
  Angle = 360
  Height = 5
  Placement = pos=(123,46,6) rot=(1,0,0;0.122173rad)
  Radius = 3
FEATURE [Part::Cylinder] Cylinder1258
  Angle = 360
  Height = 7
  Placement = pos=(123,46,6) rot=(1,0,0;0.122173rad)
  Radius = 3
FEATURE [Part::Cut] Cut014325
  Base = -> Cylinder1258
  Tool = -> Cylinder1257
FEATURE [Part::MultiFuse] Fusion248002172
  Shapes = -> [Cut014324,Cut014325]
FEATURE [Part::Cut] Cut014326
  Base = -> Fusion248002172
  Tool = -> Fusion248002171
FEATURE [Part::Mirroring] Part__Mirroring  label="Cut014326 (Mirror #30)"
  Base = (0,0,0)
  Normal = (0,1,0)
  Placement = pos=(0,170,0) rot=(0,0,1;0rad)
  Source = -> Cut014326
FEATURE [Part::MultiFuse] Fusion248002174
  Shapes = -> [Fusion248002165,Fusion248002166]
FEATURE [Part::Cut] Cut014327
  Base = -> Fusion248002164
  Tool = -> Fillet007071
FEATURE [Part::Cut] Cut014328
  Base = -> Cut014327
  Tool = -> Box790
FEATURE [Part::MultiFuse] Fusion248002175
  Shapes = -> [Cut014328,Cut014315,Cut014320]
FEATURE [Part::Cut] Cut014329
  Base = -> Fusion248002175
  Tool = -> Fusion248002174
FEATURE [Part::Cylinder] Cylinder
  Angle = 360
  Height = 10
  Placement = pos=(114,65,55) rot=(0,1,0;1.5708rad)
  Radius = 0.9
FEATURE [Part::Cylinder] Cylinder1259
  Angle = 360
  Height = 10
  Placement = pos=(114,105,55) rot=(0,1,0;1.5708rad)
  Radius = 0.9
FEATURE [Part::MultiFuse] Fusion248002176
  Shapes = -> [Cylinder,Cylinder1259]
FEATURE [Part::Cut] Cut014330
  Base = -> Cut014329
  Tool = -> Fusion248002176
FEATURE [Part::Fillet] Fillet007074
  Base = -> Cut014330
  Edges = 4 edges r=0.5: [Edge39,Edge41,Edge44,Edge48]
FEATURE [Part::Fillet] Fillet007075  label="cab-dampers-upper-attach_"
  Base = -> Fillet007074
  Edges = 2 edges r=1: [Edge30,Edge51]
FEATURE [Part::Fillet] Fillet007076  label="cab-dampers-attach-left"
  Base = -> Cut014318
  Edges = 1 edges r=3: [Edge34]
FEATURE [Part::Fillet] Fillet007077  label="cab-dampers-attach-right"
  Base = -> Part__Mirroring
  Edges = 1 edges r=3: [Edge34]
FEATURE [Part::Cylinder] Cylinder1260
  Angle = 360
  Height = 34
  Placement = pos=(123,124,6) rot=(-1,0,0;0.122173rad)
  Radius = 1.25
FEATURE [Part::Cylinder] Cylinder1261
  Angle = 360
  Height = 34
  Placement = pos=(123,46,6) rot=(1,0,0;0.122173rad)
  Radius = 1.25
FEATURE [Part::MultiFuse] Fusion248002177
  Shapes = -> [Cylinder1260,Cylinder1261]
FEATURE [Part::Cut] Cut014331  label="cab-dampers-upper-attach"
  Base = -> Fillet007075
  Tool = -> Fusion248002177
FEATURE [Part::Cut] Cut014188  label="hitec-hs85bb"
  Placement = pos=(23.5,149.5,14) rot=(0.57735,0.57735,-0.57735;2.0944rad)
FEATURE [Part::Cut] Cut014189  label="cross-member-front001"
  Placement = pos=(0,0,3) rot=(0,0,1;0rad)
FEATURE [Part::Box] Box509  label="Cube711"
  Height = 7
  Length = 23
  Placement = pos=(14,116.5,-24.5) rot=(0,0,1;0rad)
  Width = 10
FEATURE [Part::Box] Box510  label="Cube712"
  Height = 44
  Length = 10
  Placement = pos=(14,116.5,-24.5) rot=(0,0,1;0rad)
  Width = 10
FEATURE [Part::Box] Box511  label="Cube713"
  Height = 7
  Length = 23
  Placement = pos=(14,116.5,12.5) rot=(0,0,1;0rad)
  Width = 10
FEATURE [Part::Box] Box512  label="Cube714"
  Height = 7
  Length = 22
  Placement = pos=(17,111.5,12.5) rot=(0,0,1;0rad)
  Width = 10
FEATURE [Part::MultiFuse] Fusion621
  Shapes = -> [Box511,Box509,Box510]
FEATURE [Part::Cut] Cut014190
  Base = -> Fusion621
  Placement = pos=(-0.5,0,0) rot=(0,0,1;0rad)
  Tool = -> Box512
FEATURE [Part::Box] Box513  label="Cube715"
  Height = 17
  Length = 1
  Placement = pos=(13.5,113.5,4.5) rot=(0,0,1;0rad)
  Width = 13
FEATURE [Part::Cylinder] Cylinder845  label="Cylinder971"
  Angle = 360
  Height = 10
  Placement = pos=(18,116.5,2) rot=(-1,0,0;1.5708rad)
  Radius = 1.6
FEATURE [Part::Cylinder] Cylinder846  label="Cylinder972"
  Angle = 360
  Height = 10
  Placement = pos=(18,116.5,-9) rot=(-1,0,0;1.5708rad)
  Radius = 1.6
FEATURE [Part::Box] Box514  label="Cube716"
  Height = 31.5
  Length = 9
  Placement = pos=(13.5,113.5,-24.5) rot=(0,0,1;0rad)
  Width = 10
FEATURE [Part::MultiFuse] Fusion622
  Shapes = -> [Box514,Cut014190]
FEATURE [Part::Cylinder] Cylinder847  label="Cylinder973"
  Angle = 360
  Height = 10
  Placement = pos=(30,116.5,17.15) rot=(-1,0,0;1.5708rad)
  Radius = 0.9
FEATURE [Part::Cylinder] Cylinder848  label="Cylinder974"
  Angle = 360
  Height = 10
  Placement = pos=(30,116.5,-18.15) rot=(-1,0,0;1.5708rad)
  Radius = 0.9
FEATURE [Part::MultiFuse] Fusion623
  Shapes = -> [Cylinder845,Cylinder846,Cylinder847,Cylinder848]
FEATURE [Part::Box] Box515  label="Cube717"
  Height = 5
  Length = 3
  Placement = pos=(14.5,116.5,14.5) rot=(0,0,1;0rad)
  Width = 5
FEATURE [Part::Box] Box516  label="Cube718"
  Height = 44
  Length = 2
  Placement = pos=(36.5,121.5,-24.5) rot=(0,0,1;0rad)
  Width = 5
FEATURE [Part::MultiFuse] Fusion624
  Placement = pos=(0,0,2) rot=(0,0,1;0rad)
  Shapes = -> [Fusion622,Box516]
FEATURE [Part::Cut] Cut014191
  Base = -> Fusion624
  Tool = -> Box513
FEATURE [Part::Cut] Cut014192
  Base = -> Cut014191
  Tool = -> Cut014189
FEATURE [Part::Cut] Cut014332
  Base = -> Cut014192
  Tool = -> Fusion623
FEATURE [Part::Fillet] Fillet007078
  Base = -> Cut014332
  Edges = 2 edges r=8.99: [Edge14,Edge33]
FEATURE [Part::Cut] Cut014333
  Base = -> Fillet007078
  Tool = -> Box515
FEATURE [Part::Chamfer] Chamfer163
  Base = -> Cut014333
  Edges = 1 edges r=6: [Edge62]
FEATURE [Part::Cylinder] Cylinder236
  Angle = 79
  Height = 62
  Placement = pos=(25,21,0) rot=(0,0,1;3.28122rad)
  Radius = 29
FEATURE [Part::Cylinder] Cylinder237
  Angle = 360
  Height = 62
  Placement = pos=(25,21,0) rot=(0,0,1;0rad)
  Radius = 18
FEATURE [Part::Cut] Cut401  label="Cut723"
  Base = -> Cylinder236
  Tool = -> Cylinder237
FEATURE [Part::Box] Box406  label="Cube632"
  Height = 2
  Length = 48
  Placement = pos=(5,3,0) rot=(0,0,1;0rad)
  Width = 15
FEATURE [Part::Cylinder] Cylinder238
  Angle = 360
  Height = 62
  Placement = pos=(25,21,0) rot=(0,0,1;0rad)
  Radius = 16.5
FEATURE [Part::Cylinder] Cylinder239
  Angle = 46
  Height = 62
  Placement = pos=(25,21,0) rot=(0,0,1;3.3074rad)
  Radius = 18
FEATURE [Part::Cut] Cut402  label="Cut724"
  Base = -> Cylinder239
  Tool = -> Cylinder238
FEATURE [Part::Cut] Cut403  label="Cut725"
  Base = -> Box406
  Tool = -> Cut401
FEATURE [Part::Box] Box407  label="Cube633"
  Height = 62
  Length = 3
  Placement = pos=(6,18,0) rot=(0,0,1;0rad)
  Width = 1
FEATURE [Part::Cut] Cut404  label="Cut726"
  Base = -> Cut402
  Tool = -> Box407
FEATURE [Part::Cylinder] Cylinder240
  Angle = 360
  Height = 22
  Placement = pos=(98,18,-23) rot=(1,0,0;1.5708rad)
  Radius = 52
FEATURE [Part::Cut] Cut405  label="Cut727"
  Base = -> Cut403
  Tool = -> Cylinder240
FEATURE [Part::Cylinder] Cylinder241
  Angle = 360
  Height = 13
  Placement = pos=(11.9886,10.7385,16) rot=(0.884029,-0.330525,-0.330525;1.69375rad)
  Radius = 1.2
FEATURE [Part::Cylinder] Cylinder242
  Angle = 360
  Height = 13
  Placement = pos=(11.9886,10.7385,51) rot=(0.884029,-0.330525,-0.330525;1.69375rad)
  Radius = 1.2
FEATURE [Part::MultiFuse] Fusion206
  Placement = pos=(0.87,1,0) rot=(0,0,1;0rad)
  Shapes = -> [Cylinder241,Cylinder242]
FEATURE [Part::Cylinder] Cylinder243
  Angle = 360
  Height = 1.6
  Placement = pos=(11.9886,10.7385,16) rot=(0.884029,-0.330525,-0.330525;1.69375rad)
  Radius = 2
FEATURE [Part::Cylinder] Cylinder244
  Angle = 360
  Height = 1.6
  Placement = pos=(11.9886,10.7385,51) rot=(0.884029,-0.330525,-0.330525;1.69375rad)
  Radius = 2
FEATURE [Part::MultiFuse] Fusion207
  Placement = pos=(0.87,1,0) rot=(0,0,1;0rad)
  Shapes = -> [Cylinder243,Cylinder244]
FEATURE [Part::MultiFuse] Fusion208
  Shapes = -> [Cut404,Cut405,Fusion207]
FEATURE [Part::Cut] Cut406  label="Cut728"
  Base = -> Fusion208
  Tool = -> Fusion206
FEATURE [Part::Cylinder] Cylinder247
  Angle = 360
  Height = 10
  Placement = pos=(18,15,-5) rot=(0,0,1;0rad)
  Radius = 1.2
FEATURE [Part::Cylinder] Cylinder248
  Angle = 360
  Height = 10
  Placement = pos=(49,15,-5) rot=(0,0,1;0rad)
  Radius = 1.2
FEATURE [Part::MultiFuse] Fusion210
  Shapes = -> [Cylinder247,Cylinder248]
FEATURE [Part::Cut] Cut407  label="inner-door-swing-arm-left"
  Base = -> Cut406
  Tool = -> Fusion210
FEATURE [Part::Cylinder] Cylinder335
  Angle = 79
  Height = 62
  Placement = pos=(25,21,0) rot=(0,0,1;3.28122rad)
  Radius = 29
FEATURE [Part::Cylinder] Cylinder336
  Angle = 360
  Height = 62
  Placement = pos=(25,21,0) rot=(0,0,1;0rad)
  Radius = 18
FEATURE [Part::Cut] Cut553  label="Cut844"
  Base = -> Cylinder335
  Tool = -> Cylinder336
FEATURE [Part::Box] Box626  label="Cube947"
  Height = 2
  Length = 48
  Placement = pos=(5,3,0) rot=(0,0,1;0rad)
  Width = 15
FEATURE [Part::Cylinder] Cylinder337
  Angle = 360
  Height = 62
  Placement = pos=(25,21,0) rot=(0,0,1;0rad)
  Radius = 16.5
FEATURE [Part::Cylinder] Cylinder338
  Angle = 46
  Height = 62
  Placement = pos=(25,21,0) rot=(0,0,1;3.3074rad)
  Radius = 18
FEATURE [Part::Cut] Cut554  label="Cut845"
  Base = -> Cylinder338
  Tool = -> Cylinder337
FEATURE [Part::Cut] Cut555  label="Cut846"
  Base = -> Box626
  Tool = -> Cut553
FEATURE [Part::Box] Box627  label="Cube852"
  Height = 62
  Length = 3
  Placement = pos=(6,18,0) rot=(0,0,1;0rad)
  Width = 1
FEATURE [Part::Cut] Cut556  label="Cut847"
  Base = -> Cut554
  Tool = -> Box627
FEATURE [Part::Cylinder] Cylinder339
  Angle = 360
  Height = 22
  Placement = pos=(98,18,-23) rot=(1,0,0;1.5708rad)
  Radius = 52
FEATURE [Part::Cut] Cut557  label="Cut848"
  Base = -> Cut555
  Tool = -> Cylinder339
FEATURE [Part::Cylinder] Cylinder340
  Angle = 360
  Height = 13
  Placement = pos=(11.9886,10.7385,16) rot=(0.884029,-0.330525,-0.330525;1.69375rad)
  Radius = 1.2
FEATURE [Part::Cylinder] Cylinder341
  Angle = 360
  Height = 13
  Placement = pos=(11.9886,10.7385,51) rot=(0.884029,-0.330525,-0.330525;1.69375rad)
  Radius = 1.2
FEATURE [Part::MultiFuse] Fusion336
  Placement = pos=(0.87,1,0) rot=(0,0,1;0rad)
  Shapes = -> [Cylinder340,Cylinder341]
FEATURE [Part::Cylinder] Cylinder342
  Angle = 360
  Height = 1.6
  Placement = pos=(11.9886,10.7385,16) rot=(0.884029,-0.330525,-0.330525;1.69375rad)
  Radius = 2
FEATURE [Part::Cylinder] Cylinder343
  Angle = 360
  Height = 1.6
  Placement = pos=(11.9886,10.7385,51) rot=(0.884029,-0.330525,-0.330525;1.69375rad)
  Radius = 2
FEATURE [Part::MultiFuse] Fusion337
  Placement = pos=(0.87,1,0) rot=(0,0,1;0rad)
  Shapes = -> [Cylinder342,Cylinder343]
FEATURE [Part::MultiFuse] Fusion338
  Shapes = -> [Cut556,Cut557,Fusion337]
FEATURE [Part::Cut] Cut558  label="Cut849"
  Base = -> Fusion338
  Tool = -> Fusion336
FEATURE [Part::Cylinder] Cylinder344
  Angle = 360
  Height = 10
  Placement = pos=(18,15,-5) rot=(0,0,1;0rad)
  Radius = 1.2
FEATURE [Part::Cylinder] Cylinder345
  Angle = 360
  Height = 10
  Placement = pos=(49,15,-5) rot=(0,0,1;0rad)
  Radius = 1.2
FEATURE [Part::MultiFuse] Fusion339
  Shapes = -> [Cylinder344,Cylinder345]
FEATURE [Part::Cut] Cut559  label="inner-door-swing-arm-left001"
  Base = -> Cut558
  Tool = -> Fusion339
FEATURE [Part::Mirroring] Part__Mirroring067  label="inner-door-swing-arm-right"
  Base = (0,0,0)
  Normal = (0,1,0)
  Placement = pos=(0,170,0) rot=(0,0,1;0rad)
  Source = -> Cut559
FEATURE [Part::Box] Box797  label="Cube948"
  Height = 4
  Length = 19
  Placement = pos=(88.5,3.5,35) rot=(0,0,1;0rad)
  Width = 4
FEATURE [Part::Box] Box798  label="Cube949"
  Height = 37
  Length = 1
  Placement = pos=(16,6,11) rot=(0,0,1;0rad)
  Width = 52.5
FEATURE [Part::Box] Box799  label="Cube950"
  Height = 2
  Length = 35
  Placement = pos=(16,3.5,8) rot=(0,0,1;0rad)
  Width = 8.5
FEATURE [Part::Box] Box800  label="Cube951"
  Height = 1
  Length = 38
  Placement = pos=(16,3.5,10) rot=(0,0,1;0rad)
  Width = 55
FEATURE [Part::Cylinder] Cylinder1263
  Angle = 61
  Height = 55
  Placement = pos=(98,3.5,-15) rot=(0.179887,0.695572,0.695572;3.49756rad)
  Radius = 53
FEATURE [Part::Cylinder] Cylinder1264
  Angle = 360
  Height = 55
  Placement = pos=(98,3.5,-15) rot=(-1,0,0;1.5708rad)
  Radius = 52
FEATURE [Part::MultiFuse] Fusion248002178
  Shapes = -> [Box800,Cylinder1263]
FEATURE [Part::Box] Box801  label="Cube952"
  Height = 1
  Length = 24.5
  Placement = pos=(98,3.5,37) rot=(0,0,1;0rad)
  Width = 50
FEATURE [Part::Box] Box802  label="Cube953"
  Height = 10
  Length = 38
  Placement = pos=(45,11,30) rot=(0,0,1;0rad)
  Width = 38
FEATURE [Part::Box] Box803  label="Cube954"
  Height = 45
  Length = 13
  Placement = pos=(75,11,30) rot=(0,0,1;0rad)
  Width = 38
FEATURE [Part::Chamfer] Chamfer173
  Base = -> Box802
  Edges = 2 edges: [Edge2 r1=2 r2=12,Edge6 r1=2 r2=12]
FEATURE [Part::Fillet] Fillet007079
  Base = -> Chamfer173
  Edges = 3 edges r=3: [Edge3,Edge13,Edge17]
FEATURE [Part::Fillet] Fillet007080
  Base = -> Fillet007079
  Edges = 1 edges r=5: [Edge3]
FEATURE [Part::Fillet] Fillet007081
  Base = -> Fillet007080
  Edges = 6 edges r=2: [Edge7,Edge9,Edge11,Edge18,Edge20,Edge22]
FEATURE [Part::Fillet] Fillet007082
  Base = -> Fillet007081
  Edges = 2 edges r=20: [Edge23,Edge49]
FEATURE [Part::Chamfer] Chamfer174
  Base = -> Box803
  Edges = 1 edges: [Edge2 r1=20 r2=5]
FEATURE [Part::Chamfer] Chamfer175
  Base = -> Chamfer174
  Edges = 1 edges: [Edge3 r1=15 r2=3]
FEATURE [Part::Fillet] Fillet007083
  Base = -> Chamfer175
  Edges = 4 edges r=3: [Edge10,Edge12,Edge17,Edge18]
FEATURE [Part::Fillet] Fillet007084
  Base = -> Fillet007083
  Edges = 2 edges r=20: [Edge12,Edge16]
FEATURE [Part::Fillet] Fillet007085
  Base = -> Fillet007084
  Edges = 10 edges r=2: [Edge1,Edge2,Edge4,Edge6,Edge8,Edge15,Edge17,Edge21,Edge25,Edge29]
FEATURE [Part::Box] Box804  label="Cube955"
  Height = 48
  Length = 7
  Placement = pos=(69,12,30) rot=(0,1,0;0.10472rad)
  Width = 36
FEATURE [Part::Box] Box805  label="Cube956"
  Height = 50
  Length = 16
  Placement = pos=(75,0,30) rot=(-0.683576,-0.016559,0.729691;0.239394rad)
  Width = 8
FEATURE [Part::Box] Box806  label="Cube957"
  Height = 50
  Length = 16
  Placement = pos=(75,0,30) rot=(-0.683576,-0.016559,0.729691;0.239394rad)
  Width = 8
FEATURE [Part::Mirroring] Part__Mirroring120  label="Cube241 (Mirror #7)002"
  Base = (0,0,0)
  Normal = (0,1,0)
  Placement = pos=(0,60,0) rot=(0,0,1;0rad)
  Source = -> Box806
FEATURE [Part::MultiFuse] Fusion248002181
  Shapes = -> [Part__Mirroring120,Box805]
FEATURE [Part::Cut] Cut014335
  Base = -> Fillet007085
  Tool = -> Fusion248002181
FEATURE [Part::Fillet] Fillet007086
  Base = -> Cut014335
  Edges = 4 edges r=1.6: [Edge19,Edge23,Edge40,Edge49]
FEATURE [Part::Chamfer] Chamfer176
  Base = -> Box804
  Edges = 2 edges: [Edge10 r1=40 r2=4,Edge12 r1=40 r2=4]
FEATURE [Part::Chamfer] Chamfer177
  Base = -> Chamfer176
  Edges = 2 edges: [Edge11 r1=4 r2=7,Edge18 r1=4 r2=7]
FEATURE [Part::Fillet] Fillet007087
  Base = -> Chamfer177
  Edges = 2 edges r=10: [Edge18,Edge24]
  Placement = pos=(-0.75,0,0) rot=(0,0,1;0rad)
FEATURE [Part::Cut] Cut014336
  Base = -> Fillet007086
  Tool = -> Fillet007087
FEATURE [Part::Fillet] Fillet007088
  Base = -> Cut014336
  Edges = 2 edges r=2.5: [Edge93,Edge106]
FEATURE [Part::Box] Box807  label="Cube958"
  Height = 8
  Length = 10
  Placement = pos=(78,11,32) rot=(0,0,1;0rad)
  Width = 2
FEATURE [Part::Fillet] Fillet007089
  Base = -> Box807
  Edges = 2 edges r=2: [Edge6,Edge8]
FEATURE [Part::Box] Box808  label="Cube959"
  Height = 7
  Length = 10
  Placement = pos=(75,10,30) rot=(0,0,1;0rad)
  Width = 3
FEATURE [Part::Chamfer] Chamfer178
  Base = -> Box808
  Edges = 1 edges r=3: [Edge6]
FEATURE [Part::Chamfer] Chamfer179
  Base = -> Chamfer178
  Edges = 1 edges: [Edge3 r1=2 r2=4]
FEATURE [Part::Chamfer] Chamfer180
  Base = -> Chamfer179
  Edges = 1 edges: [Edge18 r1=6 r2=2]
FEATURE [Part::Chamfer] Chamfer181
  Base = -> Chamfer180
  Edges = 1 edges r=3: [Edge15]
  Placement = pos=(0,1,0) rot=(0,0,1;0rad)
FEATURE [Part::Box] Box809  label="Cube960"
  Height = 8
  Length = 10
  Placement = pos=(78,11,32) rot=(0,0,1;0rad)
  Width = 2
FEATURE [Part::Fillet] Fillet007090
  Base = -> Box809
  Edges = 2 edges r=2: [Edge6,Edge8]
FEATURE [Part::Box] Box810  label="Cube961"
  Height = 7
  Length = 10
  Placement = pos=(75,10,30) rot=(0,0,1;0rad)
  Width = 3
FEATURE [Part::Chamfer] Chamfer182
  Base = -> Box810
  Edges = 1 edges r=3: [Edge6]
FEATURE [Part::Chamfer] Chamfer183
  Base = -> Chamfer182
  Edges = 1 edges: [Edge3 r1=2 r2=4]
FEATURE [Part::Chamfer] Chamfer184
  Base = -> Chamfer183
  Edges = 1 edges: [Edge18 r1=6 r2=2]
FEATURE [Part::Chamfer] Chamfer185
  Base = -> Chamfer184
  Edges = 1 edges r=3: [Edge15]
  Placement = pos=(0,1,0) rot=(0,0,1;0rad)
FEATURE [Part::MultiFuse] Fusion248002182
  Shapes = -> [Fillet007090,Chamfer185]
FEATURE [Part::Mirroring] Part__Mirroring121  label="Fusion121 (Mirror #9)002"
  Base = (0,0,0)
  Normal = (0,1,0)
  Placement = pos=(0,60,0) rot=(0,0,1;0rad)
  Source = -> Fusion248002182
FEATURE [Part::Cylinder] Cylinder1265
  Angle = 360
  Height = 39
  Placement = pos=(81,10.5,35) rot=(-1,0,0;1.5708rad)
  Radius = 1
FEATURE [Part::MultiFuse] Fusion248002183
  Shapes = -> [Fillet007089,Chamfer181]
FEATURE [Part::MultiFuse] Fusion248002184
  Shapes = -> [Part__Mirroring121,Fusion248002183]
FEATURE [Part::MultiFuse] Fusion248002185
  Shapes = -> [Fusion248002184,Cylinder1265]
FEATURE [Part::MultiFuse] Fusion248002186  label="seat-left"
  Placement = pos=(9,0,19) rot=(0,0,1;0rad)
  Shapes = -> [Fillet007088,Fusion248002185,Fillet007082]
FEATURE [Part::Box] Box811  label="Cube962"
  Height = 22
  Length = 10
  Placement = pos=(4,3.5,35) rot=(0,0,1;0rad)
  Width = 161
FEATURE [Part::Box] Box812  label="Cube963"
  Height = 22
  Length = 10
  Placement = pos=(14,3.5,35) rot=(0,0,1;0rad)
  Width = 161
FEATURE [Part::Chamfer] Chamfer186
  Base = -> Box812
  Edges = 1 edges: [Edge6 r1=15 r2=8]
FEATURE [Part::Chamfer] Chamfer187
  Base = -> Chamfer186
  Edges = 1 edges r=5: [Edge3]
FEATURE [Part::MultiFuse] Fusion248002188
  Shapes = -> [Box811,Chamfer187]
FEATURE [Part::Box] Box813  label="Cube964"
  Height = 22
  Length = 17
  Placement = pos=(4,4,35) rot=(0,0,1;0rad)
  Width = 160
FEATURE [Part::Box] Box814  label="Cube965"
  Height = 22
  Length = 18
  Placement = pos=(3,3,35) rot=(0,0,1;0rad)
  Width = 162
FEATURE [Part::Fillet] Fillet007092
  Base = -> Box813
  Edges = 2 edges r=15: [Edge1,Edge3]
FEATURE [Part::Cut] Cut014338
  Base = -> Box814
  Tool = -> Fillet007092
FEATURE [Part::Fillet] Fillet007093
  Base = -> Fusion248002188
  Edges = 4 edges r=2: [Edge2,Edge3,Edge6,Edge9]
  Placement = pos=(3,0,13) rot=(0,0,1;0rad)
FEATURE [Part::Box] Box815  label="Cube966"
  Height = 31
  Length = 9
  Placement = pos=(4,46,14) rot=(0,0,1;0rad)
  Width = 77
FEATURE [Part::Box] Box816  label="Cube967"
  Height = 46
  Length = 20
  Placement = pos=(16,55.5,4.5) rot=(0,0,1;0rad)
  Width = 57
FEATURE [Part::Fillet] Fillet007094
  Base = -> Box816
  Edges = 2 edges r=3: [Edge10,Edge12]
FEATURE [Part::Box] Box817  label="Cube968"
  Height = 13.5
  Length = 1
  Placement = pos=(22.75,7,43) rot=(0,-1,0;0.488692rad)
  Width = 154
FEATURE [Part::Box] Box818  label="Cube969"
  Height = 13.5
  Length = 1
  Placement = pos=(22.75,49,43) rot=(0,-1,0;0.488692rad)
  Width = 6
FEATURE [Part::Box] Box819  label="Cube970"
  Height = 13.5
  Length = 1
  Placement = pos=(22.75,113,43) rot=(0,-1,0;0.488692rad)
  Width = 6
FEATURE [Part::Fillet] Fillet007095
  Base = -> Box819
  Edges = 2 edges r=0.99: [Edge6,Edge8]
FEATURE [Part::Fillet] Fillet007096
  Base = -> Box818
  Edges = 2 edges r=0.99: [Edge6,Edge8]
FEATURE [Part::Box] Box  label="receiver"
  Height = 27
  Length = 47
  Placement = pos=(33,55,16) rot=(0,0,1;0rad)
  Width = 15
FEATURE [Part::Cylinder] Cylinder1266
  Angle = 61
  Height = 68
  Placement = pos=(98,51,-15) rot=(0.179887,0.695572,0.695572;3.49755rad)
  Radius = 53
FEATURE [Part::Box] Box820  label="Cube971"
  Height = 50
  Length = 81
  Placement = pos=(16,58.5,1) rot=(0,0,1;0rad)
  Width = 53
FEATURE [Part::Cut] Cut014339
  Base = -> Fusion248002178
  Tool = -> Cylinder1264
FEATURE [Part::MultiFuse] Fusion248002189
  Shapes = -> [Cut014339,Box799]
FEATURE [Part::MultiFuse] Fusion248002190
  Shapes = -> [Fusion248002189,Box801]
FEATURE [Part::Chamfer] Chamfer188
  Base = -> Fusion248002190
  Edges = 1 edges: [Edge32 r1=2.5 r2=8]
FEATURE [Part::MultiFuse] Fusion248002191
  Shapes = -> [Chamfer188,Box798]
FEATURE [Part::Cut] Cut014340
  Base = -> Fusion248002191
  Tool = -> Box797
FEATURE [Part::Box] Box821  label="Cube972"
  Height = 50
  Length = 81
  Placement = pos=(36,53.5,1) rot=(0,0,1;0rad)
  Width = 63
FEATURE [Part::MultiFuse] Fusion248002192
  Shapes = -> [Box821,Box820]
FEATURE [Part::Chamfer] Chamfer189
  Base = -> Fusion248002192
  Edges = 2 edges r=2.49: [Edge4,Edge9]
FEATURE [Part::Fillet] Fillet007097
  Base = -> Chamfer189
  Edges = 2 edges r=5: [Edge2,Edge26]
